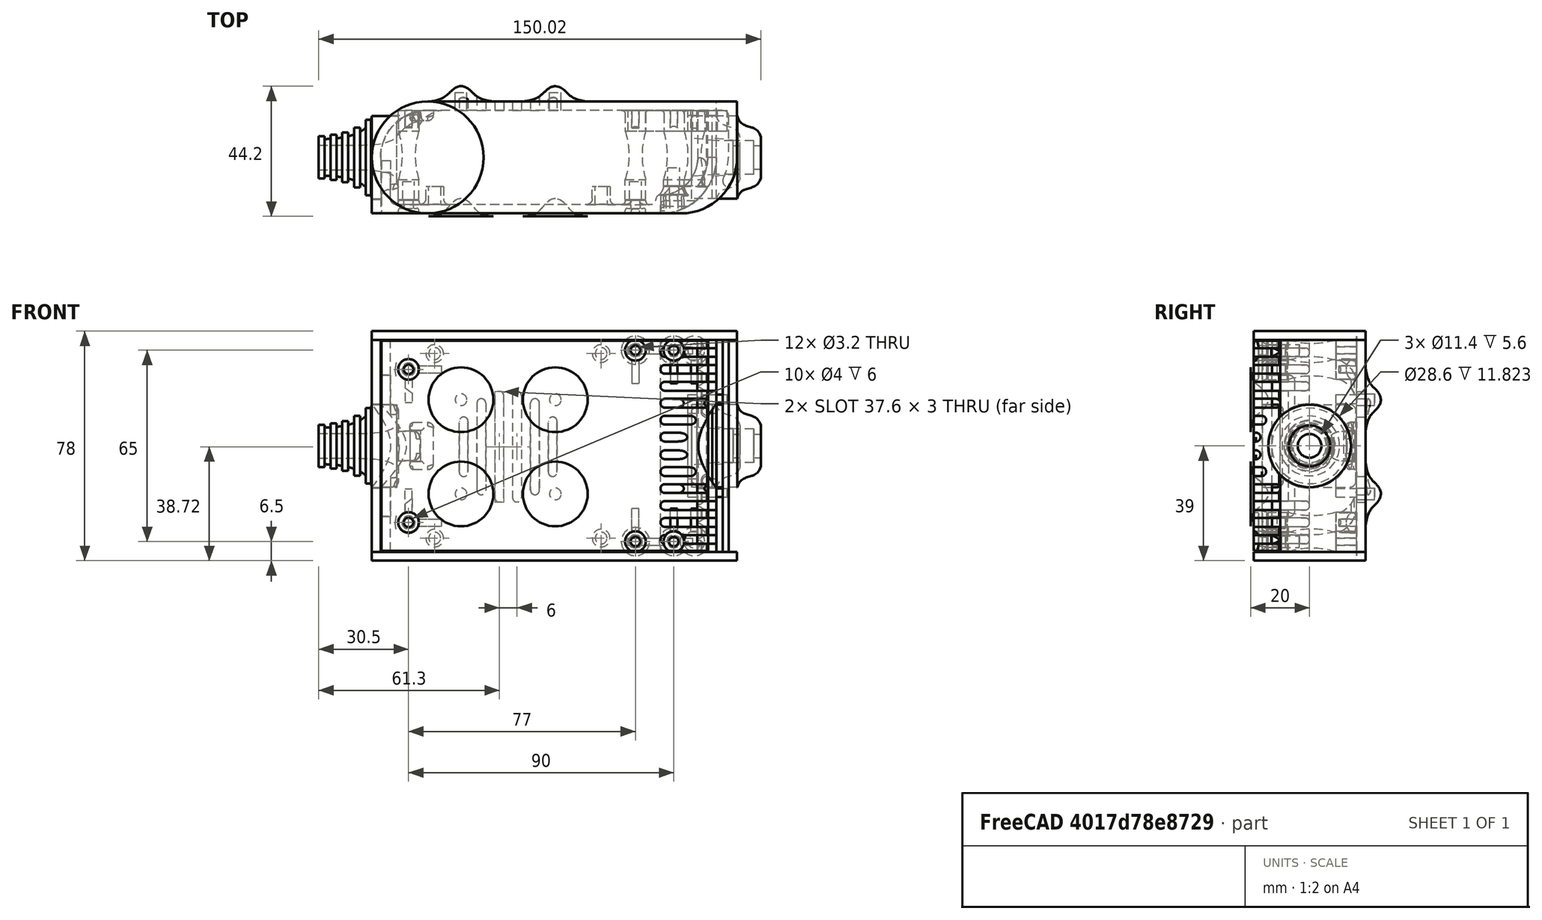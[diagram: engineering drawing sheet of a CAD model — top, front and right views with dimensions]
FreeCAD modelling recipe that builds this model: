
FCSTD DOCUMENT  (FreeCAD 0.19R0.19.2)
Label: enclosure_132
License: All rights reserved
LicenseURL: http://en.wikipedia.org/wiki/All_rights_reserved
objects: Part::Feature×86, Part::Revolution×86, Part::MultiFuse×70, Sketcher::SketchObject×46, Part::Extrusion×34, Part::Fillet×27, Part::Cut×26, Part::Cylinder×24, Part::Box×17, App::MeasureDistance×4
note: 416 computed .brp shape members not serialized (recipe doc carries the construction recipe); baked Part::Feature solids carry a one-line shape summary decoded from their .brp

FEATURE [Sketcher::SketchObject] Sketch  label="topSketch"
  FullyConstrained = true
  sketch-geometry (20):
    g0: LineSegment StartX=5.21097e-06 StartY=3 StartZ=0 EndX=5.21097e-06 EndY=19 EndZ=0
    g1: ArcOfCircle CenterX=19 CenterY=19 CenterZ=0 NormalX=0 NormalY=0 NormalZ=1 AngleXU=0 Radius=19 StartAngle=1.5708 EndAngle=3.14159
    g2: ArcOfCircle CenterX=19 CenterY=19 CenterZ=0 NormalX=0 NormalY=0 NormalZ=1 AngleXU=0 Radius=16 StartAngle=1.5708 EndAngle=3.14159
    g3: LineSegment StartX=114 StartY=35 StartZ=0 EndX=19 EndY=35 EndZ=0
    g4: LineSegment StartX=5.21097e-06 StartY=3 StartZ=0 EndX=5.21097e-06 EndY=0 EndZ=0
    g5: LineSegment StartX=3 StartY=0 StartZ=0 EndX=5.21097e-06 EndY=0 EndZ=0
    g6: LineSegment StartX=3 StartY=19 StartZ=0 EndX=3 EndY=0 EndZ=0
    g7: LineSegment StartX=19 StartY=38 StartZ=0 EndX=124 EndY=38 EndZ=0
    g8: Circle CenterX=119 CenterY=35 CenterZ=0 NormalX=0 NormalY=0 NormalZ=1 AngleXU=0 Radius=1
    g9: Circle CenterX=121 CenterY=35 CenterZ=0 NormalX=0 NormalY=0 NormalZ=1 AngleXU=0 Radius=1
    g10: Circle CenterX=121 CenterY=33 CenterZ=0 NormalX=0 NormalY=0 NormalZ=1 AngleXU=0 Radius=1
    g11: BSplineCurve PolesCount=3 KnotsCount=2 Degree=2 IsPeriodic=0
    g12: GeomPoint X=119 Y=35 Z=0
    g13: GeomPoint X=121 Y=33 Z=0
    g14: LineSegment StartX=119 StartY=35 StartZ=0 EndX=114 EndY=35 EndZ=0
    g15: ArcOfCircle CenterX=105 CenterY=19 CenterZ=0 NormalX=0 NormalY=0 NormalZ=1 AngleXU=0 Radius=19 StartAngle=5.7297 EndAngle=6.28319
    g16: ArcOfCircle CenterX=105 CenterY=19 CenterZ=0 NormalX=0 NormalY=0 NormalZ=1 AngleXU=0 Radius=16 StartAngle=5.60905 EndAngle=6.28319
    g17: LineSegment StartX=121 StartY=33 StartZ=0 EndX=121 EndY=19 EndZ=0
    g18: LineSegment StartX=124 StartY=38 StartZ=0 EndX=124 EndY=19 EndZ=0
    g19: LineSegment StartX=117.5 StartY=9.01251 StartZ=0 EndX=121.163 EndY=9.0125 EndZ=0
  constraints (46):
    c: Vertical(g0)
    c: Block(g0)
    c: Coincident(g1,g0)
    c: Block(g1)
    c: Coincident(g2,g1)
    c: Block(g2)
    c: Coincident(g3,g2)
    c: Horizontal(g3)
    c: Tangent(g3,g2)
    c: Coincident(g4,g0)
    c: Distance(g4) = 3
    c: Vertical(g4)
    c: Coincident(g5,g4)
    c: Horizontal(g5)
    c: Coincident(g6,g2)
    c: Coincident(g6,g5)
    c: Vertical(g6)
    c: Horizontal(g7)
    c: Distance(g7) = 105
    c: Coincident(g7,g1)
    c: Block(g3)
    c: Weight(g8) = 1
    c: Equal(g8,g9)
    c: Equal(g8,g10)
    c: InternalAlignment(g8,g11)
    c: InternalAlignment(g9,g11)
    c: InternalAlignment(g10,g11)
    c: InternalAlignment(g12,g11)
    c: InternalAlignment(g13,g11)
    c: Block(g11)
    c: Coincident(g14,g11)
    c: Coincident(g14,g3)
    c: Horizontal(g14)
    c: Block(g15)
    c: Coincident(g16,g15)
    c: Block(g16)
    c: Coincident(g17,g11)
    c: Coincident(g17,g16)
    c: Vertical(g17)
    c: Distance(g17) = 14
    c: Coincident(g18,g7)
    c: Coincident(g18,g15)
    c: Vertical(g18)
    c: Distance(g18) = 19
    c: Coincident(g19,g16)
    c: Coincident(g19,g15)
FEATURE [Sketcher::SketchObject] Sketch001  label="bottomSketch"
  FullyConstrained = true
  sketch-geometry (32):
    g0: LineSegment StartX=3.3 StartY=-6.03275e-07 StartZ=0 EndX=98 EndY=-6.03275e-07 EndZ=0
    g1: ArcOfCircle CenterX=98 CenterY=19 CenterZ=0 NormalX=0 NormalY=0 NormalZ=1 AngleXU=0 Radius=19 StartAngle=4.71239 EndAngle=5.71103
    g2: LineSegment StartX=6.3 StartY=8 StartZ=0 EndX=3.3 EndY=8 EndZ=0
    g3: LineSegment StartX=3.3 StartY=8 StartZ=0 EndX=3.3 EndY=-6.03275e-07 EndZ=0
    g4: ArcOfCircle CenterX=8.3 CenterY=5 CenterZ=0 NormalX=0 NormalY=0 NormalZ=1 AngleXU=0 Radius=2 StartAngle=3.14159 EndAngle=4.71239
    g5: LineSegment StartX=6.3 StartY=8 StartZ=0 EndX=6.3 EndY=5 EndZ=0
    g6: ArcOfCircle CenterX=98 CenterY=19 CenterZ=0 NormalX=0 NormalY=0 NormalZ=1 AngleXU=0 Radius=12.7 StartAngle=4.71239 EndAngle=6.28319
    g7: LineSegment StartX=94.7 StartY=3 StartZ=0 EndX=8.3 EndY=3 EndZ=0
    g8-g12: Circle x5 (B-spline internal-alignment scaffolding for g13; pole/knot coordinates omitted)
    g13: BSplineCurve PolesCount=5 KnotsCount=3 Degree=3 IsPeriodic=0
    g14: GeomPoint X=98 Y=6.3 Z=0
    g15: GeomPoint X=96.3938 Y=4.71946 Z=0
    g16: GeomPoint X=94.7 Y=3 Z=0
    g17-g23: Circle x7 (B-spline internal-alignment scaffolding for g24; pole/knot coordinates omitted)
    g24: BSplineCurve PolesCount=7 KnotsCount=5 Degree=3 IsPeriodic=0
    g25-g29: GeomPoint x5 (B-spline internal-alignment scaffolding for g24; pole/knot coordinates omitted)
    g30: ArcOfCircle CenterX=98 CenterY=19 CenterZ=0 NormalX=0 NormalY=0 NormalZ=1 AngleXU=0 Radius=15.7 StartAngle=5.81226 EndAngle=6.28319
    g31: LineSegment StartX=110.7 StartY=19 StartZ=0 EndX=113.7 EndY=19 EndZ=0
  constraints (41):
    c: Horizontal(g0)
    c: Coincident(g1,g0)
    c: Block(g1)
    c: Horizontal(g2)
    c: Distance(g2) = 3
    c: Coincident(g3,g2)
    c: Vertical(g3)
    c: Coincident(g3,g0)
    c: Block(g4)
    c: Block(g2)
    c: Coincident(g5,g2)
    c: Coincident(g5,g4)
    c: Vertical(g5)
    c: Coincident(g6,g1)
    c: Block(g6)
    c: Coincident(g7,g4)
    c: Horizontal(g7)
    c: Block(g0)
    c: Block(g7)
    c: Block(g3)
    c: Coincident(g13,g6)
    c: Weight(g8) = 1
    c: Equal(g8, g9-g12) x4
    c: Coincident(g13,g7)
    c: InternalAlignment(g8-g12 -> g13) x5
    c: InternalAlignment(g14,g13)
    c: InternalAlignment(g15,g13)
    c: InternalAlignment(g16,g13)
    c: Block(g13)
    c: Weight(g17) = 1
    c: Equal(g17, g18-g23) x6
    c: Coincident(g24,g1)
    c: InternalAlignment(g17-g23 -> g24) x7
    c: InternalAlignment(g25-g29 -> g24) x5
    c: Block(g24)
    c: Coincident(g30,g24)
    c: Coincident(g31,g6)
    c: Coincident(g31,g30)
    c: Horizontal(g31)
    c: Block(g31)
    c: Block(g30)
FEATURE [Part::Extrusion] Extrude  label="top"
  Base = -> Sketch
  Dir = (0,0,1)
  DirMode = 2
  FaceMakerClass = Part::FaceMakerBullseye
  LengthFwd = 72
  LengthRev = 0
  Solid = true
  Symmetric = false
FEATURE [Part::Extrusion] Extrude001  label="bottom"
  Base = -> Sketch001
  Dir = (0,0,1)
  DirMode = 2
  FaceMakerClass = Part::FaceMakerBullseye
  LengthFwd = 71.4
  LengthRev = 0
  Placement = pos=(0,0,0.3) rot=(0,0,1;0rad)
  Solid = true
  Symmetric = false
FEATURE [Sketcher::SketchObject] Sketch002  label="topSketch001"
  FullyConstrained = true
  sketch-geometry (6):
    g0: ArcOfCircle CenterX=19 CenterY=19 CenterZ=0 NormalX=0 NormalY=0 NormalZ=1 AngleXU=0 Radius=19 StartAngle=1.5708 EndAngle=3.14159
    g1: LineSegment StartX=5.22862e-06 StartY=19 StartZ=0 EndX=5.22862e-06 EndY=1.19904e-11 EndZ=0
    g2: LineSegment StartX=19 StartY=38 StartZ=0 EndX=124 EndY=38 EndZ=0
    g3: LineSegment StartX=5.22862e-06 StartY=1.19904e-11 StartZ=0 EndX=105 EndY=1.19904e-11 EndZ=0
    g4: ArcOfCircle CenterX=105 CenterY=19 CenterZ=0 NormalX=0 NormalY=0 NormalZ=1 AngleXU=0 Radius=19 StartAngle=4.71239 EndAngle=6.28319
    g5: LineSegment StartX=124 StartY=38 StartZ=0 EndX=124 EndY=19 EndZ=0
  constraints (16):
    c: Block(g0)
    c: Coincident(g1,g0)
    c: Vertical(g1)
    c: Horizontal(g2)
    c: Distance(g2) = 105
    c: Coincident(g2,g0)
    c: Distance(g1) = 19
    c: Coincident(g3,g1)
    c: Horizontal(g3)
    c: Distance(g3) = 105
    c: Block(g4)
    c: Coincident(g4,g3)
    c: Coincident(g5,g2)
    c: Coincident(g5,g4)
    c: Vertical(g5)
    c: Distance(g5) = 19
FEATURE [Part::Extrusion] Extrude002  label="sideA"
  Base = -> Sketch002
  Dir = (0,0,1)
  DirMode = 2
  FaceMakerClass = Part::FaceMakerBullseye
  LengthFwd = 3
  LengthRev = 0
  Placement = pos=(0,0,-3) rot=(0,0,1;0rad)
  Solid = true
  Symmetric = false
FEATURE [Sketcher::SketchObject] Sketch003  label="topSketch002"
  FullyConstrained = true
  sketch-geometry (6):
    g0: LineSegment StartX=19 StartY=38 StartZ=0 EndX=117 EndY=38 EndZ=0
    g1: ArcOfCircle CenterX=19 CenterY=19 CenterZ=0 NormalX=0 NormalY=0 NormalZ=1 AngleXU=0 Radius=19 StartAngle=1.5708 EndAngle=3.14159
    g2: LineSegment StartX=117 StartY=38 StartZ=0 EndX=117 EndY=19 EndZ=0
    g3: LineSegment StartX=98 StartY=1.0161e-12 StartZ=0 EndX=5.22862e-06 EndY=1.0161e-12 EndZ=0
    g4: LineSegment StartX=5.22862e-06 StartY=19 StartZ=0 EndX=5.22862e-06 EndY=1.0161e-12 EndZ=0
    g5: ArcOfCircle CenterX=98 CenterY=19 CenterZ=0 NormalX=0 NormalY=0 NormalZ=1 AngleXU=0 Radius=19 StartAngle=4.71239 EndAngle=6.28319
  constraints (16):
    c: Horizontal(g0)
    c: Distance(g0) = 98
    c: Coincident(g1,g0)
    c: Block(g1)
    c: Coincident(g2,g0)
    c: Vertical(g2)
    c: Distance(g2) = 19
    c: Horizontal(g3)
    c: Coincident(g4,g1)
    c: Vertical(g4)
    c: Coincident(g3,g4)
    c: Block(g3)
    c: Coincident(g5,g2)
    c: Coincident(g5,g3)
    c: Block(g0)
    c: Block(g5)
FEATURE [Sketcher::SketchObject] Sketch004
  FullyConstrained = true
  MapMode = 3
  Placement = pos=(0,0,0) rot=(1,0,0;1.5708rad)
  Support = -> [Extrude]
  sketch-geometry (8):
    g0: Circle CenterX=80.351 CenterY=-67.6202 CenterZ=0 NormalX=0 NormalY=0 NormalZ=1 AngleXU=0 Radius=2
    g1: Circle CenterX=80.351 CenterY=-67.6202 CenterZ=0 NormalX=0 NormalY=0 NormalZ=1 AngleXU=0 Radius=3
    g2: Circle CenterX=80.351 CenterY=-4.92017 CenterZ=0 NormalX=0 NormalY=0 NormalZ=1 AngleXU=0 Radius=2
    g3: Circle CenterX=80.351 CenterY=-4.92017 CenterZ=0 NormalX=0 NormalY=0 NormalZ=1 AngleXU=0 Radius=3
    g4: Circle CenterX=23.851 CenterY=-4.92017 CenterZ=0 NormalX=0 NormalY=0 NormalZ=1 AngleXU=0 Radius=2
    g5: Circle CenterX=23.851 CenterY=-4.92017 CenterZ=0 NormalX=0 NormalY=0 NormalZ=1 AngleXU=0 Radius=3
    g6: Circle CenterX=23.851 CenterY=-67.6202 CenterZ=0 NormalX=0 NormalY=0 NormalZ=1 AngleXU=0 Radius=2
    g7: Circle CenterX=23.851 CenterY=-67.6202 CenterZ=0 NormalX=0 NormalY=0 NormalZ=1 AngleXU=0 Radius=3
  constraints (8):
    c: Block(g3)
    c: Block(g2)
    c: Block(g1)
    c: Block(g0)
    c: Block(g6)
    c: Block(g7)
    c: Block(g4)
    c: Block(g5)
FEATURE [Part::Extrusion] Extrude004
  Base = -> Sketch004
  Dir = (0,-1,2e-16)
  DirMode = 2
  FaceMakerClass = Part::FaceMakerBullseye
  LengthFwd = 6
  LengthRev = 0
  Placement = pos=(0,9,0) rot=(0,0,1;0rad)
  Solid = true
  Symmetric = false
FEATURE [Sketcher::SketchObject] Sketch005
  FullyConstrained = true
  MapMode = 3
  Placement = pos=(0,0,0) rot=(1,0,0;1.5708rad)
  Support = -> [Extrude]
  sketch-geometry (8):
    g0: Circle CenterX=80.351 CenterY=-67.6202 CenterZ=0 NormalX=0 NormalY=0 NormalZ=1 AngleXU=0 Radius=3
    g1: Circle CenterX=80.351 CenterY=-4.92017 CenterZ=0 NormalX=0 NormalY=0 NormalZ=1 AngleXU=0 Radius=3
    g2: Circle CenterX=23.851 CenterY=-4.92017 CenterZ=0 NormalX=0 NormalY=0 NormalZ=1 AngleXU=0 Radius=3
    g3: Circle CenterX=23.851 CenterY=-67.6202 CenterZ=0 NormalX=0 NormalY=0 NormalZ=1 AngleXU=0 Radius=3
    g4: Circle CenterX=23.851 CenterY=-67.6202 CenterZ=0 NormalX=0 NormalY=0 NormalZ=1 AngleXU=0 Radius=5
    g5: Circle CenterX=80.351 CenterY=-67.6202 CenterZ=0 NormalX=0 NormalY=0 NormalZ=1 AngleXU=0 Radius=5
    g6: Circle CenterX=23.851 CenterY=-4.92017 CenterZ=0 NormalX=0 NormalY=0 NormalZ=1 AngleXU=0 Radius=5
    g7: Circle CenterX=80.351 CenterY=-4.92017 CenterZ=0 NormalX=0 NormalY=0 NormalZ=1 AngleXU=0 Radius=5
  constraints (8):
    c: Block(g1)
    c: Block(g0)
    c: Block(g3)
    c: Block(g2)
    c: Block(g5)
    c: Block(g4)
    c: Block(g6)
    c: Block(g7)
FEATURE [Part::Extrusion] Extrude005
  Base = -> Sketch005
  Dir = (0,-1,2e-16)
  DirMode = 2
  FaceMakerClass = Part::FaceMakerBullseye
  LengthFwd = 2
  LengthRev = 0
  Solid = true
  Symmetric = false
FEATURE [Sketcher::SketchObject] Sketch006
  FullyConstrained = true
  MapMode = 3
  Placement = pos=(0,0,0) rot=(1,0,0;1.5708rad)
  sketch-geometry (8):
    g0: Circle CenterX=80.351 CenterY=-67.6202 CenterZ=0 NormalX=0 NormalY=0 NormalZ=1 AngleXU=0 Radius=3
    g1: Circle CenterX=80.351 CenterY=-4.92017 CenterZ=0 NormalX=0 NormalY=0 NormalZ=1 AngleXU=0 Radius=3
    g2: Circle CenterX=23.851 CenterY=-4.92017 CenterZ=0 NormalX=0 NormalY=0 NormalZ=1 AngleXU=0 Radius=3
    g3: Circle CenterX=23.851 CenterY=-67.6202 CenterZ=0 NormalX=0 NormalY=0 NormalZ=1 AngleXU=0 Radius=3
    g4: Circle CenterX=23.851 CenterY=-67.6202 CenterZ=0 NormalX=0 NormalY=0 NormalZ=1 AngleXU=0 Radius=5
    g5: Circle CenterX=80.351 CenterY=-67.6202 CenterZ=0 NormalX=0 NormalY=0 NormalZ=1 AngleXU=0 Radius=5
    g6: Circle CenterX=23.851 CenterY=-4.92017 CenterZ=0 NormalX=0 NormalY=0 NormalZ=1 AngleXU=0 Radius=5
    g7: Circle CenterX=80.351 CenterY=-4.92017 CenterZ=0 NormalX=0 NormalY=0 NormalZ=1 AngleXU=0 Radius=5
  constraints (8):
    c: Block(g1)
    c: Block(g0)
    c: Block(g3)
    c: Block(g2)
    c: Block(g5)
    c: Block(g4)
    c: Block(g6)
    c: Block(g7)
FEATURE [Part::Extrusion] Extrude007
  Base = -> Sketch006
  Dir = (0,-1,2e-16)
  DirMode = 2
  FaceMakerClass = Part::FaceMakerBullseye
  LengthFwd = 2
  LengthRev = 0
  Solid = true
  Symmetric = false
FEATURE [Part::Fillet] Fillet
  Base = -> Extrude007
  Edges = 4 edges r=1.99: [Edge6,Edge12,Edge18,Edge24]
FEATURE [Part::Cut] Cut
  Base = -> Extrude005
  Placement = pos=(0,5,0) rot=(0,0,1;0rad)
  Tool = -> Fillet
FEATURE [Part::MultiFuse] Fusion  label="pCBScrews"
  Placement = pos=(-2.5,0,72.3) rot=(0,0,1;0rad)
  Shapes = -> [Extrude004,Cut]
FEATURE [App::MeasureDistance] Distance  label="Distance: 0.69 mm"
  Distance = 0.685967
  P1 = (24.0138,2.9647,0.3)
  P2 = (23.8901,3,-0.373787)
FEATURE [App::MeasureDistance] Distance001  label="Distance: 0.53 mm"
  Distance = 0.533607
  P1 = (80.2939,3,72.2334)
  P2 = (80.281,2.99661,71.7)
FEATURE [Part::Fillet] Fillet001
  Base = -> Extrude001
  Edges = 1 edges r=2.4: [Edge17]
FEATURE [Part::Fillet] Fillet002  label="bottom001"
  Base = -> Fillet001
  Edges = 1 edges r=2.4: [Edge36]
FEATURE [Part::Fillet] Fillet003  label="top001"
  Base = -> Extrude
  Edges = 1 edges r=2: [Edge1]
FEATURE [Sketcher::SketchObject] Sketch007
  FullyConstrained = true
  sketch-geometry (16):
    g0: LineSegment StartX=4 StartY=0 StartZ=0 EndX=4 EndY=2.4 EndZ=0
    g1: LineSegment StartX=4 StartY=2.4 StartZ=0 EndX=7 EndY=2.4 EndZ=0
    g2: LineSegment StartX=4 StartY=0 StartZ=0 EndX=5.7 EndY=0 EndZ=0
    g3: LineSegment StartX=5.7 StartY=0 StartZ=0 EndX=5.7 EndY=-5.6 EndZ=0
    g4-g8: Circle x5 (B-spline internal-alignment scaffolding for g9; pole/knot coordinates omitted)
    g9: BSplineCurve PolesCount=5 KnotsCount=3 Degree=3 IsPeriodic=0
    g10: GeomPoint X=7 Y=2.4 Z=0
    g11: GeomPoint X=10.4582 Y=-1.55472 Z=0
    g12: GeomPoint X=14 Y=-5.6 Z=0
    g13: LineSegment StartX=14 StartY=-5.6 StartZ=0 EndX=14 EndY=-14.1 EndZ=0
    g14: LineSegment StartX=14 StartY=-14.1 StartZ=0 EndX=6.5 EndY=-14.1 EndZ=0
    g15: LineSegment StartX=5.7 StartY=-5.6 StartZ=0 EndX=6.5 EndY=-14.1 EndZ=0
  constraints (28):
    c: Distance(g0) = 2.4
    c: Vertical(g0)
    c: Block(g0)
    c: Coincident(g1,g0)
    c: Horizontal(g1)
    c: Distance(g1) = 3
    c: Coincident(g2,g0)
    c: Horizontal(g2)
    c: Distance(g2) = 1.7
    c: Coincident(g3,g2)
    c: Vertical(g3)
    c: Distance(g3) = 5.6
    c: Coincident(g9,g1)
    c: Weight(g4) = 1
    c: Equal(g4, g5-g8) x4
    c: InternalAlignment(g4-g8 -> g9) x5
    c: InternalAlignment(g10,g9)
    c: InternalAlignment(g11,g9)
    c: InternalAlignment(g12,g9)
    c: Block(g9)
    c: Coincident(g13,g9)
    c: Vertical(g13)
    c: Distance(g13) = 8.5
    c: Coincident(g14,g13)
    c: Horizontal(g14)
    c: Distance(g14) = 7.5
    c: Coincident(g15,g3)
    c: Coincident(g15,g14)
FEATURE [Part::Feature] Face
  shape: bbox 10 x 16.5 x 2e-07 mm, 1 faces, 0 solids (baked)
FEATURE [Part::Revolution] Revolve  label="plugHousing"
  Angle = 360
  Axis = (0,1,0)
  Base = (0,0,0)
  FaceMakerClass = Part::FaceMakerBullseye
  Placement = pos=(0,0,36.15) rot=(0,0,1;0rad)
  Solid = false
  Source = -> Face
  Symmetric = false
FEATURE [Part::Feature] Face001
  shape: bbox 10 x 16.5 x 2e-07 mm, 1 faces, 0 solids (baked)
FEATURE [Part::Revolution] Revolve001  label="plugHousing001"
  Angle = 360
  Axis = (0,1,0)
  Base = (0,0,0)
  FaceMakerClass = Part::FaceMakerBullseye
  Placement = pos=(0,0,36.15) rot=(0,0,1;0rad)
  Solid = false
  Source = -> Face001
  Symmetric = false
FEATURE [Part::MultiFuse] Fusion001  label="plugHousing002"
  Placement = pos=(0,0,0) rot=(0,0,1;1.5708rad)
  Shapes = -> [Revolve001,Revolve]
FEATURE [Part::Feature] Face002
  shape: bbox 10 x 16.5 x 2e-07 mm, 1 faces, 0 solids (baked)
FEATURE [Part::Revolution] Revolve003  label="plugHousing005"
  Angle = 360
  Axis = (0,1,0)
  Base = (0,0,0)
  FaceMakerClass = Part::FaceMakerBullseye
  Placement = pos=(0,0,36.15) rot=(0,0,1;0rad)
  Solid = false
  Source = -> Face002
  Symmetric = false
FEATURE [Part::Feature] Face003
  shape: bbox 10 x 16.5 x 2e-07 mm, 1 faces, 0 solids (baked)
FEATURE [Part::Revolution] Revolve002  label="plugHousing003"
  Angle = 360
  Axis = (0,1,0)
  Base = (0,0,0)
  FaceMakerClass = Part::FaceMakerBullseye
  Placement = pos=(0,0,36.15) rot=(0,0,1;0rad)
  Solid = false
  Source = -> Face003
  Symmetric = false
FEATURE [Part::MultiFuse] Fusion002  label="plugHousing004"
  Placement = pos=(0,0,0) rot=(0,0,1;1.5708rad)
  Shapes = -> [Revolve002,Revolve003]
FEATURE [Part::MultiFuse] Fusion003  label="plugHousing006"
  Placement = pos=(0,19,0) rot=(0,0,1;3.14159rad)
  Shapes = -> [Fusion002,Fusion001]
FEATURE [Part::Feature] Face004
  shape: bbox 10 x 16.5 x 2e-07 mm, 1 faces, 0 solids (baked)
FEATURE [Part::Revolution] Revolve006  label="plugHousing010"
  Angle = 360
  Axis = (0,1,0)
  Base = (0,0,0)
  FaceMakerClass = Part::FaceMakerBullseye
  Placement = pos=(0,0,36.15) rot=(0,0,1;0rad)
  Solid = false
  Source = -> Face004
  Symmetric = false
FEATURE [Part::Feature] Face005
  shape: bbox 10 x 16.5 x 2e-07 mm, 1 faces, 0 solids (baked)
FEATURE [Part::Revolution] Revolve007  label="plugHousing011"
  Angle = 360
  Axis = (0,1,0)
  Base = (0,0,0)
  FaceMakerClass = Part::FaceMakerBullseye
  Placement = pos=(0,0,36.15) rot=(0,0,1;0rad)
  Solid = false
  Source = -> Face005
  Symmetric = false
FEATURE [Part::Feature] Face006
  shape: bbox 10 x 16.5 x 2e-07 mm, 1 faces, 0 solids (baked)
FEATURE [Part::Revolution] Revolve004  label="plugHousing007"
  Angle = 360
  Axis = (0,1,0)
  Base = (0,0,0)
  FaceMakerClass = Part::FaceMakerBullseye
  Placement = pos=(0,0,36.15) rot=(0,0,1;0rad)
  Solid = false
  Source = -> Face006
  Symmetric = false
FEATURE [Part::MultiFuse] Fusion004  label="plugHousing009"
  Placement = pos=(0,0,0) rot=(0,0,1;1.5708rad)
  Shapes = -> [Revolve004,Revolve007]
FEATURE [Part::Feature] Face007
  shape: bbox 10 x 16.5 x 2e-07 mm, 1 faces, 0 solids (baked)
FEATURE [Part::Revolution] Revolve005  label="plugHousing008"
  Angle = 360
  Axis = (0,1,0)
  Base = (0,0,0)
  FaceMakerClass = Part::FaceMakerBullseye
  Placement = pos=(0,0,36.15) rot=(0,0,1;0rad)
  Solid = false
  Source = -> Face007
  Symmetric = false
FEATURE [Part::MultiFuse] Fusion005  label="plugHousing012"
  Placement = pos=(0,0,0) rot=(0,0,1;1.5708rad)
  Shapes = -> [Revolve006,Revolve005]
FEATURE [Part::MultiFuse] Fusion006  label="plugHousing013"
  Placement = pos=(0,19,0) rot=(0,0,1;3.14159rad)
  Shapes = -> [Fusion005,Fusion004]
FEATURE [Part::MultiFuse] Fusion007  label="plugHousing014"
  Placement = pos=(122.621,0,-0.15) rot=(0,0,1;0rad)
  Shapes = -> [Fusion003,Fusion006]
FEATURE [Part::Cylinder] Cylinder002
  Angle = 360
  AttacherType = Attacher::AttachEngine3D
  Height = 20
  Placement = pos=(0,0,36.15) rot=(0,0,1;0rad)
  Radius = 4
FEATURE [Part::Cylinder] Cylinder003
  Angle = 360
  AttacherType = Attacher::AttachEngine3D
  Height = 10
  Placement = pos=(0,0,36.15) rot=(0,0,1;0rad)
  Radius = 4
FEATURE [Part::MultiFuse] Fusion009  label="removeToCreateHoleForPlugHousing"
  Placement = pos=(70,19,36.15) rot=(0,1,0;1.5708rad)
  Shapes = -> [Cylinder002,Cylinder003]
FEATURE [Part::Cylinder] Cylinder004
  Angle = 360
  AttacherType = Attacher::AttachEngine3D
  Height = 20
  Placement = pos=(0,0,36.15) rot=(0,0,1;0rad)
  Radius = 4
FEATURE [Part::Cylinder] Cylinder005
  Angle = 360
  AttacherType = Attacher::AttachEngine3D
  Height = 10
  Placement = pos=(0,0,36.15) rot=(0,0,1;0rad)
  Radius = 4
FEATURE [Part::MultiFuse] Fusion010  label="removeToCreateHoleForPlugHousing001"
  Placement = pos=(70,19,36.15) rot=(0,1,0;1.5708rad)
  Shapes = -> [Cylinder004,Cylinder005]
FEATURE [Part::Cut] Cut001
  Base = -> Fillet003
  Tool = -> Fusion010
FEATURE [Part::Cut] Cut002  label="Bottom"
  Base = -> Fillet002
  Tool = -> Fusion009
FEATURE [Part::Feature] Face008
  shape: bbox 10 x 16.5 x 2e-07 mm, 1 faces, 0 solids (baked)
FEATURE [Part::Revolution] Revolve011  label="plugHousing021"
  Angle = 360
  Axis = (0,1,0)
  Base = (0,0,0)
  FaceMakerClass = Part::FaceMakerBullseye
  Placement = pos=(0,0,36.15) rot=(0,0,1;0rad)
  Solid = false
  Source = -> Face008
  Symmetric = false
FEATURE [Part::Feature] Face009
  shape: bbox 10 x 16.5 x 2e-07 mm, 1 faces, 0 solids (baked)
FEATURE [Part::Revolution] Revolve012  label="plugHousing022"
  Angle = 360
  Axis = (0,1,0)
  Base = (0,0,0)
  FaceMakerClass = Part::FaceMakerBullseye
  Placement = pos=(0,0,36.15) rot=(0,0,1;0rad)
  Solid = false
  Source = -> Face009
  Symmetric = false
FEATURE [Part::Feature] Face010 .. Face013  x4 (patterned run collapsed; names and placements below)
  shape: bbox 10 x 16.5 x 2e-07 mm, 1 faces, 0 solids (baked)
FEATURE [Part::Revolution] Revolve015  label="plugHousing027"
  Angle = 360
  Axis = (0,1,0)
  Base = (0,0,0)
  FaceMakerClass = Part::FaceMakerBullseye
  Placement = pos=(0,0,36.15) rot=(0,0,1;0rad)
  Solid = false
  Source = -> Face013
  Symmetric = false
FEATURE [Part::Feature] Face014
  shape: bbox 10 x 16.5 x 2e-07 mm, 1 faces, 0 solids (baked)
FEATURE [Part::Feature] Face015
  shape: bbox 10 x 16.5 x 2e-07 mm, 1 faces, 0 solids (baked)
FEATURE [Part::Feature] Face016
  shape: bbox 10 x 16.5 x 2e-07 mm, 1 faces, 0 solids (baked)
FEATURE [Part::Revolution] Revolve019  label="plugHousing033"
  Angle = 360
  Axis = (0,1,0)
  Base = (0,0,0)
  FaceMakerClass = Part::FaceMakerBullseye
  Placement = pos=(0,0,36.15) rot=(0,0,1;0rad)
  Solid = false
  Source = -> Face016
  Symmetric = false
FEATURE [Part::Feature] Face017
  shape: bbox 10 x 16.5 x 2e-07 mm, 1 faces, 0 solids (baked)
FEATURE [Part::Revolution] Revolve020  label="plugHousing034"
  Angle = 360
  Axis = (0,1,0)
  Base = (0,0,0)
  FaceMakerClass = Part::FaceMakerBullseye
  Placement = pos=(0,0,36.15) rot=(0,0,1;0rad)
  Solid = false
  Source = -> Face017
  Symmetric = false
FEATURE [Part::Feature] Face018
  shape: bbox 10 x 16.5 x 2e-07 mm, 1 faces, 0 solids (baked)
FEATURE [Part::Revolution] Revolve016  label="plugHousing030"
  Angle = 360
  Axis = (0,1,0)
  Base = (0,0,0)
  FaceMakerClass = Part::FaceMakerBullseye
  Placement = pos=(0,0,36.15) rot=(0,0,1;0rad)
  Solid = false
  Source = -> Face018
  Symmetric = false
FEATURE [Part::MultiFuse] Fusion020  label="plugHousing038"
  Placement = pos=(0,0,0) rot=(0,0,1;1.5708rad)
  Shapes = -> [Revolve016,Revolve020]
FEATURE [Part::Feature] Face019
  shape: bbox 10 x 16.5 x 2e-07 mm, 1 faces, 0 solids (baked)
FEATURE [Part::Feature] Face020
  shape: bbox 10 x 16.5 x 2e-07 mm, 1 faces, 0 solids (baked)
FEATURE [Part::Revolution] Revolve017  label="plugHousing031"
  Angle = 360
  Axis = (0,1,0)
  Base = (0,0,0)
  FaceMakerClass = Part::FaceMakerBullseye
  Placement = pos=(0,0,36.15) rot=(0,0,1;0rad)
  Solid = false
  Source = -> Face020
  Symmetric = false
FEATURE [Part::MultiFuse] Fusion021  label="plugHousing039"
  Placement = pos=(0,0,0) rot=(0,0,1;1.5708rad)
  Shapes = -> [Revolve019,Revolve017]
FEATURE [Part::MultiFuse] Fusion023  label="plugHousing041"
  Placement = pos=(0,19,0) rot=(0,0,1;3.14159rad)
  Shapes = -> [Fusion021,Fusion020]
FEATURE [Part::Revolution] Revolve022  label="plugHousing043"
  Angle = 360
  Axis = (0,1,0)
  Base = (0,0,0)
  FaceMakerClass = Part::FaceMakerBullseye
  Placement = pos=(0,0,36.15) rot=(0,0,1;0rad)
  Solid = false
  Source = -> Face019
  Symmetric = false
FEATURE [Part::Feature] Face021
  shape: bbox 10 x 16.5 x 2e-07 mm, 1 faces, 0 solids (baked)
FEATURE [Part::Revolution] Revolve023  label="plugHousing044"
  Angle = 360
  Axis = (0,1,0)
  Base = (0,0,0)
  FaceMakerClass = Part::FaceMakerBullseye
  Placement = pos=(0,0,36.15) rot=(0,0,1;0rad)
  Solid = false
  Source = -> Face021
  Symmetric = false
FEATURE [Part::Feature] Face022
  shape: bbox 10 x 16.5 x 2e-07 mm, 1 faces, 0 solids (baked)
FEATURE [Part::Revolution] Revolve018  label="plugHousing032"
  Angle = 360
  Axis = (0,1,0)
  Base = (0,0,0)
  FaceMakerClass = Part::FaceMakerBullseye
  Placement = pos=(0,0,36.15) rot=(0,0,1;0rad)
  Solid = false
  Source = -> Face022
  Symmetric = false
FEATURE [Part::MultiFuse] Fusion022  label="plugHousing040"
  Placement = pos=(0,0,0) rot=(0,0,1;1.5708rad)
  Shapes = -> [Revolve018,Revolve023]
FEATURE [Part::Feature] Face023
  shape: bbox 10 x 16.5 x 2e-07 mm, 1 faces, 0 solids (baked)
FEATURE [Part::Revolution] Revolve021  label="plugHousing035"
  Angle = 360
  Axis = (0,1,0)
  Base = (0,0,0)
  FaceMakerClass = Part::FaceMakerBullseye
  Placement = pos=(0,0,36.15) rot=(0,0,1;0rad)
  Solid = false
  Source = -> Face023
  Symmetric = false
FEATURE [Part::MultiFuse] Fusion018  label="plugHousing036"
  Placement = pos=(0,0,0) rot=(0,0,1;1.5708rad)
  Shapes = -> [Revolve022,Revolve021]
FEATURE [Part::MultiFuse] Fusion019  label="plugHousing037"
  Placement = pos=(0,19,0) rot=(0,0,1;3.14159rad)
  Shapes = -> [Fusion018,Fusion022]
FEATURE [Part::MultiFuse] Fusion024  label="plugHousing042"
  Placement = pos=(122.621,0,-0.15) rot=(0,0,1;0rad)
  Shapes = -> [Fusion023,Fusion019]
FEATURE [Part::Cylinder] Cylinder006
  Angle = 360
  AttacherType = Attacher::AttachEngine3D
  Height = 20
  Placement = pos=(0,0,36.15) rot=(0,0,1;0rad)
  Radius = 14.3
FEATURE [Part::Cylinder] Cylinder007
  Angle = 360
  AttacherType = Attacher::AttachEngine3D
  Height = 10
  Placement = pos=(0,0,36.15) rot=(0,0,1;0rad)
  Radius = 4
FEATURE [Part::MultiFuse] Fusion026  label="removeToCreteHoleForPlugHousing"
  Placement = pos=(70,19,36) rot=(0,1,0;1.5708rad)
  Shapes = -> [Cylinder006,Cylinder007]
FEATURE [Part::Box] Box001  label="Cube001"
  AttacherType = Attacher::AttachEngine3D
  Height = 28
  Length = 3
  Placement = pos=(110.7,19,22) rot=(0,0,1;0rad)
  Width = 15.7
FEATURE [Part::Cut] Cut003  label="top002"
  Base = -> Cut001
  Tool = -> Fusion007
FEATURE [Part::Revolution] Revolve008  label="plugHousing015"
  Angle = 360
  Axis = (0,1,0)
  Base = (0,0,0)
  FaceMakerClass = Part::FaceMakerBullseye
  Placement = pos=(0,0,36.15) rot=(0,0,1;0rad)
  Solid = false
  Source = -> Face010
  Symmetric = false
FEATURE [Part::MultiFuse] Fusion013  label="plugHousing020"
  Placement = pos=(0,0,0) rot=(0,0,1;1.5708rad)
  Shapes = -> [Revolve008,Revolve012]
FEATURE [Part::Cut] Cut004  label="top003"
  Base = -> Cut003
  Placement = pos=(1,0,0) rot=(0,0,1;0rad)
  Tool = -> Fusion026
FEATURE [Part::Cylinder] Cylinder008
  Angle = 360
  AttacherType = Attacher::AttachEngine3D
  Height = 20
  Placement = pos=(0,0,36.15) rot=(0,0,1;0rad)
  Radius = 10.3
FEATURE [Part::Cylinder] Cylinder009
  Angle = 360
  AttacherType = Attacher::AttachEngine3D
  Height = 10
  Placement = pos=(0,0,36.15) rot=(0,0,1;0rad)
  Radius = 4
FEATURE [Part::MultiFuse] Fusion027  label="removeToCreteHoleForPlugHousing001"
  Placement = pos=(70,19,36) rot=(0,1,0;1.5708rad)
  Shapes = -> [Cylinder008,Cylinder009]
FEATURE [Part::Cut] Cut005  label="plugHousingTab"
  Base = -> Box001
  Tool = -> Fusion027
FEATURE [Part::MultiFuse] Fusion028  label="plugHousing045"
  Shapes = -> [Fusion024,Cut005]
FEATURE [Part::Box] Box002  label="Cube002"
  AttacherType = Attacher::AttachEngine3D
  Height = 28.8
  Length = 3
  Placement = pos=(107.3,28,21.6) rot=(0,0,1;0rad)
  Width = 7
FEATURE [Part::Box] Box003  label="Cube003"
  AttacherType = Attacher::AttachEngine3D
  Height = 3
  Length = 6.4
  Placement = pos=(107.3,28,18.6) rot=(0,0,1;0rad)
  Width = 7
FEATURE [Part::Box] Box004  label="Cube004"
  AttacherType = Attacher::AttachEngine3D
  Height = 3
  Length = 6.4
  Placement = pos=(107.3,28,50.4) rot=(0,0,1;0rad)
  Width = 7
FEATURE [Part::MultiFuse] Fusion029  label="plugHousingBracketHolder"
  Shapes = -> [Box004,Box002,Box003]
FEATURE [Part::Cylinder] Cylinder010
  Angle = 360
  AttacherType = Attacher::AttachEngine3D
  Height = 20
  Placement = pos=(0,0,36.15) rot=(0,0,1;0rad)
  Radius = 14.3
FEATURE [Part::Cylinder] Cylinder011
  Angle = 360
  AttacherType = Attacher::AttachEngine3D
  Height = 10
  Placement = pos=(0,0,36.15) rot=(0,0,1;0rad)
  Radius = 4
FEATURE [Part::MultiFuse] Fusion030  label="removeToCreteHoleForPlugHousing002"
  Placement = pos=(70,19,36) rot=(0,1,0;1.5708rad)
  Shapes = -> [Cylinder010,Cylinder011]
FEATURE [Part::Cut] Cut006  label="plugHousingBracketHolder001"
  Base = -> Fusion029
  Tool = -> Fusion030
FEATURE [Part::Cylinder] Cylinder012
  Angle = 360
  AttacherType = Attacher::AttachEngine3D
  Height = 20
  Placement = pos=(0,0,36.15) rot=(0,0,1;0rad)
  Radius = 7
FEATURE [Part::Cylinder] Cylinder013
  Angle = 360
  AttacherType = Attacher::AttachEngine3D
  Height = 10
  Placement = pos=(0,0,36.15) rot=(0,0,1;0rad)
  Radius = 4
FEATURE [Part::MultiFuse] Fusion032  label="removeToCreteHoleForPlugHousing003"
  Placement = pos=(70,19,36) rot=(0,1,0;1.5708rad)
  Shapes = -> [Cylinder012,Cylinder013]
FEATURE [Part::Cut] Cut007  label="bottom002"
  Base = -> Cut002
  Tool = -> Fusion032
FEATURE [Sketcher::SketchObject] Sketch008
  FullyConstrained = true
  sketch-geometry (54):
    g0: LineSegment StartX=-4.2 StartY=0 StartZ=0 EndX=-6.2 EndY=0 EndZ=0
    g1: LineSegment StartX=-14 StartY=-18 StartZ=0 EndX=-14 EndY=-26.5 EndZ=0
    g2: LineSegment StartX=-4.2 StartY=0 StartZ=0 EndX=-4.2 EndY=-13.4877 EndZ=0
    g3: Circle CenterX=-4.2 CenterY=-13.4877 CenterZ=0 NormalX=0 NormalY=0 NormalZ=1 AngleXU=0 Radius=1
    g4: Circle CenterX=-4.2 CenterY=-26.5 CenterZ=0 NormalX=0 NormalY=0 NormalZ=1 AngleXU=0 Radius=1
    g5: Circle CenterX=-8.2 CenterY=-26.5 CenterZ=0 NormalX=0 NormalY=0 NormalZ=1 AngleXU=0 Radius=1
    g6: BSplineCurve PolesCount=3 KnotsCount=2 Degree=2 IsPeriodic=0
    g7: GeomPoint X=-4.2 Y=-13.4877 Z=0
    g8: GeomPoint X=-8.2 Y=-26.5 Z=0
    g9: LineSegment StartX=-14 StartY=-26.5 StartZ=0 EndX=-8.2 EndY=-26.5 EndZ=0
    g10: LineSegment StartX=-10.15 StartY=-12 StartZ=0 EndX=-10.15 EndY=-14 EndZ=0
    g11: LineSegment StartX=-12.8401 StartY=-16 StartZ=0 EndX=-10.1571 EndY=-16 EndZ=0
    g12: LineSegment StartX=-10.15 StartY=-14 StartZ=0 EndX=-8.70761 EndY=-14 EndZ=0
    g13: LineSegment StartX=-12.8401 StartY=-16 StartZ=0 EndX=-12.8401 EndY=-17.6958 EndZ=0
    g14: LineSegment StartX=-10.15 StartY=-12 StartZ=0 EndX=-7.79258 EndY=-12 EndZ=0
    g15: Circle CenterX=-6.2215 CenterY=-2 CenterZ=0 NormalX=0 NormalY=0 NormalZ=1 AngleXU=0 Radius=1
    g16: Circle CenterX=-6.22762 CenterY=-2.58724 CenterZ=0 NormalX=0 NormalY=0 NormalZ=1 AngleXU=0 Radius=1
    g17: Circle CenterX=-6.32538 CenterY=-4 CenterZ=0 NormalX=0 NormalY=0 NormalZ=1 AngleXU=0 Radius=1
    g18: BSplineCurve PolesCount=3 KnotsCount=2 Degree=2 IsPeriodic=0
    g19: GeomPoint X=-6.2215 Y=-2 Z=0
    g20: GeomPoint X=-6.32538 Y=-4 Z=0
    g21: Circle CenterX=-6.48644 CenterY=-5.99526 CenterZ=0 NormalX=0 NormalY=0 NormalZ=1 AngleXU=0 Radius=1
    g22: Circle CenterX=-6.58486 CenterY=-6.99526 CenterZ=0 NormalX=0 NormalY=0 NormalZ=1 AngleXU=0 Radius=1
    g23: Circle CenterX=-6.77343 CenterY=-8 CenterZ=0 NormalX=0 NormalY=0 NormalZ=1 AngleXU=0 Radius=1
    g24: BSplineCurve PolesCount=3 KnotsCount=2 Degree=2 IsPeriodic=0
    g25: GeomPoint X=-6.48644 Y=-5.99526 Z=0
    g26: GeomPoint X=-6.77343 Y=-8 Z=0
    g27: Circle CenterX=-7.19003 CenterY=-10 CenterZ=0 NormalX=0 NormalY=0 NormalZ=1 AngleXU=0 Radius=1
    g28: Circle CenterX=-7.44407 CenterY=-11.0915 CenterZ=0 NormalX=0 NormalY=0 NormalZ=1 AngleXU=0 Radius=1
    g29: Circle CenterX=-7.79258 CenterY=-12 CenterZ=0 NormalX=0 NormalY=0 NormalZ=1 AngleXU=0 Radius=1
    g30: BSplineCurve PolesCount=3 KnotsCount=2 Degree=2 IsPeriodic=0
    g31: GeomPoint X=-7.19003 Y=-10 Z=0
    g32: GeomPoint X=-7.79258 Y=-12 Z=0
    g33: Circle CenterX=-8.70761 CenterY=-14 CenterZ=0 NormalX=0 NormalY=0 NormalZ=1 AngleXU=0 Radius=1
    g34: Circle CenterX=-9.33087 CenterY=-15.1837 CenterZ=0 NormalX=0 NormalY=0 NormalZ=1 AngleXU=0 Radius=1
    g35: Circle CenterX=-10.1571 CenterY=-16 CenterZ=0 NormalX=0 NormalY=0 NormalZ=1 AngleXU=0 Radius=1
    g36: BSplineCurve PolesCount=3 KnotsCount=2 Degree=2 IsPeriodic=0
    g37: GeomPoint X=-8.70761 Y=-14 Z=0
    g38: GeomPoint X=-10.1571 Y=-16 Z=0
    g39: Circle CenterX=-12.8401 CenterY=-17.6958 CenterZ=0 NormalX=0 NormalY=0 NormalZ=1 AngleXU=0 Radius=1
    g40: Circle CenterX=-13.3521 CenterY=-17.9027 CenterZ=0 NormalX=0 NormalY=0 NormalZ=1 AngleXU=0 Radius=1
    g41: Circle CenterX=-14 CenterY=-18 CenterZ=0 NormalX=0 NormalY=0 NormalZ=1 AngleXU=0 Radius=1
    g42: BSplineCurve PolesCount=3 KnotsCount=2 Degree=2 IsPeriodic=0
    g43: GeomPoint X=-12.8401 Y=-17.6958 Z=0
    g44: GeomPoint X=-14 Y=-18 Z=0
    g45: LineSegment StartX=-6.2 StartY=0 StartZ=0 EndX=-7.2 EndY=0 EndZ=0
    g46: LineSegment StartX=-7.2 StartY=0 StartZ=0 EndX=-7.2 EndY=-2 EndZ=0
    g47: LineSegment StartX=-7.2 StartY=-2 StartZ=0 EndX=-6.2215 EndY=-2 EndZ=0
    g48: LineSegment StartX=-6.32538 StartY=-4 StartZ=0 EndX=-7.65538 EndY=-4 EndZ=0
    g49: LineSegment StartX=-7.65538 StartY=-4 StartZ=0 EndX=-7.65538 EndY=-5.99526 EndZ=0
    g50: LineSegment StartX=-7.65538 StartY=-5.99526 StartZ=0 EndX=-6.48644 EndY=-5.99526 EndZ=0
    g51: LineSegment StartX=-6.77343 StartY=-8 StartZ=0 EndX=-8.43343 EndY=-8 EndZ=0
    g52: LineSegment StartX=-8.43343 StartY=-8 StartZ=0 EndX=-8.43343 EndY=-10 EndZ=0
    g53: LineSegment StartX=-8.43343 StartY=-10 StartZ=0 EndX=-7.19003 EndY=-10 EndZ=0
  constraints (112):
    c: Horizontal(g0)
    c: Distance(g0) = 2
    c: Block(g0)
    c: Vertical(g1)
    c: Coincident(g2,g0)
    c: Vertical(g2)
    c: Block(g2)
    c: Coincident(g6,g2)
    c: Weight(g3) = 1
    c: Equal(g3,g4)
    c: Equal(g3,g5)
    c: InternalAlignment(g3,g6)
    c: InternalAlignment(g4,g6)
    c: InternalAlignment(g5,g6)
    c: InternalAlignment(g7,g6)
    c: InternalAlignment(g8,g6)
    c: Block(g6)
    c: Coincident(g9,g1)
    c: Coincident(g9,g6)
    c: Horizontal(g9)
    c: Vertical(g10)
    c: Block(g10)
    c: Horizontal(g11)
    c: Block(g11)
    c: Coincident(g12,g10)
    c: Horizontal(g12)
    c: Block(g12)
    c: Coincident(g13,g11)
    c: Vertical(g13)
    c: Block(g13)
    c: Coincident(g14,g10)
    c: Horizontal(g14)
    c: Block(g14)
    c: Block(g9)
    c: Block(g1)
    c: Weight(g15) = 1
    c: Equal(g15,g16)
    c: Equal(g15,g17)
    c: InternalAlignment(g15,g18)
    c: InternalAlignment(g16,g18)
    c: InternalAlignment(g17,g18)
    c: InternalAlignment(g19,g18)
    c: InternalAlignment(g20,g18)
    c: Weight(g21) = 1
    c: Equal(g21,g22)
    c: Equal(g21,g23)
    c: InternalAlignment(g21,g24)
    c: InternalAlignment(g22,g24)
    c: InternalAlignment(g23,g24)
    c: InternalAlignment(g25,g24)
    c: InternalAlignment(g26,g24)
    c: Weight(g27) = 1
    c: Equal(g27,g28)
    c: Equal(g27,g29)
    c: Coincident(g30,g14)
    c: InternalAlignment(g27,g30)
    c: InternalAlignment(g28,g30)
    c: InternalAlignment(g29,g30)
    c: InternalAlignment(g31,g30)
    c: InternalAlignment(g32,g30)
    c: Coincident(g36,g12)
    c: Weight(g33) = 1
    c: Equal(g33,g34)
    c: Equal(g33,g35)
    c: Coincident(g36,g11)
    c: InternalAlignment(g33,g36)
    c: InternalAlignment(g34,g36)
    c: InternalAlignment(g35,g36)
    c: InternalAlignment(g37,g36)
    c: InternalAlignment(g38,g36)
    c: Coincident(g42,g13)
    c: Weight(g39) = 1
    c: Equal(g39,g40)
    c: Equal(g39,g41)
    c: Coincident(g42,g1)
    c: InternalAlignment(g39,g42)
    c: InternalAlignment(g40,g42)
    c: InternalAlignment(g41,g42)
    c: InternalAlignment(g43,g42)
    c: InternalAlignment(g44,g42)
    c: Block(g18)
    c: Block(g24)
    c: Block(g30)
    c: Block(g36)
    c: Block(g42)
    c: Horizontal(g45)
    c: Coincident(g45,g0)
    c: Vertical(g46)
    c: Coincident(g46,g45)
    c: Coincident(g47,g46)
    c: Coincident(g47,g18)
    c: Horizontal(g47)
    c: Block(g46)
    c: Coincident(g48,g18)
    c: Horizontal(g48)
    c: Distance(g48) = 1.33
    c: Vertical(g49)
    c: Coincident(g49,g48)
    c: Coincident(g50,g49)
    c: Coincident(g50,g24)
    c: Horizontal(g50)
    c: Tangent(g50,g22)
    c: Horizontal(g51)
    c: Coincident(g51,g24)
    c: Block(g51)
    c: Vertical(g52)
    c: Block(g52)
    c: Coincident(g52,g51)
    c: Coincident(g53,g52)
    c: Coincident(g53,g30)
    c: Horizontal(g53)
    c: Distance(g1) = 8.5
FEATURE [Part::Feature] Face024
  shape: bbox 9.8 x 26.5 x 2e-07 mm, 1 faces, 0 solids (baked)
FEATURE [Part::Revolution] Revolve024
  Angle = 360
  Axis = (0,1,0)
  Base = (0,0,0)
  FaceMakerClass = Part::FaceMakerBullseye
  Placement = pos=(0,0,0) rot=(0,0,1;1.5708rad)
  Solid = false
  Source = -> Face024
  Symmetric = false
FEATURE [Part::Feature] Face025
  shape: bbox 9.8 x 26.5 x 2e-07 mm, 1 faces, 0 solids (baked)
FEATURE [Part::Revolution] Revolve025
  Angle = 360
  Axis = (0,1,0)
  Base = (0,0,0)
  FaceMakerClass = Part::FaceMakerBullseye
  Placement = pos=(0,0,0) rot=(0,0,1;1.5708rad)
  Solid = false
  Source = -> Face025
  Symmetric = false
FEATURE [Part::MultiFuse] Fusion033
  Placement = pos=(-18,19,36) rot=(0,0,1;0rad)
  Shapes = -> [Revolve025,Revolve024]
FEATURE [Part::Cylinder] Cylinder014
  Angle = 360
  AttacherType = Attacher::AttachEngine3D
  Height = 20
  Placement = pos=(0,0,36.15) rot=(0,0,1;0rad)
  Radius = 14.3
FEATURE [Part::Cylinder] Cylinder015
  Angle = 360
  AttacherType = Attacher::AttachEngine3D
  Height = 10
  Placement = pos=(0,0,36.15) rot=(0,0,1;0rad)
  Radius = 4
FEATURE [Part::MultiFuse] Fusion034  label="removeToCreteHoleForPlugHousing004"
  Placement = pos=(-42,19,36) rot=(0,1,0;1.5708rad)
  Shapes = -> [Cylinder014,Cylinder015]
FEATURE [Part::Cut] Cut008  label="top004"
  Base = -> Cut004
  Placement = pos=(-1,0,0) rot=(0,0,1;0rad)
  Tool = -> Fusion034
FEATURE [Part::Box] Box005  label="Cube005"
  AttacherType = Attacher::AttachEngine3D
  Height = 28
  Length = 3
  Placement = pos=(110.7,19,22) rot=(0,0,1;0rad)
  Width = 15.7
FEATURE [Part::Cylinder] Cylinder016
  Angle = 360
  AttacherType = Attacher::AttachEngine3D
  Height = 10
  Placement = pos=(0,0,36.15) rot=(0,0,1;0rad)
  Radius = 4
FEATURE [Part::Cylinder] Cylinder017
  Angle = 360
  AttacherType = Attacher::AttachEngine3D
  Height = 20
  Placement = pos=(0,0,36.15) rot=(0,0,1;0rad)
  Radius = 10.3
FEATURE [Part::MultiFuse] Fusion035  label="removeToCreteHoleForPlugHousing005"
  Placement = pos=(70,19,36) rot=(0,1,0;1.5708rad)
  Shapes = -> [Cylinder017,Cylinder016]
FEATURE [Part::Cut] Cut009  label="plugHousingTab001"
  Base = -> Box005
  Placement = pos=(-107.4,-14,0) rot=(0,0,1;0rad)
  Tool = -> Fusion035
FEATURE [Part::Box] Box006  label="Cube006"
  AttacherType = Attacher::AttachEngine3D
  Height = 28
  Length = 3
  Placement = pos=(110.7,19,22) rot=(0,0,1;0rad)
  Width = 15.7
FEATURE [Part::Cylinder] Cylinder018
  Angle = 360
  AttacherType = Attacher::AttachEngine3D
  Height = 10
  Placement = pos=(0,0,36.15) rot=(0,0,1;0rad)
  Radius = 4
FEATURE [Part::Cylinder] Cylinder019
  Angle = 360
  AttacherType = Attacher::AttachEngine3D
  Height = 20
  Placement = pos=(0,0,36.15) rot=(0,0,1;0rad)
  Radius = 10.3
FEATURE [Part::MultiFuse] Fusion036  label="removeToCreteHoleForPlugHousing006"
  Placement = pos=(70,19,36) rot=(0,1,0;1.5708rad)
  Shapes = -> [Cylinder019,Cylinder018]
FEATURE [Part::Cut] Cut010  label="plugHousingTab002"
  Base = -> Box006
  Placement = pos=(-107.4,-14,0) rot=(0,0,1;0rad)
  Tool = -> Fusion036
FEATURE [Part::MultiFuse] Fusion037
  Placement = pos=(9.6,23,0) rot=(0,0,1;3.14159rad)
  Shapes = -> [Cut009,Cut010]
FEATURE [Part::Box] Box  label="Cube"
  AttacherType = Attacher::AttachEngine3D
  Height = 10
  Length = 3
  Placement = pos=(3.3,4,12) rot=(0,0,1;0rad)
  Width = 10
FEATURE [Part::Fillet] Fillet004
  Base = -> Fusion028
  Edges = 1 edges r=2: [Edge25]
FEATURE [Part::Fillet] Fillet005  label="plugHousing046"
  Base = -> Fillet004
  Edges = 1 edges r=2: [Edge8]
FEATURE [Part::Fillet] Fillet006
  Base = -> Box
  Edges = 1 edges r=2: [Edge11]
FEATURE [Part::Box] Box007  label="Cube007"
  AttacherType = Attacher::AttachEngine3D
  Height = 10
  Length = 3
  Placement = pos=(3.3,4,50) rot=(0,0,1;0rad)
  Width = 10
FEATURE [Part::Fillet] Fillet007
  Base = -> Box007
  Edges = 1 edges r=2: [Edge12]
FEATURE [Part::Box] Box008  label="Cube008"
  AttacherType = Attacher::AttachEngine3D
  Height = 28
  Length = 4
  Placement = pos=(5,0,22) rot=(0,0,1;0rad)
  Width = 10
FEATURE [Part::Fillet] Fillet008
  Base = -> Box008
  Edges = 1 edges r=1: [Edge7]
FEATURE [Part::Fillet] Fillet009
  Base = -> Fillet008
  Edges = 1 edges r=2: [Edge5]
FEATURE [Part::Fillet] Fillet010
  Base = -> Fillet009
  Edges = 1 edges r=2: [Edge2]
FEATURE [Sketcher::SketchObject] Sketch009  label="topSketch003"
  FullyConstrained = true
  sketch-geometry (4):
    g0: LineSegment StartX=16.8446 StartY=31.512 StartZ=0 EndX=16.3251 EndY=34.4666 EndZ=0
    g1: ArcOfCircle CenterX=19 CenterY=19.2524 CenterZ=0 NormalX=0 NormalY=0 NormalZ=1 AngleXU=0 Radius=15.4476 StartAngle=1.74483 EndAngle=2.72717
    g2: ArcOfCircle CenterX=19 CenterY=19.2524 CenterZ=0 NormalX=0 NormalY=0 NormalZ=1 AngleXU=0 Radius=12.4476 StartAngle=1.74483 EndAngle=2.73189
    g3: LineSegment StartX=4.86004 StartY=25.4725 StartZ=0 EndX=7.58253 EndY=24.2107 EndZ=0
  constraints (7):
    c: Block(g0)
    c: Coincident(g1,g0)
    c: Coincident(g2,g0)
    c: Coincident(g3,g1)
    c: Coincident(g3,g2)
    c: Block(g1)
    c: Block(g2)
FEATURE [Part::Extrusion] Extrude008
  Base = -> Sketch009
  Dir = (0,0,1)
  DirMode = 2
  FaceMakerClass = Part::FaceMakerBullseye
  LengthFwd = 10
  LengthRev = 0
  Placement = pos=(0,0,31) rot=(0,0,1;0rad)
  Solid = true
  Symmetric = false
FEATURE [Part::Cylinder] Cylinder020
  Angle = 360
  AttacherType = Attacher::AttachEngine3D
  Height = 20
  Placement = pos=(0,0,36.15) rot=(0,0,1;0rad)
  Radius = 8.2
FEATURE [Part::Cylinder] Cylinder021
  Angle = 360
  AttacherType = Attacher::AttachEngine3D
  Height = 10
  Placement = pos=(0,0,36.15) rot=(0,0,1;0rad)
  Radius = 4
FEATURE [Part::MultiFuse] Fusion038  label="removeToCreteHoleForPlugHousing007"
  Placement = pos=(-42,19,36) rot=(0,1,0;1.5708rad)
  Shapes = -> [Cylinder020,Cylinder021]
FEATURE [Part::Cut] Cut011
  Base = -> Extrude008
  Tool = -> Fusion038
FEATURE [Part::Fillet] Fillet011
  Base = -> Cut011
  Edges = 1 edges r=2: [Edge1]
FEATURE [Part::Fillet] Fillet012
  Base = -> Fillet011
  Edges = 1 edges r=2.5: [Edge1]
FEATURE [Part::Fillet] Fillet013
  Base = -> Fillet012
  Edges = 1 edges r=2.5: [Edge2]
FEATURE [Part::Box] Box010  label="Cube010"
  AttacherType = Attacher::AttachEngine3D
  Height = 16
  Length = 8
  Placement = pos=(12.7,31.52,28) rot=(0,0,1;0rad)
  Width = 4
FEATURE [Sketcher::SketchObject] Sketch010  label="topSketch004"
  FullyConstrained = true
  sketch-geometry (4):
    g0: LineSegment StartX=16.8446 StartY=31.512 StartZ=0 EndX=16.3251 EndY=34.4666 EndZ=0
    g1: ArcOfCircle CenterX=19 CenterY=19.2524 CenterZ=0 NormalX=0 NormalY=0 NormalZ=1 AngleXU=0 Radius=15.4476 StartAngle=1.74483 EndAngle=2.72717
    g2: ArcOfCircle CenterX=19 CenterY=19.2524 CenterZ=0 NormalX=0 NormalY=0 NormalZ=1 AngleXU=0 Radius=12.4476 StartAngle=1.74483 EndAngle=2.73189
    g3: LineSegment StartX=4.86004 StartY=25.4725 StartZ=0 EndX=7.58253 EndY=24.2107 EndZ=0
  constraints (7):
    c: Block(g0)
    c: Coincident(g1,g0)
    c: Coincident(g2,g0)
    c: Coincident(g3,g1)
    c: Coincident(g3,g2)
    c: Block(g1)
    c: Block(g2)
FEATURE [Part::Cylinder] Cylinder022
  Angle = 360
  AttacherType = Attacher::AttachEngine3D
  Height = 10
  Placement = pos=(0,0,36.15) rot=(0,0,1;0rad)
  Radius = 4
FEATURE [Sketcher::SketchObject] Sketch011  label="topSketch005"
  FullyConstrained = true
  sketch-geometry (4):
    g0: LineSegment StartX=16.8446 StartY=31.512 StartZ=0 EndX=16.3251 EndY=34.4666 EndZ=0
    g1: ArcOfCircle CenterX=19 CenterY=19.2524 CenterZ=0 NormalX=0 NormalY=0 NormalZ=1 AngleXU=0 Radius=15.4476 StartAngle=1.74483 EndAngle=2.72717
    g2: ArcOfCircle CenterX=19 CenterY=19.2524 CenterZ=0 NormalX=0 NormalY=0 NormalZ=1 AngleXU=0 Radius=12.4476 StartAngle=1.74483 EndAngle=2.73189
    g3: LineSegment StartX=4.86004 StartY=25.4725 StartZ=0 EndX=7.58253 EndY=24.2107 EndZ=0
  constraints (7):
    c: Block(g0)
    c: Coincident(g1,g0)
    c: Coincident(g2,g0)
    c: Coincident(g3,g1)
    c: Coincident(g3,g2)
    c: Block(g1)
    c: Block(g2)
FEATURE [Part::Extrusion] Extrude010
  Base = -> Sketch011
  Dir = (0,0,1)
  DirMode = 2
  FaceMakerClass = Part::FaceMakerBullseye
  LengthFwd = 10.6
  LengthRev = 0
  Placement = pos=(0,0,31) rot=(0,0,1;0rad)
  Solid = true
  Symmetric = false
FEATURE [Part::Cylinder] Cylinder023
  Angle = 360
  AttacherType = Attacher::AttachEngine3D
  Height = 20
  Placement = pos=(0,0,36.15) rot=(0,0,1;0rad)
  Radius = 8.2
FEATURE [Part::MultiFuse] Fusion039  label="removeToCreteHoleForPlugHousing008"
  Placement = pos=(-42,19,36) rot=(0,1,0;1.5708rad)
  Shapes = -> [Cylinder023,Cylinder022]
FEATURE [Part::Cut] Cut012
  Base = -> Extrude010
  Placement = pos=(0,0,-0.3) rot=(0,0,1;0rad)
  Tool = -> Fusion039
FEATURE [Part::Cut] Cut013
  Base = -> Box010
  Tool = -> Cut012
FEATURE [Part::Fillet] Fillet014
  Base = -> Cut013
  Edges = 1 edges r=0.7: [Edge13]
FEATURE [Part::Fillet] Fillet015
  Base = -> Fillet014
  Edges = 1 edges r=0.7: [Edge13]
FEATURE [Part::Fillet] Fillet016
  Base = -> Fillet015
  Edges = 1 edges r=0.7: [Edge16]
FEATURE [Part::Fillet] Fillet017
  Base = -> Fillet016
  Edges = 1 edges r=0.7: [Edge11]
FEATURE [Part::Fillet] Fillet018
  Base = -> Fillet017
  Edges = 1 edges r=0.7: [Edge10]
FEATURE [Part::Fillet] Fillet019
  Base = -> Fillet018
  Edges = 1 edges r=1.2: [Edge5]
FEATURE [Part::Fillet] Fillet020
  Base = -> Fillet019
  Edges = 1 edges r=1.2: [Edge12]
FEATURE [Part::Fillet] Fillet021
  Base = -> Fillet020
  Edges = 1 edges r=2: [Edge1]
  Placement = pos=(0.3,0,0) rot=(0,0,1;0rad)
FEATURE [Part::MultiFuse] Fusion040  label="top005"
  Shapes = -> [Cut008,Fillet021]
FEATURE [Part::MultiFuse] Fusion041  label="wireHolder"
  Shapes = -> [Fusion033,Fillet013]
FEATURE [Part::MultiFuse] Fusion042
  Shapes = -> [Fillet007,Fusion041]
FEATURE [Part::MultiFuse] Fusion043  label="wireHolder001"
  Shapes = -> [Fusion042,Fillet010]
FEATURE [Part::MultiFuse] Fusion044  label="wireHolder002"
  Shapes = -> [Fillet006,Fusion037,Fusion043]
FEATURE [Part::Feature] Face026
  shape: bbox 11 x 6 x 2e-07 mm, 1 faces, 0 solids (baked)
FEATURE [Part::Revolution] Revolve026
  Angle = 360
  Axis = (0,1,0)
  Base = (0,0,0)
  FaceMakerClass = Part::FaceMakerBullseye
  Placement = pos=(30.3,-1,19.7) rot=(0,0,1;0rad)
  Solid = false
  Source = -> Face026
  Symmetric = false
FEATURE [Sketcher::SketchObject] Sketch013  label="topSketch006"
  FullyConstrained = true
  sketch-geometry (13):
    g0: LineSegment StartX=117 StartY=19 StartZ=0 EndX=117 EndY=38 EndZ=0
    g1: ArcOfCircle CenterX=98 CenterY=19 CenterZ=0 NormalX=0 NormalY=0 NormalZ=1 AngleXU=0 Radius=19 StartAngle=5.7297 EndAngle=6.28319
    g2: LineSegment StartX=0 StartY=3 StartZ=0 EndX=0 EndY=19 EndZ=0
    g3: LineSegment StartX=19 StartY=38 StartZ=0 EndX=117 EndY=38 EndZ=0
    g4: ArcOfCircle CenterX=19 CenterY=19 CenterZ=0 NormalX=0 NormalY=0 NormalZ=1 AngleXU=0 Radius=19 StartAngle=1.5708 EndAngle=3.14159
    g5: ArcOfCircle CenterX=19 CenterY=19 CenterZ=0 NormalX=0 NormalY=0 NormalZ=1 AngleXU=0 Radius=16 StartAngle=1.5708 EndAngle=3.14159
    g6: ArcOfCircle CenterX=98 CenterY=19 CenterZ=0 NormalX=0 NormalY=0 NormalZ=1 AngleXU=0 Radius=16 StartAngle=5.60905 EndAngle=6.28319
    g7: LineSegment StartX=114 StartY=19 StartZ=0 EndX=114 EndY=35 EndZ=0
    g8: LineSegment StartX=110.5 StartY=9.01251 StartZ=0 EndX=114.163 EndY=9.01251 EndZ=0
    g9: LineSegment StartX=114 StartY=35 StartZ=0 EndX=19 EndY=35 EndZ=0
    g10: LineSegment StartX=0 StartY=3 StartZ=0 EndX=0 EndY=0 EndZ=0
    g11: LineSegment StartX=3 StartY=0 StartZ=0 EndX=0 EndY=0 EndZ=0
    g12: LineSegment StartX=3 StartY=19 StartZ=0 EndX=3 EndY=0 EndZ=0
  constraints (33):
    c: Vertical(g0)
    c: Distance(g0) = 19
    c: Block(g0)
    c: Coincident(g1,g0)
    c: Block(g1)
    c: Vertical(g2)
    c: Block(g2)
    c: Coincident(g3,g0)
    c: Horizontal(g3)
    c: Distance(g3) = 98
    c: Coincident(g4,g3)
    c: Coincident(g4,g2)
    c: Block(g4)
    c: Coincident(g5,g4)
    c: Coincident(g6,g1)
    c: Block(g6)
    c: Block(g5)
    c: Coincident(g7,g6)
    c: Vertical(g7)
    c: Coincident(g8,g6)
    c: Coincident(g8,g1)
    c: Coincident(g9,g7)
    c: Coincident(g9,g5)
    c: Horizontal(g9)
    c: Tangent(g9,g5)
    c: Coincident(g10,g2)
    c: Distance(g10) = 3
    c: Vertical(g10)
    c: Coincident(g11,g10)
    c: Horizontal(g11)
    c: Coincident(g12,g5)
    c: Coincident(g12,g11)
    c: Vertical(g12)
FEATURE [Part::Extrusion] Extrude011  label="top006"
  Base = -> Sketch013
  Dir = (0,0,1)
  DirMode = 2
  FaceMakerClass = Part::FaceMakerBullseye
  LengthFwd = 72
  LengthRev = 0
  Solid = true
  Symmetric = false
FEATURE [Sketcher::SketchObject] Sketch014
  FullyConstrained = true
  MapMode = 3
  Placement = pos=(0,0,0) rot=(1,0,0;1.5708rad)
  Support = -> [Extrude011]
  sketch-geometry (8):
    g0: Circle CenterX=80.351 CenterY=-67.6202 CenterZ=0 NormalX=0 NormalY=0 NormalZ=1 AngleXU=0 Radius=2
    g1: Circle CenterX=80.351 CenterY=-67.6202 CenterZ=0 NormalX=0 NormalY=0 NormalZ=1 AngleXU=0 Radius=3
    g2: Circle CenterX=80.351 CenterY=-4.92017 CenterZ=0 NormalX=0 NormalY=0 NormalZ=1 AngleXU=0 Radius=2
    g3: Circle CenterX=80.351 CenterY=-4.92017 CenterZ=0 NormalX=0 NormalY=0 NormalZ=1 AngleXU=0 Radius=3
    g4: Circle CenterX=23.851 CenterY=-4.92017 CenterZ=0 NormalX=0 NormalY=0 NormalZ=1 AngleXU=0 Radius=2
    g5: Circle CenterX=23.851 CenterY=-4.92017 CenterZ=0 NormalX=0 NormalY=0 NormalZ=1 AngleXU=0 Radius=3
    g6: Circle CenterX=23.851 CenterY=-67.6202 CenterZ=0 NormalX=0 NormalY=0 NormalZ=1 AngleXU=0 Radius=2
    g7: Circle CenterX=23.851 CenterY=-67.6202 CenterZ=0 NormalX=0 NormalY=0 NormalZ=1 AngleXU=0 Radius=3
  constraints (8):
    c: Block(g3)
    c: Block(g2)
    c: Block(g1)
    c: Block(g0)
    c: Block(g6)
    c: Block(g7)
    c: Block(g4)
    c: Block(g5)
FEATURE [Part::Feature] Face027
  shape: bbox 11 x 6 x 2e-07 mm, 1 faces, 0 solids (baked)
FEATURE [Part::Revolution] Revolve027
  Angle = 360
  Axis = (0,1,0)
  Base = (0,0,0)
  FaceMakerClass = Part::FaceMakerBullseye
  Placement = pos=(30.3,-1,51.7) rot=(0,0,1;0rad)
  Solid = false
  Source = -> Face027
  Symmetric = false
FEATURE [Part::Feature] Face028
  shape: bbox 11 x 6 x 2e-07 mm, 1 faces, 0 solids (baked)
FEATURE [Part::Revolution] Revolve028
  Angle = 360
  Axis = (0,1,0)
  Base = (0,0,0)
  FaceMakerClass = Part::FaceMakerBullseye
  Placement = pos=(62.3,-1,19.7) rot=(0,0,1;0rad)
  Solid = false
  Source = -> Face028
  Symmetric = false
FEATURE [Part::Feature] Face029
  shape: bbox 11 x 6 x 2e-07 mm, 1 faces, 0 solids (baked)
FEATURE [Part::Revolution] Revolve029
  Angle = 360
  Axis = (0,1,0)
  Base = (0,0,0)
  FaceMakerClass = Part::FaceMakerBullseye
  Placement = pos=(62.3,-1,51.7) rot=(0,0,1;0rad)
  Solid = false
  Source = -> Face029
  Symmetric = false
FEATURE [Part::Feature] Wire
  shape: bbox 11 x 5.2 x 2e-07 mm, 0 faces, 0 solids (baked)
FEATURE [Part::Revolution] Revolve030
  Angle = 360
  Axis = (0,1,0)
  Base = (0,0,0)
  FaceMakerClass = Part::FaceMakerBullseye
  Placement = pos=(30.3,38,19.7) rot=(0,0,1;0rad)
  Solid = true
  Source = -> Wire
  Symmetric = false
FEATURE [Part::Feature] Wire001
  shape: bbox 11 x 5.2 x 2e-07 mm, 0 faces, 0 solids (baked)
FEATURE [Part::Revolution] Revolve031
  Angle = 360
  Axis = (0,1,0)
  Base = (0,0,0)
  FaceMakerClass = Part::FaceMakerBullseye
  Placement = pos=(30.3,38,51.7) rot=(0,0,1;0rad)
  Solid = true
  Source = -> Wire001
  Symmetric = false
FEATURE [Part::Feature] Wire002
  shape: bbox 11 x 5.2 x 2e-07 mm, 0 faces, 0 solids (baked)
FEATURE [Part::Revolution] Revolve032
  Angle = 360
  Axis = (0,1,0)
  Base = (0,0,0)
  FaceMakerClass = Part::FaceMakerBullseye
  Placement = pos=(62.3,38,51.7) rot=(0,0,1;0rad)
  Solid = true
  Source = -> Wire002
  Symmetric = false
FEATURE [Part::Feature] Wire003
  shape: bbox 11 x 5.2 x 2e-07 mm, 0 faces, 0 solids (baked)
FEATURE [Part::Revolution] Revolve033
  Angle = 360
  Axis = (0,1,0)
  Base = (0,0,0)
  FaceMakerClass = Part::FaceMakerBullseye
  Placement = pos=(62.3,38,19.7) rot=(0,0,1;0rad)
  Solid = true
  Source = -> Wire003
  Symmetric = false
FEATURE [Part::MultiFuse] Fusion045  label="altRandScrewHousing"
  Shapes = -> [Revolve029,Revolve027,Revolve028,Revolve026]
FEATURE [Part::MultiFuse] Fusion046  label="fanScrewHousing"
  Shapes = -> [Revolve033,Revolve032,Revolve031,Revolve030]
FEATURE [Sketcher::SketchObject] Sketch015
  FullyConstrained = true
  sketch-geometry (17):
    g0: Circle CenterX=-3.5 CenterY=23.5 CenterZ=0 NormalX=0 NormalY=0 NormalZ=1 AngleXU=0 Radius=1
    g1: Circle CenterX=-1 CenterY=15.25 CenterZ=0 NormalX=0 NormalY=0 NormalZ=1 AngleXU=0 Radius=1
    g2: Circle CenterX=-3.5 CenterY=7 CenterZ=0 NormalX=0 NormalY=0 NormalZ=1 AngleXU=0 Radius=1
    g3: BSplineCurve PolesCount=3 KnotsCount=2 Degree=2 IsPeriodic=0
    g4: GeomPoint X=-3.5 Y=23.5 Z=0
    g5: GeomPoint X=-3.5 Y=7 Z=0
    g6: Circle CenterX=-4.8 CenterY=30.5 CenterZ=0 NormalX=0 NormalY=0 NormalZ=1 AngleXU=0 Radius=1
    g7: Circle CenterX=-3.5 CenterY=30.5 CenterZ=0 NormalX=0 NormalY=0 NormalZ=1 AngleXU=0 Radius=1
    g8: Circle CenterX=-3.5 CenterY=29.2 CenterZ=0 NormalX=0 NormalY=0 NormalZ=1 AngleXU=0 Radius=1
    g9: BSplineCurve PolesCount=3 KnotsCount=2 Degree=2 IsPeriodic=0
    g10: GeomPoint X=-4.8 Y=30.5 Z=0
    g11: GeomPoint X=-3.5 Y=29.2 Z=0
    g12: LineSegment StartX=-3.5 StartY=29.2 StartZ=0 EndX=-3.5 EndY=23.5 EndZ=0
    g13: LineSegment StartX=-4.8 StartY=30.5 StartZ=0 EndX=0 EndY=30.5 EndZ=0
    g14: LineSegment StartX=-3.5 StartY=0.3 StartZ=0 EndX=0 EndY=0.3 EndZ=0
    g15: LineSegment StartX=-3.5 StartY=0.3 StartZ=0 EndX=-3.5 EndY=7 EndZ=0
    g16: LineSegment StartX=0 StartY=0.3 StartZ=0 EndX=0 EndY=30.5 EndZ=0
  constraints (33):
    c: Weight(g0) = 1
    c: Equal(g0,g1)
    c: Equal(g0,g2)
    c: InternalAlignment(g0,g3)
    c: InternalAlignment(g1,g3)
    c: InternalAlignment(g2,g3)
    c: InternalAlignment(g4,g3)
    c: InternalAlignment(g5,g3)
    c: Block(g3)
    c: Weight(g6) = 1
    c: Equal(g6,g7)
    c: Equal(g6,g8)
    c: InternalAlignment(g6,g9)
    c: InternalAlignment(g7,g9)
    c: InternalAlignment(g8,g9)
    c: InternalAlignment(g10,g9)
    c: InternalAlignment(g11,g9)
    c: Block(g9)
    c: Coincident(g12,g9)
    c: Coincident(g12,g3)
    c: Vertical(g12)
    c: Coincident(g13,g9)
    c: Horizontal(g13)
    c: Distance(g13) = 4.8
    c: Horizontal(g14)
    c: Block(g14)
    c: Coincident(g15,g14)
    c: Coincident(g15,g3)
    c: Vertical(g15)
    c: Coincident(g16,g14)
    c: Coincident(g16,g13)
    c: Vertical(g16)
    c: Tangent(g16,g1)
FEATURE [Sketcher::SketchObject] Sketch016
  FullyConstrained = true
  sketch-geometry (16):
    g0: Circle CenterX=-3.5 CenterY=23.5 CenterZ=0 NormalX=0 NormalY=0 NormalZ=1 AngleXU=0 Radius=1
    g1: Circle CenterX=-1 CenterY=15.25 CenterZ=0 NormalX=0 NormalY=0 NormalZ=1 AngleXU=0 Radius=1
    g2: Circle CenterX=-3.5 CenterY=7 CenterZ=0 NormalX=0 NormalY=0 NormalZ=1 AngleXU=0 Radius=1
    g3: BSplineCurve PolesCount=3 KnotsCount=2 Degree=2 IsPeriodic=0
    g4: GeomPoint X=-3.5 Y=23.5 Z=0
    g5: GeomPoint X=-3.5 Y=7 Z=0
    g6: LineSegment StartX=-3.5 StartY=28.2 StartZ=0 EndX=-3.5 EndY=23.5 EndZ=0
    g7: LineSegment StartX=0 StartY=29.5 StartZ=0 EndX=0 EndY=30 EndZ=0
    g8: LineSegment StartX=-3.5 StartY=28.2 StartZ=0 EndX=-3.5 EndY=30 EndZ=0
    g9: LineSegment StartX=0 StartY=30 StartZ=0 EndX=0 EndY=30.5 EndZ=0
    g10: LineSegment StartX=0 StartY=30.5 StartZ=0 EndX=-3.5 EndY=30.5 EndZ=0
    g11: LineSegment StartX=-3.5 StartY=30.5 StartZ=0 EndX=-3.5 EndY=30 EndZ=0
    g12: LineSegment StartX=0 StartY=29.5 StartZ=0 EndX=0 EndY=5 EndZ=0
    g13: LineSegment StartX=-3.5 StartY=0.3 StartZ=0 EndX=-3.5 EndY=7 EndZ=0
    g14: LineSegment StartX=-3.5 StartY=0.3 StartZ=0 EndX=0 EndY=0.3 EndZ=0
    g15: LineSegment StartX=0 StartY=5 StartZ=0 EndX=0 EndY=0.3 EndZ=0
  constraints (39):
    c: Weight(g0) = 1
    c: Equal(g0,g1)
    c: Equal(g0,g2)
    c: InternalAlignment(g0,g3)
    c: InternalAlignment(g1,g3)
    c: InternalAlignment(g2,g3)
    c: InternalAlignment(g4,g3)
    c: InternalAlignment(g5,g3)
    c: Block(g3)
    c: Coincident(g6,g3)
    c: Vertical(g6)
    c: Vertical(g7)
    c: Distance(g7) = 0.5
    c: Coincident(g8,g6)
    c: Vertical(g8)
    c: Block(g6)
    c: Block(g7)
    c: Vertical(g9)
    c: Equal(g7,g9) = 0.5
    c: Block(g9)
    c: Coincident(g9,g7)
    c: Horizontal(g10)
    c: Coincident(g10,g9)
    c: Coincident(g11,g10)
    c: Coincident(g11,g8)
    c: Vertical(g11)
    c: Block(g11)
    c: Coincident(g12,g7)
    c: Vertical(g12)
    c: Coincident(g13,g3)
    c: Vertical(g13)
    c: Distance(g13) = 6.7
    c: Coincident(g14,g13)
    c: Horizontal(g14)
    c: Block(g14)
    c: Coincident(g15,g12)
    c: Coincident(g15,g14)
    c: Vertical(g15)
    c: Block(g15)
FEATURE [Sketcher::SketchObject] Sketch017
  FullyConstrained = true
  sketch-geometry (11):
    g0: LineSegment StartX=-3.5 StartY=1e-16 StartZ=0 EndX=-1.6 EndY=1e-16 EndZ=0
    g1: LineSegment StartX=-1.6 StartY=1e-16 StartZ=0 EndX=-1.6 EndY=1.5 EndZ=0
    g2: LineSegment StartX=-3.5 StartY=1.5 StartZ=0 EndX=-1.6 EndY=1.5 EndZ=0
    g3: LineSegment StartX=-3.5 StartY=1e-16 StartZ=0 EndX=-4.8 EndY=1e-16 EndZ=0
    g4: Circle CenterX=-3.5 CenterY=1.3 CenterZ=0 NormalX=0 NormalY=0 NormalZ=1 AngleXU=0 Radius=1
    g5: Circle CenterX=-3.5 CenterY=1e-16 CenterZ=0 NormalX=0 NormalY=0 NormalZ=1 AngleXU=0 Radius=1
    g6: Circle CenterX=-4.8 CenterY=1e-16 CenterZ=0 NormalX=0 NormalY=0 NormalZ=1 AngleXU=0 Radius=1
    g7: BSplineCurve PolesCount=3 KnotsCount=2 Degree=2 IsPeriodic=0
    g8: GeomPoint X=-3.5 Y=1.3 Z=0
    g9: GeomPoint X=-4.8 Y=1e-16 Z=0
    g10: LineSegment StartX=-3.5 StartY=1.3 StartZ=0 EndX=-3.5 EndY=1.5 EndZ=0
  constraints (24):
    c: Horizontal(g0)
    c: Distance(g0) = 1.9
    c: Block(g0)
    c: Coincident(g1,g0)
    c: Vertical(g1)
    c: Coincident(g2,g1)
    c: Horizontal(g2)
    c: Coincident(g3,g0)
    c: Horizontal(g3)
    c: Distance(g3) = 1.3
    c: Weight(g4) = 1
    c: Equal(g4,g5)
    c: Coincident(g5,g0)
    c: Equal(g4,g6)
    c: Coincident(g7,g3)
    c: InternalAlignment(g4,g7)
    c: InternalAlignment(g5,g7)
    c: InternalAlignment(g6,g7)
    c: InternalAlignment(g8,g7)
    c: InternalAlignment(g9,g7)
    c: Coincident(g10,g7)
    c: Coincident(g10,g2)
    c: Vertical(g10)
    c: Block(g10)
FEATURE [Part::Feature] Face035
  shape: bbox 3.2 x 1.5 x 2e-07 mm, 1 faces, 0 solids (baked)
FEATURE [Part::Revolution] Revolve039  label="backCaseScrewRetainer"
  Angle = 360
  Axis = (0,1,0)
  Base = (0,0,0)
  FaceMakerClass = Part::FaceMakerBullseye
  Placement = pos=(12.5,3,62) rot=(0,0,1;0rad)
  Solid = false
  Source = -> Face035
  Symmetric = false
FEATURE [Part::Feature] Face036
  shape: bbox 3.2 x 1.5 x 2e-07 mm, 1 faces, 0 solids (baked)
FEATURE [Part::Feature] Face039
  shape: bbox 4.8 x 30.2 x 2e-07 mm, 1 faces, 0 solids (baked)
FEATURE [Part::Revolution] Revolve043  label="frontCaseScrewPost002"
  Angle = 360
  Axis = (0,1,0)
  Base = (0,0,0)
  FaceMakerClass = Part::FaceMakerBullseye
  Placement = pos=(89.5,4.5,3.5) rot=(0,0,1;0rad)
  Solid = false
  Source = -> Face039
  Symmetric = false
FEATURE [Part::Feature] Face042
  shape: bbox 4.8 x 30.2 x 2e-07 mm, 1 faces, 0 solids (baked)
FEATURE [Part::Revolution] Revolve046  label="frontCaseScrewPost003"
  Angle = 360
  Axis = (0,1,0)
  Base = (0,0,0)
  FaceMakerClass = Part::FaceMakerBullseye
  Placement = pos=(89.5,4.5,68.5) rot=(0,0,1;0rad)
  Solid = false
  Source = -> Face042
  Symmetric = false
FEATURE [Part::Feature] Face043
  shape: bbox 3.2 x 1.5 x 2e-07 mm, 1 faces, 0 solids (baked)
FEATURE [Part::Revolution] Revolve047  label="frontCaseScrewRetainer002"
  Angle = 360
  Axis = (0,1,0)
  Base = (0,0,0)
  FaceMakerClass = Part::FaceMakerBullseye
  Placement = pos=(89.5,3,68.5) rot=(0,0,1;0rad)
  Solid = false
  Source = -> Face043
  Symmetric = false
FEATURE [Part::Feature] Face044
  shape: bbox 3.2 x 1.5 x 2e-07 mm, 1 faces, 0 solids (baked)
FEATURE [Part::Revolution] Revolve048  label="frontCaseScrewRetainer003"
  Angle = 360
  Axis = (0,1,0)
  Base = (0,0,0)
  FaceMakerClass = Part::FaceMakerBullseye
  Placement = pos=(89.5,3,3.5) rot=(0,0,1;0rad)
  Solid = false
  Source = -> Face044
  Symmetric = false
FEATURE [App::MeasureDistance] Distance002  label="Distance: 1.67 mm"
  Distance = 1.66921
  P1 = (99.2361,4.7524,71.7)
  P2 = (99.2347,6.42161,71.7)
FEATURE [Sketcher::SketchObject] Sketch018
  FullyConstrained = true
  sketch-geometry (7):
    g0: LineSegment StartX=0 StartY=0 StartZ=0 EndX=0 EndY=6 EndZ=0
    g1: Circle CenterX=0 CenterY=0 CenterZ=0 NormalX=0 NormalY=0 NormalZ=1 AngleXU=0 Radius=1
    g2: Circle CenterX=8 CenterY=6 CenterZ=0 NormalX=0 NormalY=0 NormalZ=1 AngleXU=0 Radius=1
    g3: BSplineCurve PolesCount=3 KnotsCount=2 Degree=2 IsPeriodic=0
    g4: GeomPoint X=0 Y=0 Z=0
    g5: GeomPoint X=8 Y=6 Z=0
    g6: LineSegment StartX=0 StartY=6 StartZ=0 EndX=8 EndY=6 EndZ=0
  constraints (14):
    c: Coincident(g0,g-1)
    c: Distance(g0) = 6
    c: Vertical(g0)
    c: Coincident(g3,g0)
    c: Weight(g1) = 1
    c: Equal(g1,g2)
    c: InternalAlignment(g1,g3)
    c: InternalAlignment(g2,g3)
    c: InternalAlignment(g4,g3)
    c: InternalAlignment(g5,g3)
    c: Block(g3)
    c: Coincident(g6,g0)
    c: Coincident(g6,g3)
    c: Horizontal(g6)
FEATURE [Part::Extrusion] Extrude012  label="caseScrewPillarBracket"
  Base = -> Sketch018
  Dir = (0,0,1)
  DirMode = 2
  FaceMakerClass = Part::FaceMakerBullseye
  LengthFwd = 2.4
  LengthRev = 0
  Placement = pos=(15.76,29,8.8) rot=(0,1,0;0rad)
  Solid = true
  Symmetric = false
FEATURE [Sketcher::SketchObject] Sketch019
  FullyConstrained = true
  sketch-geometry (7):
    g0: LineSegment StartX=0 StartY=0 StartZ=0 EndX=0 EndY=6 EndZ=0
    g1: Circle CenterX=0 CenterY=0 CenterZ=0 NormalX=0 NormalY=0 NormalZ=1 AngleXU=0 Radius=1
    g2: Circle CenterX=8 CenterY=6 CenterZ=0 NormalX=0 NormalY=0 NormalZ=1 AngleXU=0 Radius=1
    g3: BSplineCurve PolesCount=3 KnotsCount=2 Degree=2 IsPeriodic=0
    g4: GeomPoint X=0 Y=0 Z=0
    g5: GeomPoint X=8 Y=6 Z=0
    g6: LineSegment StartX=0 StartY=6 StartZ=0 EndX=8 EndY=6 EndZ=0
  constraints (14):
    c: Coincident(g0,g-1)
    c: Distance(g0) = 6
    c: Vertical(g0)
    c: Coincident(g3,g0)
    c: Weight(g1) = 1
    c: Equal(g1,g2)
    c: InternalAlignment(g1,g3)
    c: InternalAlignment(g2,g3)
    c: InternalAlignment(g4,g3)
    c: InternalAlignment(g5,g3)
    c: Block(g3)
    c: Coincident(g6,g0)
    c: Coincident(g6,g3)
    c: Horizontal(g6)
FEATURE [Part::Extrusion] Extrude013  label="caseScrewPillarBracket001"
  Base = -> Sketch019
  Dir = (0,0,1)
  DirMode = 2
  FaceMakerClass = Part::FaceMakerBullseye
  LengthFwd = 2.4
  LengthRev = 0
  Placement = pos=(15.76,29,60.8) rot=(0,0,1;0rad)
  Solid = true
  Symmetric = false
FEATURE [Sketcher::SketchObject] Sketch020
  FullyConstrained = true
  sketch-geometry (7):
    g0: LineSegment StartX=0 StartY=0 StartZ=0 EndX=0 EndY=6 EndZ=0
    g1: Circle CenterX=0 CenterY=0 CenterZ=0 NormalX=0 NormalY=0 NormalZ=1 AngleXU=0 Radius=1
    g2: Circle CenterX=8 CenterY=6 CenterZ=0 NormalX=0 NormalY=0 NormalZ=1 AngleXU=0 Radius=1
    g3: BSplineCurve PolesCount=3 KnotsCount=2 Degree=2 IsPeriodic=0
    g4: GeomPoint X=0 Y=0 Z=0
    g5: GeomPoint X=8 Y=6 Z=0
    g6: LineSegment StartX=0 StartY=6 StartZ=0 EndX=8 EndY=6 EndZ=0
  constraints (14):
    c: Coincident(g0,g-1)
    c: Distance(g0) = 6
    c: Vertical(g0)
    c: Coincident(g3,g0)
    c: Weight(g1) = 1
    c: Equal(g1,g2)
    c: InternalAlignment(g1,g3)
    c: InternalAlignment(g2,g3)
    c: InternalAlignment(g4,g3)
    c: InternalAlignment(g5,g3)
    c: Block(g3)
    c: Coincident(g6,g0)
    c: Coincident(g6,g3)
    c: Horizontal(g6)
FEATURE [Part::Extrusion] Extrude014  label="caseScrewPillarBracket002"
  Base = -> Sketch020
  Dir = (0,0,1)
  DirMode = 2
  FaceMakerClass = Part::FaceMakerBullseye
  LengthFwd = 2.4
  LengthRev = 0
  Placement = pos=(13.7,29,13.26) rot=(0,-1,0;1.5708rad)
  Solid = true
  Symmetric = false
FEATURE [Sketcher::SketchObject] Sketch021
  FullyConstrained = true
  sketch-geometry (7):
    g0: LineSegment StartX=0 StartY=0 StartZ=0 EndX=0 EndY=6 EndZ=0
    g1: Circle CenterX=0 CenterY=0 CenterZ=0 NormalX=0 NormalY=0 NormalZ=1 AngleXU=0 Radius=1
    g2: Circle CenterX=8 CenterY=6 CenterZ=0 NormalX=0 NormalY=0 NormalZ=1 AngleXU=0 Radius=1
    g3: BSplineCurve PolesCount=3 KnotsCount=2 Degree=2 IsPeriodic=0
    g4: GeomPoint X=0 Y=0 Z=0
    g5: GeomPoint X=8 Y=6 Z=0
    g6: LineSegment StartX=0 StartY=6 StartZ=0 EndX=8 EndY=6 EndZ=0
  constraints (14):
    c: Coincident(g0,g-1)
    c: Distance(g0) = 6
    c: Vertical(g0)
    c: Coincident(g3,g0)
    c: Weight(g1) = 1
    c: Equal(g1,g2)
    c: InternalAlignment(g1,g3)
    c: InternalAlignment(g2,g3)
    c: InternalAlignment(g4,g3)
    c: InternalAlignment(g5,g3)
    c: Block(g3)
    c: Coincident(g6,g0)
    c: Coincident(g6,g3)
    c: Horizontal(g6)
FEATURE [Part::Extrusion] Extrude015  label="caseScrewPillarBracket003"
  Base = -> Sketch021
  Dir = (0,0,1)
  DirMode = 2
  FaceMakerClass = Part::FaceMakerBullseye
  LengthFwd = 2.4
  LengthRev = 0
  Placement = pos=(11.3,29,58.74) rot=(0,1,0;1.5708rad)
  Solid = true
  Symmetric = false
FEATURE [Sketcher::SketchObject] Sketch022
  FullyConstrained = true
  sketch-geometry (7):
    g0: LineSegment StartX=0 StartY=0 StartZ=0 EndX=0 EndY=6 EndZ=0
    g1: Circle CenterX=0 CenterY=0 CenterZ=0 NormalX=0 NormalY=0 NormalZ=1 AngleXU=0 Radius=1
    g2: Circle CenterX=8 CenterY=6 CenterZ=0 NormalX=0 NormalY=0 NormalZ=1 AngleXU=0 Radius=1
    g3: BSplineCurve PolesCount=3 KnotsCount=2 Degree=2 IsPeriodic=0
    g4: GeomPoint X=0 Y=0 Z=0
    g5: GeomPoint X=8 Y=6 Z=0
    g6: LineSegment StartX=0 StartY=6 StartZ=0 EndX=8 EndY=6 EndZ=0
  constraints (14):
    c: Coincident(g0,g-1)
    c: Distance(g0) = 6
    c: Vertical(g0)
    c: Coincident(g3,g0)
    c: Weight(g1) = 1
    c: Equal(g1,g2)
    c: InternalAlignment(g1,g3)
    c: InternalAlignment(g2,g3)
    c: InternalAlignment(g4,g3)
    c: InternalAlignment(g5,g3)
    c: Block(g3)
    c: Coincident(g6,g0)
    c: Coincident(g6,g3)
    c: Horizontal(g6)
FEATURE [Part::Extrusion] Extrude016  label="caseScrewPillarBracket004"
  Base = -> Sketch022
  Dir = (0,0,1)
  DirMode = 2
  FaceMakerClass = Part::FaceMakerBullseye
  LengthFwd = 2.4
  LengthRev = 0
  Placement = pos=(88.3,29,65.23) rot=(0,1,0;1.5708rad)
  Solid = true
  Symmetric = false
FEATURE [Sketcher::SketchObject] Sketch023
  FullyConstrained = true
  sketch-geometry (7):
    g0: LineSegment StartX=0 StartY=0 StartZ=0 EndX=0 EndY=6 EndZ=0
    g1: Circle CenterX=0 CenterY=0 CenterZ=0 NormalX=0 NormalY=0 NormalZ=1 AngleXU=0 Radius=1
    g2: Circle CenterX=8 CenterY=6 CenterZ=0 NormalX=0 NormalY=0 NormalZ=1 AngleXU=0 Radius=1
    g3: BSplineCurve PolesCount=3 KnotsCount=2 Degree=2 IsPeriodic=0
    g4: GeomPoint X=0 Y=0 Z=0
    g5: GeomPoint X=8 Y=6 Z=0
    g6: LineSegment StartX=0 StartY=6 StartZ=0 EndX=8 EndY=6 EndZ=0
  constraints (14):
    c: Coincident(g0,g-1)
    c: Distance(g0) = 6
    c: Vertical(g0)
    c: Coincident(g3,g0)
    c: Weight(g1) = 1
    c: Equal(g1,g2)
    c: InternalAlignment(g1,g3)
    c: InternalAlignment(g2,g3)
    c: InternalAlignment(g4,g3)
    c: InternalAlignment(g5,g3)
    c: Block(g3)
    c: Coincident(g6,g0)
    c: Coincident(g6,g3)
    c: Horizontal(g6)
FEATURE [Part::Extrusion] Extrude017  label="caseScrewPillarBracket005"
  Base = -> Sketch023
  Dir = (0,0,1)
  DirMode = 2
  FaceMakerClass = Part::FaceMakerBullseye
  LengthFwd = 2.4
  LengthRev = 0
  Placement = pos=(90.7,29,6.77) rot=(0,-1,0;1.5708rad)
  Solid = true
  Symmetric = false
FEATURE [Sketcher::SketchObject] Sketch024
  FullyConstrained = true
  sketch-geometry (7):
    g0: LineSegment StartX=0 StartY=0 StartZ=0 EndX=0 EndY=6 EndZ=0
    g1: Circle CenterX=0 CenterY=0 CenterZ=0 NormalX=0 NormalY=0 NormalZ=1 AngleXU=0 Radius=1
    g2: Circle CenterX=8 CenterY=6 CenterZ=0 NormalX=0 NormalY=0 NormalZ=1 AngleXU=0 Radius=1
    g3: BSplineCurve PolesCount=3 KnotsCount=2 Degree=2 IsPeriodic=0
    g4: GeomPoint X=0 Y=0 Z=0
    g5: GeomPoint X=8 Y=6 Z=0
    g6: LineSegment StartX=0 StartY=6 StartZ=0 EndX=8 EndY=6 EndZ=0
  constraints (14):
    c: Coincident(g0,g-1)
    c: Distance(g0) = 6
    c: Vertical(g0)
    c: Coincident(g3,g0)
    c: Weight(g1) = 1
    c: Equal(g1,g2)
    c: InternalAlignment(g1,g3)
    c: InternalAlignment(g2,g3)
    c: InternalAlignment(g4,g3)
    c: InternalAlignment(g5,g3)
    c: Block(g3)
    c: Coincident(g6,g0)
    c: Coincident(g6,g3)
    c: Horizontal(g6)
FEATURE [Part::Extrusion] Extrude018  label="caseScrewPillarBracket006"
  Base = -> Sketch024
  Dir = (0,0,1)
  DirMode = 2
  FaceMakerClass = Part::FaceMakerBullseye
  LengthFwd = 2.4
  LengthRev = 0
  Placement = pos=(103.7,29,6.77) rot=(0,-1,0;1.5708rad)
  Solid = true
  Symmetric = false
FEATURE [Sketcher::SketchObject] Sketch025
  FullyConstrained = true
  sketch-geometry (7):
    g0: LineSegment StartX=0 StartY=0 StartZ=0 EndX=0 EndY=6 EndZ=0
    g1: Circle CenterX=0 CenterY=0 CenterZ=0 NormalX=0 NormalY=0 NormalZ=1 AngleXU=0 Radius=1
    g2: Circle CenterX=8 CenterY=6 CenterZ=0 NormalX=0 NormalY=0 NormalZ=1 AngleXU=0 Radius=1
    g3: BSplineCurve PolesCount=3 KnotsCount=2 Degree=2 IsPeriodic=0
    g4: GeomPoint X=0 Y=0 Z=0
    g5: GeomPoint X=8 Y=6 Z=0
    g6: LineSegment StartX=0 StartY=6 StartZ=0 EndX=8 EndY=6 EndZ=0
  constraints (14):
    c: Coincident(g0,g-1)
    c: Distance(g0) = 6
    c: Vertical(g0)
    c: Coincident(g3,g0)
    c: Weight(g1) = 1
    c: Equal(g1,g2)
    c: InternalAlignment(g1,g3)
    c: InternalAlignment(g2,g3)
    c: InternalAlignment(g4,g3)
    c: InternalAlignment(g5,g3)
    c: Block(g3)
    c: Coincident(g6,g0)
    c: Coincident(g6,g3)
    c: Horizontal(g6)
FEATURE [Part::Extrusion] Extrude019  label="caseScrewPillarBracket007"
  Base = -> Sketch025
  Dir = (0,0,1)
  DirMode = 2
  FaceMakerClass = Part::FaceMakerBullseye
  LengthFwd = 2.4
  LengthRev = 0
  Placement = pos=(101.3,29,65.23) rot=(0,1,0;1.5708rad)
  Solid = true
  Symmetric = false
FEATURE [Part::Box] Box011  label="frontCaseScrewPillarBracket"
  AttacherType = Attacher::AttachEngine3D
  Height = 2.4
  Length = 16
  Placement = pos=(87,28,2.3) rot=(0,0,1;0rad)
  Width = 7
FEATURE [Part::Box] Box012  label="frontCaseScrewPillarBracket001"
  AttacherType = Attacher::AttachEngine3D
  Height = 2.4
  Length = 16
  Placement = pos=(87,28,67.3) rot=(0,0,1;0rad)
  Width = 7
FEATURE [Sketcher::SketchObject] Sketch026
  FullyConstrained = true
  sketch-geometry (17):
    g0: Circle CenterX=-3.5 CenterY=23.5 CenterZ=0 NormalX=0 NormalY=0 NormalZ=1 AngleXU=0 Radius=1
    g1: Circle CenterX=-1 CenterY=15.25 CenterZ=0 NormalX=0 NormalY=0 NormalZ=1 AngleXU=0 Radius=1
    g2: Circle CenterX=-3.5 CenterY=7 CenterZ=0 NormalX=0 NormalY=0 NormalZ=1 AngleXU=0 Radius=1
    g3: BSplineCurve PolesCount=3 KnotsCount=2 Degree=2 IsPeriodic=0
    g4: GeomPoint X=-3.5 Y=23.5 Z=0
    g5: GeomPoint X=-3.5 Y=7 Z=0
    g6: Circle CenterX=-4.8 CenterY=30.5 CenterZ=0 NormalX=0 NormalY=0 NormalZ=1 AngleXU=0 Radius=1
    g7: Circle CenterX=-3.5 CenterY=30.5 CenterZ=0 NormalX=0 NormalY=0 NormalZ=1 AngleXU=0 Radius=1
    g8: Circle CenterX=-3.5 CenterY=29.2 CenterZ=0 NormalX=0 NormalY=0 NormalZ=1 AngleXU=0 Radius=1
    g9: BSplineCurve PolesCount=3 KnotsCount=2 Degree=2 IsPeriodic=0
    g10: GeomPoint X=-4.8 Y=30.5 Z=0
    g11: GeomPoint X=-3.5 Y=29.2 Z=0
    g12: LineSegment StartX=-3.5 StartY=29.2 StartZ=0 EndX=-3.5 EndY=23.5 EndZ=0
    g13: LineSegment StartX=-4.8 StartY=30.5 StartZ=0 EndX=0 EndY=30.5 EndZ=0
    g14: LineSegment StartX=-3.5 StartY=5 StartZ=0 EndX=-3.5 EndY=7 EndZ=0
    g15: LineSegment StartX=0 StartY=5 StartZ=0 EndX=0 EndY=30.5 EndZ=0
    g16: LineSegment StartX=-3.5 StartY=5 StartZ=0 EndX=0 EndY=5 EndZ=0
  constraints (33):
    c: Weight(g0) = 1
    c: Equal(g0,g1)
    c: Equal(g0,g2)
    c: InternalAlignment(g0,g3)
    c: InternalAlignment(g1,g3)
    c: InternalAlignment(g2,g3)
    c: InternalAlignment(g4,g3)
    c: InternalAlignment(g5,g3)
    c: Block(g3)
    c: Weight(g6) = 1
    c: Equal(g6,g7)
    c: Equal(g6,g8)
    c: InternalAlignment(g6,g9)
    c: InternalAlignment(g7,g9)
    c: InternalAlignment(g8,g9)
    c: InternalAlignment(g10,g9)
    c: InternalAlignment(g11,g9)
    c: Block(g9)
    c: Coincident(g12,g9)
    c: Coincident(g12,g3)
    c: Vertical(g12)
    c: Coincident(g13,g9)
    c: Horizontal(g13)
    c: Distance(g13) = 4.8
    c: Coincident(g14,g3)
    c: Vertical(g14)
    c: Coincident(g15,g13)
    c: Vertical(g15)
    c: Tangent(g15,g1)
    c: Distance(g14) = 2
    c: Coincident(g16,g14)
    c: Horizontal(g16)
    c: Coincident(g15,g16)
FEATURE [Part::Feature] Face050
  shape: bbox 4.8 x 25.5 x 2e-07 mm, 1 faces, 0 solids (baked)
FEATURE [Part::Revolution] Revolve054  label="moreFrontCaseScrewPost001"
  Angle = 360
  Axis = (0,1,0)
  Base = (0,0,0)
  FaceMakerClass = Part::FaceMakerBullseye
  Placement = pos=(102.5,4.5,3.5) rot=(0,0,1;0rad)
  Solid = false
  Source = -> Face050
  Symmetric = false
FEATURE [Part::Feature] Face051
  shape: bbox 4.8 x 25.5 x 2e-07 mm, 1 faces, 0 solids (baked)
FEATURE [Part::Revolution] Revolve055  label="moreFrontCaseScrewPost002"
  Angle = 360
  Axis = (0,1,0)
  Base = (0,0,0)
  FaceMakerClass = Part::FaceMakerBullseye
  Placement = pos=(102.5,4.5,68.5) rot=(0,0,1;0rad)
  Solid = false
  Source = -> Face051
  Symmetric = false
FEATURE [Sketcher::SketchObject] Sketch027
  FullyConstrained = true
  sketch-geometry (10):
    g0: LineSegment StartX=-1.6 StartY=4.7 StartZ=0 EndX=-1.6 EndY=1.7 EndZ=0
    g1: LineSegment StartX=-3.5 StartY=4.7 StartZ=0 EndX=-1.6 EndY=4.7 EndZ=0
    g2: LineSegment StartX=-1.6 StartY=1.7 StartZ=0 EndX=-1.6 EndY=1.5 EndZ=0
    g3: LineSegment StartX=-1.6 StartY=1.5 StartZ=0 EndX=-5.2 EndY=1.5 EndZ=0
    g4: Circle CenterX=-3.5 CenterY=4.7 CenterZ=0 NormalX=0 NormalY=0 NormalZ=1 AngleXU=0 Radius=1
    g5: Circle CenterX=-3.59627 CenterY=2.99743 CenterZ=0 NormalX=0 NormalY=0 NormalZ=1 AngleXU=0 Radius=1
    g6: Circle CenterX=-5.2 CenterY=1.5 CenterZ=0 NormalX=0 NormalY=0 NormalZ=1 AngleXU=0 Radius=1
    g7: BSplineCurve PolesCount=3 KnotsCount=2 Degree=2 IsPeriodic=0
    g8: GeomPoint X=-3.5 Y=4.7 Z=0
    g9: GeomPoint X=-5.2 Y=1.5 Z=0
  constraints (23):
    c: Vertical(g0)
    c: Distance(g0) = 3
    c: Coincident(g1,g0)
    c: Horizontal(g1)
    c: Block(g0)
    c: Block(g1)
    c: Coincident(g2,g0)
    c: Vertical(g2)
    c: Distance(g2) = 0.2
    c: Coincident(g3,g2)
    c: Horizontal(g3)
    c: Block(g3)
    c: Coincident(g7,g1)
    c: Weight(g4) = 1
    c: Equal(g4,g5)
    c: Equal(g4,g6)
    c: Coincident(g7,g3)
    c: InternalAlignment(g4,g7)
    c: InternalAlignment(g5,g7)
    c: InternalAlignment(g6,g7)
    c: InternalAlignment(g8,g7)
    c: InternalAlignment(g9,g7)
    c: Block(g7)
FEATURE [Sketcher::SketchObject] Sketch028
  FullyConstrained = true
  sketch-geometry (18):
    g0: LineSegment StartX=0 StartY=3e-16 StartZ=0 EndX=0 EndY=1.7 EndZ=0
    g1: LineSegment StartX=-3.5 StartY=0 StartZ=0 EndX=-3.5 EndY=0.9 EndZ=0
    g2: Circle CenterX=-2.7 CenterY=1.7 CenterZ=0 NormalX=0 NormalY=0 NormalZ=1 AngleXU=0 Radius=1
    g3: Circle CenterX=-3.5 CenterY=1.7 CenterZ=0 NormalX=0 NormalY=0 NormalZ=1 AngleXU=0 Radius=1
    g4: Circle CenterX=-3.5 CenterY=0.9 CenterZ=0 NormalX=0 NormalY=0 NormalZ=1 AngleXU=0 Radius=1
    g5: BSplineCurve PolesCount=3 KnotsCount=2 Degree=2 IsPeriodic=0
    g6: GeomPoint X=-2.7 Y=1.7 Z=0
    g7: GeomPoint X=-3.5 Y=0.9 Z=0
    g8: LineSegment StartX=-3.5 StartY=0 StartZ=0 EndX=-3.5 EndY=-7 EndZ=0
    g9: LineSegment StartX=0 StartY=3e-16 StartZ=0 EndX=0 EndY=-7 EndZ=0
    g10: LineSegment StartX=-3.5 StartY=-7 StartZ=0 EndX=0 EndY=-7 EndZ=0
    g11: LineSegment StartX=-2.7 StartY=1.7 StartZ=0 EndX=-1.6 EndY=1.7 EndZ=0
    g12: LineSegment StartX=0 StartY=1.7 StartZ=0 EndX=0 EndY=4.5 EndZ=0
    g13: LineSegment StartX=0 StartY=4.5 StartZ=0 EndX=0 EndY=10.8 EndZ=0
    g14: LineSegment StartX=0 StartY=10.8 StartZ=0 EndX=-2 EndY=10.8 EndZ=0
    g15: LineSegment StartX=-1.6 StartY=4.7 StartZ=0 EndX=-1.6 EndY=1.7 EndZ=0
    g16: LineSegment StartX=-1.6 StartY=4.7 StartZ=0 EndX=-2 EndY=4.7 EndZ=0
    g17: LineSegment StartX=-2 StartY=4.7 StartZ=0 EndX=-2 EndY=10.8 EndZ=0
  constraints (44):
    c: Vertical(g0)
    c: Vertical(g1)
    c: Distance(g1) = 0.9
    c: Block(g0)
    c: Distance(g0) = 1.7
    c: Weight(g2) = 1
    c: Equal(g2,g3)
    c: Equal(g2,g4)
    c: Coincident(g5,g1)
    c: InternalAlignment(g2,g5)
    c: InternalAlignment(g3,g5)
    c: InternalAlignment(g4,g5)
    c: InternalAlignment(g6,g5)
    c: InternalAlignment(g7,g5)
    c: Block(g5)
    c: Coincident(g8,g1)
    c: Vertical(g8)
    c: Distance(g8) = 7
    c: Vertical(g9)
    c: Equal(g8,g9) = 7
    c: Coincident(g9,g0)
    c: Coincident(g10,g8)
    c: Coincident(g10,g9)
    c: Horizontal(g10)
    c: Coincident(g11,g5)
    c: Horizontal(g11)
    c: Coincident(g12,g0)
    c: Vertical(g12)
    c: Distance(g12) = 2.8
    c: Coincident(g13,g12)
    c: Vertical(g13)
    c: Distance(g13) = 6.3
    c: Coincident(g14,g13)
    c: Horizontal(g14)
    c: Distance(g14) = 2
    c: Vertical(g15)
    c: Distance(g15) = 3
    c: Block(g11)
    c: Coincident(g15,g11)
    c: Coincident(g16,g15)
    c: Horizontal(g16)
    c: Coincident(g17,g16)
    c: Coincident(g17,g14)
    c: Vertical(g17)
FEATURE [Part::Revolution] Revolve040  label="backCaseScrewRetainer001"
  Angle = 360
  Axis = (0,1,0)
  Base = (0,0,0)
  FaceMakerClass = Part::FaceMakerBullseye
  Placement = pos=(12.5,3,10) rot=(0,0,1;0rad)
  Solid = false
  Source = -> Face036
  Symmetric = false
FEATURE [Part::Feature] Face055
  shape: bbox 3.5 x 30.2 x 2e-07 mm, 1 faces, 0 solids (baked)
FEATURE [Part::Revolution] Revolve059  label="backCaseScrewPost"
  Angle = 360
  Axis = (0,1,0)
  Base = (0,0,0)
  FaceMakerClass = Part::FaceMakerBullseye
  Placement = pos=(12.5,4.5,10) rot=(0,0,1;0rad)
  Solid = false
  Source = -> Face055
  Symmetric = false
FEATURE [Part::Feature] Face056
  shape: bbox 3.5 x 30.2 x 2e-07 mm, 1 faces, 0 solids (baked)
FEATURE [Part::Revolution] Revolve060  label="backCaseScrewPost001"
  Angle = 360
  Axis = (0,1,0)
  Base = (0,0,0)
  FaceMakerClass = Part::FaceMakerBullseye
  Placement = pos=(12.5,4.5,62) rot=(0,0,1;0rad)
  Solid = false
  Source = -> Face056
  Symmetric = false
FEATURE [Part::Feature] Face057
  shape: bbox 3.5 x 17.8 x 2e-07 mm, 1 faces, 0 solids (baked)
FEATURE [Part::Revolution] Revolve061  label="removeToCreateScrewAndThreadedInsertHole"
  Angle = 360
  Axis = (0,1,0)
  Base = (0,0,0)
  FaceMakerClass = Part::FaceMakerBullseye
  Placement = pos=(12.5,0,10) rot=(0,0,1;0rad)
  Solid = false
  Source = -> Face057
  Symmetric = false
FEATURE [Part::Feature] Face058
  shape: bbox 3.5 x 17.8 x 2e-07 mm, 1 faces, 0 solids (baked)
FEATURE [Part::Revolution] Revolve062  label="removeToCreateScrewAndThreadedInsertHole001"
  Angle = 360
  Axis = (0,1,0)
  Base = (0,0,0)
  FaceMakerClass = Part::FaceMakerBullseye
  Placement = pos=(12.5,0,62) rot=(0,0,1;0rad)
  Solid = false
  Source = -> Face058
  Symmetric = false
FEATURE [Part::Feature] Face059
  shape: bbox 3.5 x 17.8 x 2e-07 mm, 1 faces, 0 solids (baked)
FEATURE [Part::Revolution] Revolve063  label="removeToCreateScrewAndThreadedInsertHole002"
  Angle = 360
  Axis = (0,1,0)
  Base = (0,0,0)
  FaceMakerClass = Part::FaceMakerBullseye
  Placement = pos=(89.5,0,68.5) rot=(0,0,1;0rad)
  Solid = false
  Source = -> Face059
  Symmetric = false
FEATURE [Part::Feature] Face060
  shape: bbox 3.5 x 17.8 x 2e-07 mm, 1 faces, 0 solids (baked)
FEATURE [Part::Revolution] Revolve064  label="removeToCreateScrewAndThreadedInsertHole003"
  Angle = 360
  Axis = (0,1,0)
  Base = (0,0,0)
  FaceMakerClass = Part::FaceMakerBullseye
  Placement = pos=(89.5,0,3.5) rot=(0,0,1;0rad)
  Solid = false
  Source = -> Face060
  Symmetric = false
FEATURE [Part::Feature] Face061
  shape: bbox 3.5 x 17.8 x 2e-07 mm, 1 faces, 0 solids (baked)
FEATURE [Part::Revolution] Revolve065  label="removeToCreateScrewAndThreadedInsertHole004"
  Angle = 360
  Axis = (0,1,0)
  Base = (0,0,0)
  FaceMakerClass = Part::FaceMakerBullseye
  Placement = pos=(102.5,4.7,3.5) rot=(0,0,1;0rad)
  Solid = false
  Source = -> Face061
  Symmetric = false
FEATURE [Part::Feature] Face062
  shape: bbox 3.5 x 17.8 x 2e-07 mm, 1 faces, 0 solids (baked)
FEATURE [Part::Revolution] Revolve066  label="removeToCreateScrewAndThreadedInsertHole005"
  Angle = 360
  Axis = (0,1,0)
  Base = (0,0,0)
  FaceMakerClass = Part::FaceMakerBullseye
  Placement = pos=(102.5,4.7,68.5) rot=(0,0,1;0rad)
  Solid = false
  Source = -> Face062
  Symmetric = false
FEATURE [Part::MultiFuse] Fusion047  label="makeHoles"
  Shapes = -> [Revolve066,Revolve065,Revolve064,Revolve063,Revolve062,Revolve061]
FEATURE [Part::Feature] Face063
  shape: bbox 3.6 x 3.2 x 2e-07 mm, 1 faces, 0 solids (baked)
FEATURE [Part::Revolution] Revolve067  label="moreFrontCaseScrewRetainer002"
  Angle = 360
  Axis = (0,1,0)
  Base = (0,0,0)
  FaceMakerClass = Part::FaceMakerBullseye
  Placement = pos=(102.5,4.5,68.5) rot=(0,0,1;0rad)
  Solid = false
  Source = -> Face063
  Symmetric = false
FEATURE [Part::Feature] Face064
  shape: bbox 3.6 x 3.2 x 2e-07 mm, 1 faces, 0 solids (baked)
FEATURE [Part::Revolution] Revolve068  label="moreFrontCaseScrewRetainer003"
  Angle = 360
  Axis = (0,1,0)
  Base = (0,0,0)
  FaceMakerClass = Part::FaceMakerBullseye
  Placement = pos=(102.5,4.5,3.5) rot=(0,0,1;0rad)
  Solid = false
  Source = -> Face064
  Symmetric = false
FEATURE [Part::Feature] Face065
  shape: bbox 3.5 x 17.8 x 2e-07 mm, 1 faces, 0 solids (baked)
FEATURE [Part::Revolution] Revolve069  label="removeToCreateScrewAndThreadedInsertHole006"
  Angle = 360
  Axis = (0,1,0)
  Base = (0,0,0)
  FaceMakerClass = Part::FaceMakerBullseye
  Placement = pos=(12.5,0,10) rot=(0,0,1;0rad)
  Solid = false
  Source = -> Face065
  Symmetric = false
FEATURE [Part::Feature] Face066
  shape: bbox 3.5 x 17.8 x 2e-07 mm, 1 faces, 0 solids (baked)
FEATURE [Part::Revolution] Revolve070  label="removeToCreateScrewAndThreadedInsertHole007"
  Angle = 360
  Axis = (0,1,0)
  Base = (0,0,0)
  FaceMakerClass = Part::FaceMakerBullseye
  Placement = pos=(12.5,0,62) rot=(0,0,1;0rad)
  Solid = false
  Source = -> Face066
  Symmetric = false
FEATURE [Part::Feature] Face067
  shape: bbox 3.5 x 17.8 x 2e-07 mm, 1 faces, 0 solids (baked)
FEATURE [Part::Revolution] Revolve071  label="removeToCreateScrewAndThreadedInsertHole008"
  Angle = 360
  Axis = (0,1,0)
  Base = (0,0,0)
  FaceMakerClass = Part::FaceMakerBullseye
  Placement = pos=(89.5,0,68.5) rot=(0,0,1;0rad)
  Solid = false
  Source = -> Face067
  Symmetric = false
FEATURE [Part::Feature] Face068
  shape: bbox 3.5 x 17.8 x 2e-07 mm, 1 faces, 0 solids (baked)
FEATURE [Part::Revolution] Revolve072  label="removeToCreateScrewAndThreadedInsertHole009"
  Angle = 360
  Axis = (0,1,0)
  Base = (0,0,0)
  FaceMakerClass = Part::FaceMakerBullseye
  Placement = pos=(89.5,0,3.5) rot=(0,0,1;0rad)
  Solid = false
  Source = -> Face068
  Symmetric = false
FEATURE [Part::Feature] Face069
  shape: bbox 3.5 x 17.8 x 2e-07 mm, 1 faces, 0 solids (baked)
FEATURE [Part::Feature] Face070
  shape: bbox 3.5 x 17.8 x 2e-07 mm, 1 faces, 0 solids (baked)
FEATURE [Part::Revolution] Revolve073  label="removeToCreateScrewAndThreadedInsertHole010"
  Angle = 360
  Axis = (0,1,0)
  Base = (0,0,0)
  FaceMakerClass = Part::FaceMakerBullseye
  Placement = pos=(102.5,4.7,3.5) rot=(0,0,1;0rad)
  Solid = false
  Source = -> Face069
  Symmetric = false
FEATURE [Part::Revolution] Revolve074  label="removeToCreateScrewAndThreadedInsertHole011"
  Angle = 360
  Axis = (0,1,0)
  Base = (0,0,0)
  FaceMakerClass = Part::FaceMakerBullseye
  Placement = pos=(102.5,4.7,68.5) rot=(0,0,1;0rad)
  Solid = false
  Source = -> Face070
  Symmetric = false
FEATURE [Part::MultiFuse] Fusion048  label="makeHoles001"
  Shapes = -> [Revolve074,Revolve073,Revolve072,Revolve071,Revolve070,Revolve069]
FEATURE [Part::MultiFuse] Fusion049  label="caseScrewRetainers"
  Shapes = -> [Revolve067,Revolve068,Revolve048,Revolve047,Revolve039,Revolve040]
FEATURE [Part::Cut] Cut015  label="caseScrewRetainers001"
  Base = -> Fusion049
  Tool = -> Fusion048
FEATURE [Part::MultiFuse] Fusion050  label="casePillars"
  Shapes = -> [Revolve055,Revolve054,Revolve043,Revolve046,Revolve059,Revolve060]
FEATURE [Part::Feature] Face071 .. Face076  x6 (patterned run collapsed; names and placements below)
  shape: bbox 3.5 x 17.8 x 2e-07 mm, 1 faces, 0 solids (baked)
FEATURE [Part::Revolution] Revolve075  label="removeToCreateScrewAndThreadedInsertHole012"
  Angle = 360
  Axis = (0,1,0)
  Base = (0,0,0)
  FaceMakerClass = Part::FaceMakerBullseye
  Placement = pos=(12.5,0,10) rot=(0,0,1;0rad)
  Solid = false
  Source = -> Face071
  Symmetric = false
FEATURE [Part::Revolution] Revolve076  label="removeToCreateScrewAndThreadedInsertHole013"
  Angle = 360
  Axis = (0,1,0)
  Base = (0,0,0)
  FaceMakerClass = Part::FaceMakerBullseye
  Placement = pos=(12.5,0,62) rot=(0,0,1;0rad)
  Solid = false
  Source = -> Face072
  Symmetric = false
FEATURE [Part::Revolution] Revolve077  label="removeToCreateScrewAndThreadedInsertHole014"
  Angle = 360
  Axis = (0,1,0)
  Base = (0,0,0)
  FaceMakerClass = Part::FaceMakerBullseye
  Placement = pos=(89.5,0,68.5) rot=(0,0,1;0rad)
  Solid = false
  Source = -> Face073
  Symmetric = false
FEATURE [Part::Revolution] Revolve078  label="removeToCreateScrewAndThreadedInsertHole015"
  Angle = 360
  Axis = (0,1,0)
  Base = (0,0,0)
  FaceMakerClass = Part::FaceMakerBullseye
  Placement = pos=(89.5,0,3.5) rot=(0,0,1;0rad)
  Solid = false
  Source = -> Face074
  Symmetric = false
FEATURE [Part::Revolution] Revolve079  label="removeToCreateScrewAndThreadedInsertHole016"
  Angle = 360
  Axis = (0,1,0)
  Base = (0,0,0)
  FaceMakerClass = Part::FaceMakerBullseye
  Placement = pos=(102.5,4.7,3.5) rot=(0,0,1;0rad)
  Solid = false
  Source = -> Face075
  Symmetric = false
FEATURE [Part::Revolution] Revolve080  label="removeToCreateScrewAndThreadedInsertHole017"
  Angle = 360
  Axis = (0,1,0)
  Base = (0,0,0)
  FaceMakerClass = Part::FaceMakerBullseye
  Placement = pos=(102.5,4.7,68.5) rot=(0,0,1;0rad)
  Solid = false
  Source = -> Face076
  Symmetric = false
FEATURE [Part::MultiFuse] Fusion051  label="makeHoles002"
  Shapes = -> [Revolve080,Revolve079,Revolve078,Revolve077,Revolve076,Revolve075]
FEATURE [Part::Cut] Cut016  label="caesPillars"
  Base = -> Fusion050
  Tool = -> Fusion051
FEATURE [Part::Revolution] Revolve009  label="plugHousing016"
  Angle = 360
  Axis = (0,1,0)
  Base = (0,0,0)
  FaceMakerClass = Part::FaceMakerBullseye
  Placement = pos=(0,0,36.15) rot=(0,0,1;0rad)
  Solid = false
  Source = -> Face012
  Symmetric = false
FEATURE [Part::MultiFuse] Fusion014  label="plugHousing023"
  Placement = pos=(0,0,0) rot=(0,0,1;1.5708rad)
  Shapes = -> [Revolve011,Revolve009]
FEATURE [Part::Revolution] Revolve010  label="plugHousing017"
  Angle = 360
  Axis = (0,1,0)
  Base = (0,0,0)
  FaceMakerClass = Part::FaceMakerBullseye
  Placement = pos=(0,0,36.15) rot=(0,0,1;0rad)
  Solid = false
  Source = -> Face014
  Symmetric = false
FEATURE [Part::MultiFuse] Fusion015  label="plugHousing024"
  Placement = pos=(0,0,0) rot=(0,0,1;1.5708rad)
  Shapes = -> [Revolve010,Revolve015]
FEATURE [Part::Revolution] Revolve014  label="plugHousing026"
  Angle = 360
  Axis = (0,1,0)
  Base = (0,0,0)
  FaceMakerClass = Part::FaceMakerBullseye
  Placement = pos=(0,0,36.15) rot=(0,0,1;0rad)
  Solid = false
  Source = -> Face011
  Symmetric = false
FEATURE [Part::Revolution] Revolve013  label="plugHousing025"
  Angle = 360
  Axis = (0,1,0)
  Base = (0,0,0)
  FaceMakerClass = Part::FaceMakerBullseye
  Placement = pos=(0,0,36.15) rot=(0,0,1;0rad)
  Solid = false
  Source = -> Face015
  Symmetric = false
FEATURE [Part::MultiFuse] Fusion016  label="plugHousing028"
  Placement = pos=(0,19,0) rot=(0,0,1;3.14159rad)
  Shapes = -> [Fusion014,Fusion013]
FEATURE [Part::MultiFuse] Fusion011  label="plugHousing018"
  Placement = pos=(0,0,0) rot=(0,0,1;1.5708rad)
  Shapes = -> [Revolve014,Revolve013]
FEATURE [Part::MultiFuse] Fusion012  label="plugHousing019"
  Placement = pos=(0,19,0) rot=(0,0,1;3.14159rad)
  Shapes = -> [Fusion011,Fusion015]
FEATURE [Part::MultiFuse] Fusion017  label="plugHousing029"
  Placement = pos=(122.621,0,-0.15) rot=(0,0,1;0rad)
  Shapes = -> [Fusion016,Fusion012]
FEATURE [Part::MultiFuse] Fusion052  label="casePillarRetainers"
  Shapes = -> [Extrude012,Extrude013,Extrude014,Extrude015,Extrude016,Extrude017,Extrude018,Extrude019,Box011,Box012]
FEATURE [Part::Feature] Face077
  shape: bbox 3.5 x 17.8 x 2e-07 mm, 1 faces, 0 solids (baked)
FEATURE [Part::Revolution] Revolve081  label="removeToCreateScrewAndThreadedInsertHole018"
  Angle = 360
  Axis = (0,1,0)
  Base = (0,0,0)
  FaceMakerClass = Part::FaceMakerBullseye
  Placement = pos=(62.3,30.3,19.7) rot=(0,0,1;0rad)
  Solid = false
  Source = -> Face077
  Symmetric = false
FEATURE [Part::Feature] Face078
  shape: bbox 3.5 x 17.8 x 2e-07 mm, 1 faces, 0 solids (baked)
FEATURE [Part::Revolution] Revolve082  label="removeToCreateScrewAndThreadedInsertHole019"
  Angle = 360
  Axis = (0,1,0)
  Base = (0,0,0)
  FaceMakerClass = Part::FaceMakerBullseye
  Placement = pos=(62.3,30.3,51.7) rot=(0,0,1;0rad)
  Solid = false
  Source = -> Face078
  Symmetric = false
FEATURE [Part::Feature] Face079
  shape: bbox 3.5 x 17.8 x 2e-07 mm, 1 faces, 0 solids (baked)
FEATURE [Part::Revolution] Revolve083  label="removeToCreateScrewAndThreadedInsertHole020"
  Angle = 360
  Axis = (0,1,0)
  Base = (0,0,0)
  FaceMakerClass = Part::FaceMakerBullseye
  Placement = pos=(30.3,30.3,19.7) rot=(0,0,1;0rad)
  Solid = false
  Source = -> Face079
  Symmetric = false
FEATURE [Part::Feature] Face080
  shape: bbox 3.5 x 17.8 x 2e-07 mm, 1 faces, 0 solids (baked)
FEATURE [Part::Revolution] Revolve084  label="removeToCreateScrewAndThreadedInsertHole021"
  Angle = 360
  Axis = (0,1,0)
  Base = (0,0,0)
  FaceMakerClass = Part::FaceMakerBullseye
  Placement = pos=(30.3,30.3,51.7) rot=(0,0,1;0rad)
  Solid = false
  Source = -> Face080
  Symmetric = false
FEATURE [Part::MultiFuse] Fusion053  label="createThreadedInsertHolesForFan"
  Shapes = -> [Revolve081,Revolve082,Revolve083,Revolve084]
FEATURE [Part::Cut] Cut017  label="fanScrewHousing001"
  Base = -> Fusion046
  Tool = -> Fusion053
FEATURE [Part::Feature] Face081
  shape: bbox 3.5 x 17.8 x 2e-07 mm, 1 faces, 0 solids (baked)
FEATURE [Part::Revolution] Revolve085  label="removeToCreateScrewAndThreadedInsertHole022"
  Angle = 360
  Axis = (0,1,0)
  Base = (0,0,0)
  FaceMakerClass = Part::FaceMakerBullseye
  Placement = pos=(62.3,30.3,19.7) rot=(0,0,1;0rad)
  Solid = false
  Source = -> Face081
  Symmetric = false
FEATURE [Part::Feature] Face082
  shape: bbox 3.5 x 17.8 x 2e-07 mm, 1 faces, 0 solids (baked)
FEATURE [Part::Revolution] Revolve086  label="removeToCreateScrewAndThreadedInsertHole023"
  Angle = 360
  Axis = (0,1,0)
  Base = (0,0,0)
  FaceMakerClass = Part::FaceMakerBullseye
  Placement = pos=(62.3,30.3,51.7) rot=(0,0,1;0rad)
  Solid = false
  Source = -> Face082
  Symmetric = false
FEATURE [Part::Feature] Face083
  shape: bbox 3.5 x 17.8 x 2e-07 mm, 1 faces, 0 solids (baked)
FEATURE [Part::Revolution] Revolve087  label="removeToCreateScrewAndThreadedInsertHole024"
  Angle = 360
  Axis = (0,1,0)
  Base = (0,0,0)
  FaceMakerClass = Part::FaceMakerBullseye
  Placement = pos=(30.3,30.3,19.7) rot=(0,0,1;0rad)
  Solid = false
  Source = -> Face083
  Symmetric = false
FEATURE [Part::Feature] Face084
  shape: bbox 3.5 x 17.8 x 2e-07 mm, 1 faces, 0 solids (baked)
FEATURE [Part::Revolution] Revolve088  label="removeToCreateScrewAndThreadedInsertHole025"
  Angle = 360
  Axis = (0,1,0)
  Base = (0,0,0)
  FaceMakerClass = Part::FaceMakerBullseye
  Placement = pos=(30.3,30.3,51.7) rot=(0,0,1;0rad)
  Solid = false
  Source = -> Face084
  Symmetric = false
FEATURE [Part::MultiFuse] Fusion054  label="createThreadedInsertHolesForFan001"
  Shapes = -> [Revolve085,Revolve086,Revolve087,Revolve088]
FEATURE [Part::Cut] Cut018  label="top007"
  Base = -> Fusion040
  Tool = -> Fusion054
FEATURE [Sketcher::SketchObject] Sketch029
  FullyConstrained = false
  Placement = pos=(0,0,0) rot=(1,0,0;1.5708rad)
  sketch-geometry (24):
    g0: ArcOfCircle CenterX=-4 CenterY=-10.5 CenterZ=0 NormalX=0 NormalY=0 NormalZ=1 AngleXU=0 Radius=1.5 StartAngle=6e-16 EndAngle=3.14159
    g1: ArcOfCircle CenterX=-34.2 CenterY=-10.5 CenterZ=0 NormalX=0 NormalY=0 NormalZ=1 AngleXU=0 Radius=1.5 StartAngle=0 EndAngle=3.14159
    g2: ArcOfCircle CenterX=-34.2 CenterY=-27.7 CenterZ=0 NormalX=0 NormalY=0 NormalZ=1 AngleXU=0 Radius=1.5 StartAngle=3.14159 EndAngle=6.28319
    g3: ArcOfCircle CenterX=-4 CenterY=-27.7 CenterZ=0 NormalX=0 NormalY=0 NormalZ=1 AngleXU=0 Radius=1.5 StartAngle=3.1416 EndAngle=6.28319
    g4: ArcOfCircle CenterX=-10 CenterY=-4.3 CenterZ=0 NormalX=0 NormalY=0 NormalZ=1 AngleXU=0 Radius=1.5 StartAngle=2e-16 EndAngle=3.14159
    g5: ArcOfCircle CenterX=-16.1 CenterY=-1.8 CenterZ=0 NormalX=0 NormalY=0 NormalZ=1 AngleXU=0 Radius=1.5 StartAngle=5e-16 EndAngle=3.14159
    g6: ArcOfCircle CenterX=-22.1 CenterY=-1.8 CenterZ=0 NormalX=0 NormalY=0 NormalZ=1 AngleXU=0 Radius=1.5 StartAngle=5e-16 EndAngle=3.14159
    g7: ArcOfCircle CenterX=-28.2 CenterY=-4.3 CenterZ=0 NormalX=0 NormalY=0 NormalZ=1 AngleXU=0 Radius=1.5 StartAngle=2e-16 EndAngle=3.14159
    g8: ArcOfCircle CenterX=-10 CenterY=-33.9 CenterZ=0 NormalX=0 NormalY=0 NormalZ=1 AngleXU=0 Radius=1.5 StartAngle=3.14159 EndAngle=6.28319
    g9: ArcOfCircle CenterX=-16.1 CenterY=-36.4 CenterZ=0 NormalX=0 NormalY=0 NormalZ=1 AngleXU=0 Radius=1.5 StartAngle=3.14159 EndAngle=6.28319
    g10: ArcOfCircle CenterX=-22.1 CenterY=-36.4 CenterZ=0 NormalX=0 NormalY=0 NormalZ=1 AngleXU=0 Radius=1.5 StartAngle=3.14159 EndAngle=6.28319
    g11: ArcOfCircle CenterX=-28.2 CenterY=-33.9 CenterZ=0 NormalX=0 NormalY=0 NormalZ=1 AngleXU=0 Radius=1.5 StartAngle=3.14159 EndAngle=6.28319
    g12: LineSegment StartX=-35.7 StartY=-10.5 StartZ=0 EndX=-35.7 EndY=-27.7 EndZ=0
    g13: LineSegment StartX=-32.7 StartY=-10.5 StartZ=0 EndX=-32.7 EndY=-27.7 EndZ=0
    g14: LineSegment StartX=-29.7 StartY=-33.9 StartZ=0 EndX=-29.7 EndY=-4.3 EndZ=0
    g15: LineSegment StartX=-26.7 StartY=-33.9 StartZ=0 EndX=-26.7 EndY=-4.3 EndZ=0
    g16: LineSegment StartX=-2.5 StartY=-10.5 StartZ=0 EndX=-2.5 EndY=-27.7 EndZ=0
    g17: LineSegment StartX=-8.5 StartY=-4.3 StartZ=0 EndX=-8.5 EndY=-33.9 EndZ=0
    g18: LineSegment StartX=-5.5 StartY=-10.5 StartZ=0 EndX=-5.5 EndY=-27.7 EndZ=0
    g19: LineSegment StartX=-11.5 StartY=-4.3 StartZ=0 EndX=-11.5 EndY=-33.9 EndZ=0
    g20: LineSegment StartX=-14.6 StartY=-1.8 StartZ=0 EndX=-14.6 EndY=-36.4 EndZ=0
    g21: LineSegment StartX=-17.6 StartY=-1.8 StartZ=0 EndX=-17.6 EndY=-36.4 EndZ=0
    g22: LineSegment StartX=-20.6 StartY=-36.4 StartZ=0 EndX=-20.6 EndY=-1.8 EndZ=0
    g23: LineSegment StartX=-23.6 StartY=-1.8 StartZ=0 EndX=-23.6 EndY=-36.4 EndZ=0
  constraints (48):
    c: Block(g0)
    c: Block(g1)
    c: Block(g2)
    c: Block(g3)
    c: Block(g4)
    c: Block(g5)
    c: Block(g6)
    c: Block(g7)
    c: Block(g8)
    c: Block(g9)
    c: Block(g10)
    c: Block(g11)
    c: Coincident(g12,g1)
    c: Coincident(g12,g2)
    c: Vertical(g12)
    c: Coincident(g13,g1)
    c: Coincident(g13,g2)
    c: Vertical(g13)
    c: Coincident(g14,g11)
    c: Coincident(g14,g7)
    c: Vertical(g14)
    c: Coincident(g15,g11)
    c: Coincident(g15,g7)
    c: Vertical(g15)
    c: Coincident(g16,g0)
    c: Coincident(g16,g3)
    c: Vertical(g16)
    c: Coincident(g17,g4)
    c: Coincident(g17,g8)
    c: Vertical(g17)
    c: Coincident(g18,g0)
    c: Coincident(g18,g3)
    c: Vertical(g18)
    c: Coincident(g19,g4)
    c: Coincident(g19,g8)
    c: Vertical(g19)
    c: Coincident(g20,g5)
    c: Coincident(g20,g9)
    c: Vertical(g20)
    c: Coincident(g21,g5)
    c: Coincident(g21,g9)
    c: Vertical(g21)
    c: Coincident(g22,g10)
    c: Coincident(g22,g6)
    c: Vertical(g22)
    c: Coincident(g23,g6)
    c: Coincident(g23,g10)
    c: Vertical(g23)
FEATURE [Part::Extrusion] Extrude020  label="removeToCreateFanGrillHoles"
  Base = -> Sketch029
  Dir = (0,-1,6e-16)
  DirMode = 2
  FaceMakerClass = Part::FaceMakerBullseye
  LengthFwd = 10
  LengthRev = 0
  Placement = pos=(65.4,44,54.82) rot=(0,0,1;0rad)
  Solid = true
  Symmetric = false
FEATURE [Part::MultiFuse] Fusion055  label="top008"
  Shapes = -> [Cut017,Cut018]
FEATURE [Part::Cut] Cut019  label="top009"
  Base = -> Fusion055
  Tool = -> Extrude020
FEATURE [App::MeasureDistance] Distance003  label="Distance: 71.95 mm"
  Distance = 71.9513
  P1 = (117,38,72)
  P2 = (117,38,0.0487319)
FEATURE [Sketcher::SketchObject] Sketch030
  FullyConstrained = true
  Placement = pos=(117,19,0) rot=(0.57735,0.57735,0.57735;2.0944rad)
  sketch-geometry (48):
    g0: LineSegment StartX=-49.19 StartY=69.25 StartZ=0 EndX=-49.19 EndY=66.25 EndZ=0
    g1: LineSegment StartX=-49.19 StartY=63.5 StartZ=0 EndX=-49.19 EndY=60.5 EndZ=0
    g2: LineSegment StartX=-49.19 StartY=57.75 StartZ=0 EndX=-49.19 EndY=54.75 EndZ=0
    g3: LineSegment StartX=-49.19 StartY=52 StartZ=0 EndX=-49.19 EndY=49 EndZ=0
    g4: LineSegment StartX=-49.19 StartY=46.25 StartZ=0 EndX=-49.19 EndY=43.25 EndZ=0
    g5: LineSegment StartX=-49.19 StartY=40.5 StartZ=0 EndX=-49.19 EndY=37.5 EndZ=0
    g6: LineSegment StartX=-49.19 StartY=34.5 StartZ=0 EndX=-49.19 EndY=31.5 EndZ=0
    g7: LineSegment StartX=-49.19 StartY=28.75 StartZ=0 EndX=-49.19 EndY=25.75 EndZ=0
    g8: LineSegment StartX=-49.19 StartY=23 StartZ=0 EndX=-49.19 EndY=20 EndZ=0
    g9: LineSegment StartX=-49.19 StartY=17.25 StartZ=0 EndX=-49.19 EndY=14.25 EndZ=0
    g10: LineSegment StartX=-49.19 StartY=11.5 StartZ=0 EndX=-49.19 EndY=8.5 EndZ=0
    g11: LineSegment StartX=-49.19 StartY=5.75 StartZ=0 EndX=-49.19 EndY=2.75 EndZ=0
    g12: ArcOfCircle CenterX=-1.5 CenterY=67.75 CenterZ=0 NormalX=0 NormalY=0 NormalZ=1 AngleXU=0 Radius=1.5 StartAngle=4.71239 EndAngle=7.85398
    g13: ArcOfCircle CenterX=-1.5 CenterY=62 CenterZ=0 NormalX=0 NormalY=0 NormalZ=1 AngleXU=0 Radius=1.5 StartAngle=4.71239 EndAngle=7.85398
    g14: ArcOfCircle CenterX=-1.5 CenterY=56.25 CenterZ=0 NormalX=0 NormalY=0 NormalZ=1 AngleXU=0 Radius=1.5 StartAngle=4.71239 EndAngle=7.85398
    g15: ArcOfCircle CenterX=-11.49 CenterY=50.5 CenterZ=0 NormalX=0 NormalY=0 NormalZ=1 AngleXU=0 Radius=1.5 StartAngle=4.71239 EndAngle=7.85398
    g16: ArcOfCircle CenterX=-16.28 CenterY=44.75 CenterZ=0 NormalX=0 NormalY=0 NormalZ=1 AngleXU=0 Radius=1.5 StartAngle=4.71239 EndAngle=7.85398
    g17: ArcOfCircle CenterX=-18.2337 CenterY=39 CenterZ=0 NormalX=0 NormalY=0 NormalZ=1 AngleXU=0 Radius=1.5 StartAngle=4.71485 EndAngle=7.85398
    g18: ArcOfCircle CenterX=-16.2837 CenterY=27.25 CenterZ=0 NormalX=0 NormalY=0 NormalZ=1 AngleXU=0 Radius=1.5 StartAngle=4.71485 EndAngle=7.85398
    g19: ArcOfCircle CenterX=-18.2337 CenterY=33 CenterZ=0 NormalX=0 NormalY=0 NormalZ=1 AngleXU=0 Radius=1.5 StartAngle=4.71485 EndAngle=7.85398
    g20: ArcOfCircle CenterX=-11.49 CenterY=21.5 CenterZ=0 NormalX=0 NormalY=0 NormalZ=1 AngleXU=0 Radius=1.5 StartAngle=4.71239 EndAngle=7.85398
    g21: ArcOfCircle CenterX=-1.5 CenterY=4.25 CenterZ=0 NormalX=0 NormalY=0 NormalZ=1 AngleXU=0 Radius=1.5 StartAngle=4.71239 EndAngle=7.85398
    g22: ArcOfCircle CenterX=-1.5 CenterY=10 CenterZ=0 NormalX=0 NormalY=0 NormalZ=1 AngleXU=0 Radius=1.5 StartAngle=4.71239 EndAngle=7.85398
    g23: ArcOfCircle CenterX=-1.5 CenterY=15.75 CenterZ=0 NormalX=0 NormalY=0 NormalZ=1 AngleXU=0 Radius=1.5 StartAngle=4.71239 EndAngle=7.85398
    g24: LineSegment StartX=-49.19 StartY=69.25 StartZ=0 EndX=-1.5 EndY=69.25 EndZ=0
    g25: LineSegment StartX=-49.19 StartY=66.25 StartZ=0 EndX=-1.5 EndY=66.25 EndZ=0
    g26: LineSegment StartX=-49.19 StartY=63.5 StartZ=0 EndX=-1.5 EndY=63.5 EndZ=0
    g27: LineSegment StartX=-49.19 StartY=60.5 StartZ=0 EndX=-1.5 EndY=60.5 EndZ=0
    g28: LineSegment StartX=-49.19 StartY=57.75 StartZ=0 EndX=-1.5 EndY=57.75 EndZ=0
    g29: LineSegment StartX=-49.19 StartY=54.75 StartZ=0 EndX=-1.5 EndY=54.75 EndZ=0
    g30: LineSegment StartX=-49.19 StartY=52 StartZ=0 EndX=-11.49 EndY=52 EndZ=0
    g31: LineSegment StartX=-49.19 StartY=49 StartZ=0 EndX=-11.49 EndY=49 EndZ=0
    g32: LineSegment StartX=-49.19 StartY=46.25 StartZ=0 EndX=-16.28 EndY=46.25 EndZ=0
    g33: LineSegment StartX=-49.19 StartY=43.25 StartZ=0 EndX=-16.28 EndY=43.25 EndZ=0
    g34: LineSegment StartX=-49.19 StartY=40.5 StartZ=0 EndX=-18.2337 EndY=40.5 EndZ=0
    g35: LineSegment StartX=-49.19 StartY=37.5 StartZ=0 EndX=-18.23 EndY=37.5 EndZ=0
    g36: LineSegment StartX=-49.19 StartY=34.5 StartZ=0 EndX=-18.2337 EndY=34.5 EndZ=0
    g37: LineSegment StartX=-49.19 StartY=31.5 StartZ=0 EndX=-18.23 EndY=31.5 EndZ=0
    g38: LineSegment StartX=-49.19 StartY=28.75 StartZ=0 EndX=-16.2837 EndY=28.75 EndZ=0
    g39: LineSegment StartX=-49.19 StartY=25.75 StartZ=0 EndX=-16.28 EndY=25.75 EndZ=0
    g40: LineSegment StartX=-49.19 StartY=23 StartZ=0 EndX=-11.49 EndY=23 EndZ=0
    g41: LineSegment StartX=-49.19 StartY=20 StartZ=0 EndX=-11.49 EndY=20 EndZ=0
    g42: LineSegment StartX=-49.19 StartY=17.25 StartZ=0 EndX=-1.5 EndY=17.25 EndZ=0
    g43: LineSegment StartX=-49.19 StartY=14.25 StartZ=0 EndX=-1.5 EndY=14.25 EndZ=0
    g44: LineSegment StartX=-49.19 StartY=11.5 StartZ=0 EndX=-1.5 EndY=11.5 EndZ=0
    g45: LineSegment StartX=-49.19 StartY=8.5 StartZ=0 EndX=-1.5 EndY=8.5 EndZ=0
    g46: LineSegment StartX=-49.19 StartY=5.75 StartZ=0 EndX=-1.5 EndY=5.75 EndZ=0
    g47: LineSegment StartX=-49.19 StartY=2.75 StartZ=0 EndX=-1.5 EndY=2.75 EndZ=0
  constraints (120):
    c: Vertical(g0)
    c: Distance(g0) = 3
    c: Block(g0)
    c: Vertical(g1)
    c: Distance(g1) = 3
    c: Vertical(g2)
    c: Equal(g0,g2) = 3
    c: Block(g2)
    c: Vertical(g3)
    c: Equal(g1,g3) = 3
    c: Vertical(g4)
    c: Equal(g0,g4) = 3
    c: Block(g4)
    c: Vertical(g5)
    c: Equal(g1,g5) = 3
    c: Vertical(g6)
    c: Equal(g0,g6) = 3
    c: Block(g6)
    c: Vertical(g7)
    c: Equal(g1,g7) = 3
    c: Vertical(g8)
    c: Equal(g0,g8) = 3
    c: Block(g8)
    c: Vertical(g9)
    c: Equal(g1,g9) = 3
    c: Vertical(g10)
    c: Equal(g0,g10) = 3
    c: Block(g10)
    c: Vertical(g11)
    c: Equal(g1,g11) = 3
    c: Block(g12)
    c: Block(g13)
    c: Block(g14)
    c: Block(g15)
    c: Block(g16)
    c: Block(g17)
    c: Block(g18)
    c: Block(g19)
    c: Block(g20)
    c: Block(g21)
    c: Block(g22)
    c: Block(g23)
    c: Block(g11)
    c: Block(g9)
    c: Block(g7)
    c: Block(g5)
    c: Block(g3)
    c: Block(g1)
    c: Coincident(g24,g0)
    c: Coincident(g24,g12)
    c: Horizontal(g24)
    c: Coincident(g25,g0)
    c: Coincident(g25,g12)
    c: Horizontal(g25)
    c: Coincident(g26,g1)
    c: Coincident(g26,g13)
    c: Horizontal(g26)
    c: Coincident(g27,g1)
    c: Coincident(g27,g13)
    c: Horizontal(g27)
    c: Coincident(g28,g2)
    c: Coincident(g28,g14)
    c: Horizontal(g28)
    c: Coincident(g29,g2)
    c: Coincident(g29,g14)
    c: Horizontal(g29)
    c: Coincident(g30,g3)
    c: Coincident(g30,g15)
    c: Horizontal(g30)
    c: Coincident(g31,g3)
    c: Coincident(g31,g15)
    c: Horizontal(g31)
    c: Coincident(g32,g4)
    c: Coincident(g32,g16)
    c: Horizontal(g32)
    c: Coincident(g33,g4)
    c: Coincident(g33,g16)
    c: Horizontal(g33)
    c: Coincident(g34,g5)
    c: Coincident(g34,g17)
    c: Horizontal(g34)
    c: Coincident(g35,g5)
    c: Coincident(g35,g17)
    c: Horizontal(g35)
    c: Coincident(g36,g6)
    c: Coincident(g36,g19)
    c: Horizontal(g36)
    c: Coincident(g37,g6)
    c: Coincident(g37,g19)
    c: Horizontal(g37)
    c: Coincident(g38,g7)
    c: Coincident(g38,g18)
    c: Horizontal(g38)
    c: Coincident(g39,g7)
    c: Coincident(g39,g18)
    c: Horizontal(g39)
    c: Coincident(g40,g8)
    c: Coincident(g40,g20)
    c: Horizontal(g40)
    c: Coincident(g41,g8)
    c: Coincident(g41,g20)
    c: Horizontal(g41)
    c: Coincident(g42,g9)
    c: Coincident(g42,g23)
    c: Horizontal(g42)
    c: Coincident(g43,g9)
    c: Coincident(g43,g23)
    c: Horizontal(g43)
    c: Coincident(g44,g10)
    c: Coincident(g44,g22)
    c: Horizontal(g44)
    c: Coincident(g45,g10)
    c: Coincident(g45,g22)
    c: Horizontal(g45)
    c: Coincident(g46,g11)
    c: Coincident(g46,g21)
    c: Horizontal(g46)
    c: Coincident(g47,g11)
    c: Coincident(g47,g21)
    c: Horizontal(g47)
FEATURE [Sketcher::SketchObject] Sketch031
  FullyConstrained = true
  Placement = pos=(117,19,0) rot=(0.57735,0.57735,0.57735;2.0944rad)
  sketch-geometry (24):
    g0: ArcOfCircle CenterX=-49.19 CenterY=67.75 CenterZ=0 NormalX=0 NormalY=0 NormalZ=1 AngleXU=0 Radius=1.5 StartAngle=1.5708 EndAngle=4.71239
    g1: ArcOfCircle CenterX=-49.19 CenterY=62 CenterZ=0 NormalX=0 NormalY=0 NormalZ=1 AngleXU=0 Radius=1.5 StartAngle=1.5708 EndAngle=4.71239
    g2: ArcOfCircle CenterX=-49.19 CenterY=56.25 CenterZ=0 NormalX=0 NormalY=0 NormalZ=1 AngleXU=0 Radius=1.5 StartAngle=1.5708 EndAngle=4.71239
    g3: ArcOfCircle CenterX=-49.19 CenterY=50.5 CenterZ=0 NormalX=0 NormalY=0 NormalZ=1 AngleXU=0 Radius=1.5 StartAngle=1.5708 EndAngle=4.71239
    g4: ArcOfCircle CenterX=-49.19 CenterY=44.75 CenterZ=0 NormalX=0 NormalY=0 NormalZ=1 AngleXU=0 Radius=1.5 StartAngle=1.5708 EndAngle=4.71239
    g5: ArcOfCircle CenterX=-49.19 CenterY=39 CenterZ=0 NormalX=0 NormalY=0 NormalZ=1 AngleXU=0 Radius=1.5 StartAngle=1.5708 EndAngle=4.71239
    g6: ArcOfCircle CenterX=-49.19 CenterY=33 CenterZ=0 NormalX=0 NormalY=0 NormalZ=1 AngleXU=0 Radius=1.5 StartAngle=1.5708 EndAngle=4.71239
    g7: ArcOfCircle CenterX=-49.19 CenterY=27.25 CenterZ=0 NormalX=0 NormalY=0 NormalZ=1 AngleXU=0 Radius=1.5 StartAngle=1.5708 EndAngle=4.71239
    g8: ArcOfCircle CenterX=-49.19 CenterY=21.5 CenterZ=0 NormalX=0 NormalY=0 NormalZ=1 AngleXU=0 Radius=1.5 StartAngle=1.5708 EndAngle=4.71239
    g9: ArcOfCircle CenterX=-49.19 CenterY=15.75 CenterZ=0 NormalX=0 NormalY=0 NormalZ=1 AngleXU=0 Radius=1.5 StartAngle=1.5708 EndAngle=4.71239
    g10: ArcOfCircle CenterX=-49.19 CenterY=10 CenterZ=0 NormalX=0 NormalY=0 NormalZ=1 AngleXU=0 Radius=1.5 StartAngle=1.5708 EndAngle=4.71239
    g11: ArcOfCircle CenterX=-49.19 CenterY=4.25 CenterZ=0 NormalX=0 NormalY=0 NormalZ=1 AngleXU=0 Radius=1.5 StartAngle=1.5708 EndAngle=4.71239
    g12: LineSegment StartX=-49.19 StartY=69.25 StartZ=0 EndX=-49.19 EndY=66.25 EndZ=0
    g13: LineSegment StartX=-49.19 StartY=63.5 StartZ=0 EndX=-49.19 EndY=60.5 EndZ=0
    g14: LineSegment StartX=-49.19 StartY=57.75 StartZ=0 EndX=-49.19 EndY=54.75 EndZ=0
    g15: LineSegment StartX=-49.19 StartY=52 StartZ=0 EndX=-49.19 EndY=49 EndZ=0
    g16: LineSegment StartX=-49.19 StartY=46.25 StartZ=0 EndX=-49.19 EndY=43.25 EndZ=0
    g17: LineSegment StartX=-49.19 StartY=40.5 StartZ=0 EndX=-49.19 EndY=37.5 EndZ=0
    g18: LineSegment StartX=-49.19 StartY=34.5 StartZ=0 EndX=-49.19 EndY=31.5 EndZ=0
    g19: LineSegment StartX=-49.19 StartY=28.75 StartZ=0 EndX=-49.19 EndY=25.75 EndZ=0
    g20: LineSegment StartX=-49.19 StartY=23 StartZ=0 EndX=-49.19 EndY=20 EndZ=0
    g21: LineSegment StartX=-49.19 StartY=17.25 StartZ=0 EndX=-49.19 EndY=14.25 EndZ=0
    g22: LineSegment StartX=-49.19 StartY=11.5 StartZ=0 EndX=-49.19 EndY=8.5 EndZ=0
    g23: LineSegment StartX=-49.19 StartY=5.75 StartZ=0 EndX=-49.19 EndY=2.75 EndZ=0
  constraints (48):
    c: Block(g0)
    c: Block(g1)
    c: Block(g2)
    c: Block(g3)
    c: Block(g4)
    c: Block(g5)
    c: Block(g6)
    c: Block(g7)
    c: Block(g8)
    c: Block(g9)
    c: Block(g10)
    c: Block(g11)
    c: Coincident(g12,g0)
    c: Coincident(g12,g0)
    c: Vertical(g12)
    c: Vertical(g13)
    c: Coincident(g13,g1)
    c: Vertical(g14)
    c: Coincident(g14,g2)
    c: Vertical(g15)
    c: Coincident(g15,g3)
    c: Vertical(g16)
    c: Coincident(g16,g4)
    c: Vertical(g17)
    c: Coincident(g17,g5)
    c: Vertical(g18)
    c: Coincident(g18,g6)
    c: Vertical(g19)
    c: Coincident(g19,g7)
    c: Vertical(g20)
    c: Coincident(g20,g8)
    c: Vertical(g21)
    c: Coincident(g21,g9)
    c: Vertical(g22)
    c: Coincident(g22,g10)
    c: Vertical(g23)
    c: Coincident(g23,g11)
    c: Block(g23)
    c: Block(g22)
    c: Block(g21)
    c: Block(g20)
    c: Block(g13)
    c: Block(g14)
    c: Block(g15)
    c: Block(g16)
    c: Block(g17)
    c: Block(g18)
    c: Block(g19)
FEATURE [Part::Extrusion] Extrude022
  Base = -> Sketch030
  Dir = (1,-2e-16,2e-16)
  DirMode = 2
  FaceMakerClass = Part::FaceMakerBullseye
  LengthFwd = 19
  LengthRev = 0
  Placement = pos=(-19,0,0) rot=(0,0,1;0rad)
  Solid = true
  Symmetric = false
FEATURE [Part::Fillet] Fillet022
  Base = -> Extrude022
  Edges = 24 edges r=1.49: [Edge6,Edge11,Edge18,Edge23,Edge30,Edge35,Edge42,Edge47,Edge54,Edge59,Edge66,Edge71,Edge78,Edge83,Edge90,Edge95,Edge102,Edge107,Edge114,Edge119,Edge126,Edge131,Edge138,Edge143]
FEATURE [Part::Cut] Cut020  label="top010"
  Base = -> Cut019
  Tool = -> Fillet022
FEATURE [Sketcher::SketchObject] Sketch032
  FullyConstrained = true
  Placement = pos=(117,19,0) rot=(0.57735,0.57735,0.57735;2.0944rad)
  sketch-geometry (48):
    g0: LineSegment StartX=-49.19 StartY=69.25 StartZ=0 EndX=-49.19 EndY=66.25 EndZ=0
    g1: LineSegment StartX=-49.19 StartY=63.5 StartZ=0 EndX=-49.19 EndY=60.5 EndZ=0
    g2: LineSegment StartX=-49.19 StartY=57.75 StartZ=0 EndX=-49.19 EndY=54.75 EndZ=0
    g3: LineSegment StartX=-49.19 StartY=52 StartZ=0 EndX=-49.19 EndY=49 EndZ=0
    g4: LineSegment StartX=-49.19 StartY=46.25 StartZ=0 EndX=-49.19 EndY=43.25 EndZ=0
    g5: LineSegment StartX=-49.19 StartY=40.5 StartZ=0 EndX=-49.19 EndY=37.5 EndZ=0
    g6: LineSegment StartX=-49.19 StartY=34.5 StartZ=0 EndX=-49.19 EndY=31.5 EndZ=0
    g7: LineSegment StartX=-49.19 StartY=28.75 StartZ=0 EndX=-49.19 EndY=25.75 EndZ=0
    g8: LineSegment StartX=-49.19 StartY=23 StartZ=0 EndX=-49.19 EndY=20 EndZ=0
    g9: LineSegment StartX=-49.19 StartY=17.25 StartZ=0 EndX=-49.19 EndY=14.25 EndZ=0
    g10: LineSegment StartX=-49.19 StartY=11.5 StartZ=0 EndX=-49.19 EndY=8.5 EndZ=0
    g11: LineSegment StartX=-49.19 StartY=5.75 StartZ=0 EndX=-49.19 EndY=2.75 EndZ=0
    g12: ArcOfCircle CenterX=-1.5 CenterY=67.75 CenterZ=0 NormalX=0 NormalY=0 NormalZ=1 AngleXU=0 Radius=1.5 StartAngle=4.71239 EndAngle=7.85398
    g13: ArcOfCircle CenterX=-1.5 CenterY=62 CenterZ=0 NormalX=0 NormalY=0 NormalZ=1 AngleXU=0 Radius=1.5 StartAngle=4.71239 EndAngle=7.85398
    g14: ArcOfCircle CenterX=-1.5 CenterY=56.25 CenterZ=0 NormalX=0 NormalY=0 NormalZ=1 AngleXU=0 Radius=1.5 StartAngle=4.71239 EndAngle=7.85398
    g15: ArcOfCircle CenterX=-11.49 CenterY=50.5 CenterZ=0 NormalX=0 NormalY=0 NormalZ=1 AngleXU=0 Radius=1.5 StartAngle=4.71239 EndAngle=7.85398
    g16: ArcOfCircle CenterX=-16.28 CenterY=44.75 CenterZ=0 NormalX=0 NormalY=0 NormalZ=1 AngleXU=0 Radius=1.5 StartAngle=4.71239 EndAngle=7.85398
    g17: ArcOfCircle CenterX=-18.2337 CenterY=39 CenterZ=0 NormalX=0 NormalY=0 NormalZ=1 AngleXU=0 Radius=1.5 StartAngle=4.71485 EndAngle=7.85398
    g18: ArcOfCircle CenterX=-16.2837 CenterY=27.25 CenterZ=0 NormalX=0 NormalY=0 NormalZ=1 AngleXU=0 Radius=1.5 StartAngle=4.71485 EndAngle=7.85398
    g19: ArcOfCircle CenterX=-18.2337 CenterY=33 CenterZ=0 NormalX=0 NormalY=0 NormalZ=1 AngleXU=0 Radius=1.5 StartAngle=4.71485 EndAngle=7.85398
    g20: ArcOfCircle CenterX=-11.49 CenterY=21.5 CenterZ=0 NormalX=0 NormalY=0 NormalZ=1 AngleXU=0 Radius=1.5 StartAngle=4.71239 EndAngle=7.85398
    g21: ArcOfCircle CenterX=-1.5 CenterY=4.25 CenterZ=0 NormalX=0 NormalY=0 NormalZ=1 AngleXU=0 Radius=1.5 StartAngle=4.71239 EndAngle=7.85398
    g22: ArcOfCircle CenterX=-1.5 CenterY=10 CenterZ=0 NormalX=0 NormalY=0 NormalZ=1 AngleXU=0 Radius=1.5 StartAngle=4.71239 EndAngle=7.85398
    g23: ArcOfCircle CenterX=-1.5 CenterY=15.75 CenterZ=0 NormalX=0 NormalY=0 NormalZ=1 AngleXU=0 Radius=1.5 StartAngle=4.71239 EndAngle=7.85398
    g24: LineSegment StartX=-49.19 StartY=69.25 StartZ=0 EndX=-1.5 EndY=69.25 EndZ=0
    g25: LineSegment StartX=-49.19 StartY=66.25 StartZ=0 EndX=-1.5 EndY=66.25 EndZ=0
    g26: LineSegment StartX=-49.19 StartY=63.5 StartZ=0 EndX=-1.5 EndY=63.5 EndZ=0
    g27: LineSegment StartX=-49.19 StartY=60.5 StartZ=0 EndX=-1.5 EndY=60.5 EndZ=0
    g28: LineSegment StartX=-49.19 StartY=57.75 StartZ=0 EndX=-1.5 EndY=57.75 EndZ=0
    g29: LineSegment StartX=-49.19 StartY=54.75 StartZ=0 EndX=-1.5 EndY=54.75 EndZ=0
    g30: LineSegment StartX=-49.19 StartY=52 StartZ=0 EndX=-11.49 EndY=52 EndZ=0
    g31: LineSegment StartX=-49.19 StartY=49 StartZ=0 EndX=-11.49 EndY=49 EndZ=0
    g32: LineSegment StartX=-49.19 StartY=46.25 StartZ=0 EndX=-16.28 EndY=46.25 EndZ=0
    g33: LineSegment StartX=-49.19 StartY=43.25 StartZ=0 EndX=-16.28 EndY=43.25 EndZ=0
    g34: LineSegment StartX=-49.19 StartY=40.5 StartZ=0 EndX=-18.2337 EndY=40.5 EndZ=0
    g35: LineSegment StartX=-49.19 StartY=37.5 StartZ=0 EndX=-18.23 EndY=37.5 EndZ=0
    g36: LineSegment StartX=-49.19 StartY=34.5 StartZ=0 EndX=-18.2337 EndY=34.5 EndZ=0
    g37: LineSegment StartX=-49.19 StartY=31.5 StartZ=0 EndX=-18.23 EndY=31.5 EndZ=0
    g38: LineSegment StartX=-49.19 StartY=28.75 StartZ=0 EndX=-16.2837 EndY=28.75 EndZ=0
    g39: LineSegment StartX=-49.19 StartY=25.75 StartZ=0 EndX=-16.28 EndY=25.75 EndZ=0
    g40: LineSegment StartX=-49.19 StartY=23 StartZ=0 EndX=-11.49 EndY=23 EndZ=0
    g41: LineSegment StartX=-49.19 StartY=20 StartZ=0 EndX=-11.49 EndY=20 EndZ=0
    g42: LineSegment StartX=-49.19 StartY=17.25 StartZ=0 EndX=-1.5 EndY=17.25 EndZ=0
    g43: LineSegment StartX=-49.19 StartY=14.25 StartZ=0 EndX=-1.5 EndY=14.25 EndZ=0
    g44: LineSegment StartX=-49.19 StartY=11.5 StartZ=0 EndX=-1.5 EndY=11.5 EndZ=0
    g45: LineSegment StartX=-49.19 StartY=8.5 StartZ=0 EndX=-1.5 EndY=8.5 EndZ=0
    g46: LineSegment StartX=-49.19 StartY=5.75 StartZ=0 EndX=-1.5 EndY=5.75 EndZ=0
    g47: LineSegment StartX=-49.19 StartY=2.75 StartZ=0 EndX=-1.5 EndY=2.75 EndZ=0
  constraints (120):
    c: Vertical(g0)
    c: Distance(g0) = 3
    c: Block(g0)
    c: Vertical(g1)
    c: Distance(g1) = 3
    c: Vertical(g2)
    c: Equal(g0,g2) = 3
    c: Block(g2)
    c: Vertical(g3)
    c: Equal(g1,g3) = 3
    c: Vertical(g4)
    c: Equal(g0,g4) = 3
    c: Block(g4)
    c: Vertical(g5)
    c: Equal(g1,g5) = 3
    c: Vertical(g6)
    c: Equal(g0,g6) = 3
    c: Block(g6)
    c: Vertical(g7)
    c: Equal(g1,g7) = 3
    c: Vertical(g8)
    c: Equal(g0,g8) = 3
    c: Block(g8)
    c: Vertical(g9)
    c: Equal(g1,g9) = 3
    c: Vertical(g10)
    c: Equal(g0,g10) = 3
    c: Block(g10)
    c: Vertical(g11)
    c: Equal(g1,g11) = 3
    c: Block(g12)
    c: Block(g13)
    c: Block(g14)
    c: Block(g15)
    c: Block(g16)
    c: Block(g17)
    c: Block(g18)
    c: Block(g19)
    c: Block(g20)
    c: Block(g21)
    c: Block(g22)
    c: Block(g23)
    c: Block(g11)
    c: Block(g9)
    c: Block(g7)
    c: Block(g5)
    c: Block(g3)
    c: Block(g1)
    c: Coincident(g24,g0)
    c: Coincident(g24,g12)
    c: Horizontal(g24)
    c: Coincident(g25,g0)
    c: Coincident(g25,g12)
    c: Horizontal(g25)
    c: Coincident(g26,g1)
    c: Coincident(g26,g13)
    c: Horizontal(g26)
    c: Coincident(g27,g1)
    c: Coincident(g27,g13)
    c: Horizontal(g27)
    c: Coincident(g28,g2)
    c: Coincident(g28,g14)
    c: Horizontal(g28)
    c: Coincident(g29,g2)
    c: Coincident(g29,g14)
    c: Horizontal(g29)
    c: Coincident(g30,g3)
    c: Coincident(g30,g15)
    c: Horizontal(g30)
    c: Coincident(g31,g3)
    c: Coincident(g31,g15)
    c: Horizontal(g31)
    c: Coincident(g32,g4)
    c: Coincident(g32,g16)
    c: Horizontal(g32)
    c: Coincident(g33,g4)
    c: Coincident(g33,g16)
    c: Horizontal(g33)
    c: Coincident(g34,g5)
    c: Coincident(g34,g17)
    c: Horizontal(g34)
    c: Coincident(g35,g5)
    c: Coincident(g35,g17)
    c: Horizontal(g35)
    c: Coincident(g36,g6)
    c: Coincident(g36,g19)
    c: Horizontal(g36)
    c: Coincident(g37,g6)
    c: Coincident(g37,g19)
    c: Horizontal(g37)
    c: Coincident(g38,g7)
    c: Coincident(g38,g18)
    c: Horizontal(g38)
    c: Coincident(g39,g7)
    c: Coincident(g39,g18)
    c: Horizontal(g39)
    c: Coincident(g40,g8)
    c: Coincident(g40,g20)
    c: Horizontal(g40)
    c: Coincident(g41,g8)
    c: Coincident(g41,g20)
    c: Horizontal(g41)
    c: Coincident(g42,g9)
    c: Coincident(g42,g23)
    c: Horizontal(g42)
    c: Coincident(g43,g9)
    c: Coincident(g43,g23)
    c: Horizontal(g43)
    c: Coincident(g44,g10)
    c: Coincident(g44,g22)
    c: Horizontal(g44)
    c: Coincident(g45,g10)
    c: Coincident(g45,g22)
    c: Horizontal(g45)
    c: Coincident(g46,g11)
    c: Coincident(g46,g21)
    c: Horizontal(g46)
    c: Coincident(g47,g11)
    c: Coincident(g47,g21)
    c: Horizontal(g47)
FEATURE [Part::Extrusion] Extrude023
  Base = -> Sketch032
  Dir = (1,-2e-16,2e-16)
  DirMode = 2
  FaceMakerClass = Part::FaceMakerBullseye
  LengthFwd = 19
  LengthRev = 0
  Placement = pos=(-19,0,0) rot=(0,0,1;0rad)
  Solid = true
  Symmetric = false
FEATURE [Part::Fillet] Fillet023
  Base = -> Extrude023
  Edges = 24 edges r=1.49: [Edge6,Edge11,Edge18,Edge23,Edge30,Edge35,Edge42,Edge47,Edge54,Edge59,Edge66,Edge71,Edge78,Edge83,Edge90,Edge95,Edge102,Edge107,Edge114,Edge119,Edge126,Edge131,Edge138,Edge143]
  Placement = pos=(0,0.05,0) rot=(0,0,1;0rad)
FEATURE [Part::Cut] Cut014  label="bottom003"
  Base = -> Cut007
  Tool = -> Fusion047
FEATURE [Part::Cut] Cut021  label="bottom004"
  Base = -> Cut014
  Tool = -> Fillet023
FEATURE [Sketcher::SketchObject] Sketch033
  FullyConstrained = true
  Placement = pos=(117,19,0) rot=(0.57735,0.57735,0.57735;2.0944rad)
  sketch-geometry (8):
    g0: LineSegment StartX=-49.19 StartY=69.25 StartZ=0 EndX=-49.19 EndY=66.25 EndZ=0
    g1: LineSegment StartX=-49.19 StartY=5.75 StartZ=0 EndX=-49.19 EndY=2.75 EndZ=0
    g2: ArcOfCircle CenterX=-1.5 CenterY=67.75 CenterZ=0 NormalX=0 NormalY=0 NormalZ=1 AngleXU=0 Radius=1.5 StartAngle=4.71239 EndAngle=7.85398
    g3: ArcOfCircle CenterX=-1.5 CenterY=4.25 CenterZ=0 NormalX=0 NormalY=0 NormalZ=1 AngleXU=0 Radius=1.5 StartAngle=4.71239 EndAngle=7.85398
    g4: LineSegment StartX=-49.19 StartY=69.25 StartZ=0 EndX=-1.5 EndY=69.25 EndZ=0
    g5: LineSegment StartX=-49.19 StartY=66.25 StartZ=0 EndX=-1.5 EndY=66.25 EndZ=0
    g6: LineSegment StartX=-49.19 StartY=5.75 StartZ=0 EndX=-1.5 EndY=5.75 EndZ=0
    g7: LineSegment StartX=-49.19 StartY=2.75 StartZ=0 EndX=-1.5 EndY=2.75 EndZ=0
  constraints (19):
    c: Vertical(g0)
    c: Distance(g0) = 3
    c: Block(g0)
    c: Vertical(g1)
    c: Block(g2)
    c: Block(g3)
    c: Block(g1)
    c: Coincident(g4,g0)
    c: Coincident(g4,g2)
    c: Horizontal(g4)
    c: Coincident(g5,g0)
    c: Coincident(g5,g2)
    c: Horizontal(g5)
    c: Coincident(g6,g1)
    c: Coincident(g6,g3)
    c: Horizontal(g6)
    c: Coincident(g7,g1)
    c: Coincident(g7,g3)
    c: Horizontal(g7)
FEATURE [Sketcher::SketchObject] Sketch034
  FullyConstrained = true
  Placement = pos=(117,19,0) rot=(0.57735,0.57735,0.57735;2.0944rad)
  sketch-geometry (8):
    g0: LineSegment StartX=-49.19 StartY=63.5 StartZ=0 EndX=-49.19 EndY=60.5 EndZ=0
    g1: LineSegment StartX=-49.19 StartY=11.5 StartZ=0 EndX=-49.19 EndY=8.5 EndZ=0
    g2: ArcOfCircle CenterX=-1.5 CenterY=62 CenterZ=0 NormalX=0 NormalY=0 NormalZ=1 AngleXU=0 Radius=1.5 StartAngle=4.71239 EndAngle=7.85398
    g3: ArcOfCircle CenterX=-1.5 CenterY=10 CenterZ=0 NormalX=0 NormalY=0 NormalZ=1 AngleXU=0 Radius=1.5 StartAngle=4.71239 EndAngle=7.85398
    g4: LineSegment StartX=-49.19 StartY=63.5 StartZ=0 EndX=-1.5 EndY=63.5 EndZ=0
    g5: LineSegment StartX=-49.19 StartY=60.5 StartZ=0 EndX=-1.5 EndY=60.5 EndZ=0
    g6: LineSegment StartX=-49.19 StartY=11.5 StartZ=0 EndX=-1.5 EndY=11.5 EndZ=0
    g7: LineSegment StartX=-49.19 StartY=8.5 StartZ=0 EndX=-1.5 EndY=8.5 EndZ=0
  constraints (19):
    c: Vertical(g0)
    c: Distance(g0) = 3
    c: Vertical(g1)
    c: Block(g1)
    c: Block(g2)
    c: Block(g3)
    c: Block(g0)
    c: Coincident(g4,g0)
    c: Coincident(g4,g2)
    c: Horizontal(g4)
    c: Coincident(g5,g0)
    c: Coincident(g5,g2)
    c: Horizontal(g5)
    c: Coincident(g6,g1)
    c: Coincident(g6,g3)
    c: Horizontal(g6)
    c: Coincident(g7,g1)
    c: Coincident(g7,g3)
    c: Horizontal(g7)
FEATURE [Part::Extrusion] Extrude024
  Base = -> Sketch033
  Dir = (1,0,0)
  DirMode = 2
  FaceMakerClass = Part::FaceMakerBullseye
  LengthFwd = 10
  LengthRev = 0
  Solid = true
  Symmetric = false
FEATURE [Part::Extrusion] Extrude025
  Base = -> Sketch034
  Dir = (1,0,0)
  DirMode = 2
  FaceMakerClass = Part::FaceMakerBullseye
  LengthFwd = 10
  LengthRev = 0
  Solid = true
  Symmetric = false
FEATURE [Part::Fillet] Fillet024  label="removeFromtMoreFrontCaseScrewRetainers"
  Base = -> Extrude024
  Edges = 4 edges r=1.49: [Edge6,Edge11,Edge18,Edge23]
  Placement = pos=(-11,0,0) rot=(0,0,1;0rad)
FEATURE [Part::Fillet] Fillet025  label="removeFromtMoreFrontCaseScrewRetainers001"
  Base = -> Extrude025
  Edges = 4 edges r=1.49: [Edge6,Edge11,Edge18,Edge23]
  Placement = pos=(-19,0,0) rot=(0,0,1;0rad)
FEATURE [Part::Cut] Cut022
  Base = -> Cut015
  Tool = -> Fillet025
FEATURE [Part::Cut] Cut023  label="screwRetainers"
  Base = -> Cut022
  Tool = -> Fillet024
FEATURE [Part::MultiFuse] Fusion056  label="bottom005"
  Shapes = -> [Fusion044,Cut021]
FEATURE [Part::MultiFuse] Fusion057  label="casePillars001"
  Shapes = -> [Cut016,Fusion052]
FEATURE [Part::MultiFuse] Fusion058  label="bottom006"
  Shapes = -> [Fusion056,Cut023]
FEATURE [Part::MultiFuse] Fusion059  label="bottom007"
  Shapes = -> [Fusion058,Fillet005]
FEATURE [Part::MultiFuse] Fusion060  label="bottom008"
  Shapes = -> [Fusion059,Fusion]
FEATURE [Part::MultiFuse] Fusion061  label="top011"
  Shapes = -> [Cut006,Cut020]
FEATURE [Part::MultiFuse] Fusion062  label="top012"
  Shapes = -> [Fusion057,Fusion061]
FEATURE [Sketcher::SketchObject] Sketch035  label="topSketch007"
  FullyConstrained = true
  sketch-geometry (6):
    g0: LineSegment StartX=19 StartY=38 StartZ=0 EndX=117 EndY=38 EndZ=0
    g1: ArcOfCircle CenterX=19 CenterY=19 CenterZ=0 NormalX=0 NormalY=0 NormalZ=1 AngleXU=0 Radius=19 StartAngle=1.5708 EndAngle=3.14159
    g2: LineSegment StartX=117 StartY=38 StartZ=0 EndX=117 EndY=19 EndZ=0
    g3: LineSegment StartX=98 StartY=1.0161e-12 StartZ=0 EndX=5.22862e-06 EndY=1.0161e-12 EndZ=0
    g4: LineSegment StartX=5.22862e-06 StartY=19 StartZ=0 EndX=5.22862e-06 EndY=1.0161e-12 EndZ=0
    g5: ArcOfCircle CenterX=98 CenterY=19 CenterZ=0 NormalX=0 NormalY=0 NormalZ=1 AngleXU=0 Radius=19 StartAngle=4.71239 EndAngle=6.28319
  constraints (16):
    c: Horizontal(g0)
    c: Distance(g0) = 98
    c: Coincident(g1,g0)
    c: Block(g1)
    c: Coincident(g2,g0)
    c: Vertical(g2)
    c: Distance(g2) = 19
    c: Horizontal(g3)
    c: Coincident(g4,g1)
    c: Vertical(g4)
    c: Coincident(g3,g4)
    c: Block(g3)
    c: Coincident(g5,g2)
    c: Coincident(g5,g3)
    c: Block(g0)
    c: Block(g5)
FEATURE [Part::Extrusion] Extrude026  label="sideA001"
  Base = -> Sketch035
  Dir = (0,0,1)
  DirMode = 2
  FaceMakerClass = Part::FaceMakerBullseye
  LengthFwd = 3
  LengthRev = 0
  Placement = pos=(0,0,-2.7) rot=(0,0,1;0rad)
  Solid = true
  Symmetric = false
FEATURE [Sketcher::SketchObject] Sketch036  label="topSketch008"
  FullyConstrained = true
  sketch-geometry (6):
    g0: LineSegment StartX=19 StartY=38 StartZ=0 EndX=117 EndY=38 EndZ=0
    g1: ArcOfCircle CenterX=19 CenterY=19 CenterZ=0 NormalX=0 NormalY=0 NormalZ=1 AngleXU=0 Radius=19 StartAngle=1.5708 EndAngle=3.14159
    g2: LineSegment StartX=117 StartY=38 StartZ=0 EndX=117 EndY=19 EndZ=0
    g3: LineSegment StartX=98 StartY=1.0161e-12 StartZ=0 EndX=5.22862e-06 EndY=1.0161e-12 EndZ=0
    g4: LineSegment StartX=5.22862e-06 StartY=19 StartZ=0 EndX=5.22862e-06 EndY=1.0161e-12 EndZ=0
    g5: ArcOfCircle CenterX=98 CenterY=19 CenterZ=0 NormalX=0 NormalY=0 NormalZ=1 AngleXU=0 Radius=19 StartAngle=4.71239 EndAngle=6.28319
  constraints (16):
    c: Horizontal(g0)
    c: Distance(g0) = 98
    c: Coincident(g1,g0)
    c: Block(g1)
    c: Coincident(g2,g0)
    c: Vertical(g2)
    c: Distance(g2) = 19
    c: Horizontal(g3)
    c: Coincident(g4,g1)
    c: Vertical(g4)
    c: Coincident(g3,g4)
    c: Block(g3)
    c: Coincident(g5,g2)
    c: Coincident(g5,g3)
    c: Block(g0)
    c: Block(g5)
FEATURE [Part::Extrusion] Extrude027  label="sideB001"
  Base = -> Sketch036
  Dir = (0,0,1)
  DirMode = 2
  FaceMakerClass = Part::FaceMakerBullseye
  LengthFwd = 3
  LengthRev = 0
  Placement = pos=(0,0,71.7) rot=(0,0,1;0rad)
  Solid = true
  Symmetric = false
FEATURE [Part::MultiFuse] Fusion064  label="removeFromBottom"
  Shapes = -> [Extrude026,Extrude027]
FEATURE [Part::Cut] Cut024  label="bottom009"
  Base = -> Fusion060
  Tool = -> Fusion064
FEATURE [Sketcher::SketchObject] Sketch037  label="topSketch009"
  FullyConstrained = true
  sketch-geometry (6):
    g0: ArcOfCircle CenterX=19 CenterY=19 CenterZ=0 NormalX=0 NormalY=0 NormalZ=1 AngleXU=0 Radius=19 StartAngle=1.5708 EndAngle=3.14159
    g1: LineSegment StartX=5.22862e-06 StartY=19 StartZ=0 EndX=5.22862e-06 EndY=1.19904e-11 EndZ=0
    g2: LineSegment StartX=19 StartY=38 StartZ=0 EndX=124 EndY=38 EndZ=0
    g3: LineSegment StartX=5.22862e-06 StartY=1.19904e-11 StartZ=0 EndX=105 EndY=1.19904e-11 EndZ=0
    g4: ArcOfCircle CenterX=105 CenterY=19 CenterZ=0 NormalX=0 NormalY=0 NormalZ=1 AngleXU=0 Radius=19 StartAngle=4.71239 EndAngle=6.28319
    g5: LineSegment StartX=124 StartY=38 StartZ=0 EndX=124 EndY=19 EndZ=0
  constraints (16):
    c: Block(g0)
    c: Coincident(g1,g0)
    c: Vertical(g1)
    c: Horizontal(g2)
    c: Distance(g2) = 105
    c: Coincident(g2,g0)
    c: Distance(g1) = 19
    c: Coincident(g3,g1)
    c: Horizontal(g3)
    c: Distance(g3) = 105
    c: Block(g4)
    c: Coincident(g4,g3)
    c: Coincident(g5,g2)
    c: Coincident(g5,g4)
    c: Vertical(g5)
    c: Distance(g5) = 19
FEATURE [Part::Extrusion] Extrude028  label="sideB"
  Base = -> Sketch037
  Dir = (0,0,1)
  DirMode = 2
  FaceMakerClass = Part::FaceMakerBullseye
  LengthFwd = 3
  LengthRev = 0
  Placement = pos=(0,0,72) rot=(0,0,1;0rad)
  Solid = true
  Symmetric = false
FEATURE [Sketcher::SketchObject] Sketch038  label="topSketch010"
  FullyConstrained = true
  sketch-geometry (20):
    g0: LineSegment StartX=5.21097e-06 StartY=3 StartZ=0 EndX=5.21097e-06 EndY=19 EndZ=0
    g1: ArcOfCircle CenterX=19 CenterY=19 CenterZ=0 NormalX=0 NormalY=0 NormalZ=1 AngleXU=0 Radius=19 StartAngle=1.5708 EndAngle=3.14159
    g2: ArcOfCircle CenterX=19 CenterY=19 CenterZ=0 NormalX=0 NormalY=0 NormalZ=1 AngleXU=0 Radius=16 StartAngle=1.5708 EndAngle=3.14159
    g3: LineSegment StartX=114 StartY=35 StartZ=0 EndX=19 EndY=35 EndZ=0
    g4: LineSegment StartX=5.21097e-06 StartY=3 StartZ=0 EndX=5.21097e-06 EndY=0 EndZ=0
    g5: LineSegment StartX=3 StartY=0 StartZ=0 EndX=5.21097e-06 EndY=0 EndZ=0
    g6: LineSegment StartX=3 StartY=19 StartZ=0 EndX=3 EndY=0 EndZ=0
    g7: LineSegment StartX=19 StartY=38 StartZ=0 EndX=124 EndY=38 EndZ=0
    g8: Circle CenterX=119 CenterY=35 CenterZ=0 NormalX=0 NormalY=0 NormalZ=1 AngleXU=0 Radius=1
    g9: Circle CenterX=121 CenterY=35 CenterZ=0 NormalX=0 NormalY=0 NormalZ=1 AngleXU=0 Radius=1
    g10: Circle CenterX=121 CenterY=33 CenterZ=0 NormalX=0 NormalY=0 NormalZ=1 AngleXU=0 Radius=1
    g11: BSplineCurve PolesCount=3 KnotsCount=2 Degree=2 IsPeriodic=0
    g12: GeomPoint X=119 Y=35 Z=0
    g13: GeomPoint X=121 Y=33 Z=0
    g14: LineSegment StartX=119 StartY=35 StartZ=0 EndX=114 EndY=35 EndZ=0
    g15: ArcOfCircle CenterX=105 CenterY=19 CenterZ=0 NormalX=0 NormalY=0 NormalZ=1 AngleXU=0 Radius=19 StartAngle=5.7297 EndAngle=6.28319
    g16: ArcOfCircle CenterX=105 CenterY=19 CenterZ=0 NormalX=0 NormalY=0 NormalZ=1 AngleXU=0 Radius=16 StartAngle=5.60905 EndAngle=6.28319
    g17: LineSegment StartX=121 StartY=33 StartZ=0 EndX=121 EndY=19 EndZ=0
    g18: LineSegment StartX=124 StartY=38 StartZ=0 EndX=124 EndY=19 EndZ=0
    g19: LineSegment StartX=117.5 StartY=9.01251 StartZ=0 EndX=121.163 EndY=9.0125 EndZ=0
  constraints (46):
    c: Vertical(g0)
    c: Block(g0)
    c: Coincident(g1,g0)
    c: Block(g1)
    c: Coincident(g2,g1)
    c: Block(g2)
    c: Coincident(g3,g2)
    c: Horizontal(g3)
    c: Tangent(g3,g2)
    c: Coincident(g4,g0)
    c: Distance(g4) = 3
    c: Vertical(g4)
    c: Coincident(g5,g4)
    c: Horizontal(g5)
    c: Coincident(g6,g2)
    c: Coincident(g6,g5)
    c: Vertical(g6)
    c: Horizontal(g7)
    c: Distance(g7) = 105
    c: Coincident(g7,g1)
    c: Block(g3)
    c: Weight(g8) = 1
    c: Equal(g8,g9)
    c: Equal(g8,g10)
    c: InternalAlignment(g8,g11)
    c: InternalAlignment(g9,g11)
    c: InternalAlignment(g10,g11)
    c: InternalAlignment(g12,g11)
    c: InternalAlignment(g13,g11)
    c: Block(g11)
    c: Coincident(g14,g11)
    c: Coincident(g14,g3)
    c: Horizontal(g14)
    c: Block(g15)
    c: Coincident(g16,g15)
    c: Block(g16)
    c: Coincident(g17,g11)
    c: Coincident(g17,g16)
    c: Vertical(g17)
    c: Distance(g17) = 14
    c: Coincident(g18,g7)
    c: Coincident(g18,g15)
    c: Vertical(g18)
    c: Distance(g18) = 19
    c: Coincident(g19,g16)
    c: Coincident(g19,g15)
FEATURE [Part::Extrusion] Extrude029
  Base = -> Sketch038
  Dir = (0,0,1)
  DirMode = 2
  FaceMakerClass = Part::FaceMakerBullseye
  LengthFwd = 72
  LengthRev = 0
  Solid = true
  Symmetric = false
FEATURE [Part::Feature] Face085
  shape: bbox 4.8 x 25.5 x 2e-07 mm, 1 faces, 0 solids (baked)
FEATURE [Part::Revolution] Revolve089  label="moreFrontCaseScrewPost003"
  Angle = 360
  Axis = (0,1,0)
  Base = (0,0,0)
  FaceMakerClass = Part::FaceMakerBullseye
  Placement = pos=(109.5,4.5,3.5) rot=(0,0,1;0rad)
  Solid = false
  Source = -> Face085
  Symmetric = false
FEATURE [Part::Feature] Face086
  shape: bbox 4.8 x 25.5 x 2e-07 mm, 1 faces, 0 solids (baked)
FEATURE [Part::Revolution] Revolve090  label="moreFrontCaseScrewPost004"
  Angle = 360
  Axis = (0,1,0)
  Base = (0,0,0)
  FaceMakerClass = Part::FaceMakerBullseye
  Placement = pos=(109.5,4.5,68.5) rot=(0,0,1;0rad)
  Solid = false
  Source = -> Face086
  Symmetric = false
FEATURE [Part::Fillet] Fillet026
  Base = -> Extrude029
  Edges = 1 edges r=2: [Edge35]
FEATURE [Sketcher::SketchObject] Sketch039
  FullyConstrained = true
  sketch-geometry (7):
    g0: LineSegment StartX=0 StartY=0 StartZ=0 EndX=0 EndY=6 EndZ=0
    g1: Circle CenterX=0 CenterY=0 CenterZ=0 NormalX=0 NormalY=0 NormalZ=1 AngleXU=0 Radius=1
    g2: Circle CenterX=8 CenterY=6 CenterZ=0 NormalX=0 NormalY=0 NormalZ=1 AngleXU=0 Radius=1
    g3: BSplineCurve PolesCount=3 KnotsCount=2 Degree=2 IsPeriodic=0
    g4: GeomPoint X=0 Y=0 Z=0
    g5: GeomPoint X=8 Y=6 Z=0
    g6: LineSegment StartX=0 StartY=6 StartZ=0 EndX=8 EndY=6 EndZ=0
  constraints (14):
    c: Coincident(g0,g-1)
    c: Distance(g0) = 6
    c: Vertical(g0)
    c: Coincident(g3,g0)
    c: Weight(g1) = 1
    c: Equal(g1,g2)
    c: InternalAlignment(g1,g3)
    c: InternalAlignment(g2,g3)
    c: InternalAlignment(g4,g3)
    c: InternalAlignment(g5,g3)
    c: Block(g3)
    c: Coincident(g6,g0)
    c: Coincident(g6,g3)
    c: Horizontal(g6)
FEATURE [Sketcher::SketchObject] Sketch040
  FullyConstrained = true
  sketch-geometry (7):
    g0: LineSegment StartX=0 StartY=0 StartZ=0 EndX=0 EndY=6 EndZ=0
    g1: Circle CenterX=0 CenterY=0 CenterZ=0 NormalX=0 NormalY=0 NormalZ=1 AngleXU=0 Radius=1
    g2: Circle CenterX=8 CenterY=6 CenterZ=0 NormalX=0 NormalY=0 NormalZ=1 AngleXU=0 Radius=1
    g3: BSplineCurve PolesCount=3 KnotsCount=2 Degree=2 IsPeriodic=0
    g4: GeomPoint X=0 Y=0 Z=0
    g5: GeomPoint X=8 Y=6 Z=0
    g6: LineSegment StartX=0 StartY=6 StartZ=0 EndX=8 EndY=6 EndZ=0
  constraints (14):
    c: Coincident(g0,g-1)
    c: Distance(g0) = 6
    c: Vertical(g0)
    c: Coincident(g3,g0)
    c: Weight(g1) = 1
    c: Equal(g1,g2)
    c: InternalAlignment(g1,g3)
    c: InternalAlignment(g2,g3)
    c: InternalAlignment(g4,g3)
    c: InternalAlignment(g5,g3)
    c: Block(g3)
    c: Coincident(g6,g0)
    c: Coincident(g6,g3)
    c: Horizontal(g6)
FEATURE [Sketcher::SketchObject] Sketch041
  FullyConstrained = true
  sketch-geometry (7):
    g0: LineSegment StartX=0 StartY=0 StartZ=0 EndX=0 EndY=6 EndZ=0
    g1: Circle CenterX=0 CenterY=0 CenterZ=0 NormalX=0 NormalY=0 NormalZ=1 AngleXU=0 Radius=1
    g2: Circle CenterX=8 CenterY=6 CenterZ=0 NormalX=0 NormalY=0 NormalZ=1 AngleXU=0 Radius=1
    g3: BSplineCurve PolesCount=3 KnotsCount=2 Degree=2 IsPeriodic=0
    g4: GeomPoint X=0 Y=0 Z=0
    g5: GeomPoint X=8 Y=6 Z=0
    g6: LineSegment StartX=0 StartY=6 StartZ=0 EndX=8 EndY=6 EndZ=0
  constraints (14):
    c: Coincident(g0,g-1)
    c: Distance(g0) = 6
    c: Vertical(g0)
    c: Coincident(g3,g0)
    c: Weight(g1) = 1
    c: Equal(g1,g2)
    c: InternalAlignment(g1,g3)
    c: InternalAlignment(g2,g3)
    c: InternalAlignment(g4,g3)
    c: InternalAlignment(g5,g3)
    c: Block(g3)
    c: Coincident(g6,g0)
    c: Coincident(g6,g3)
    c: Horizontal(g6)
FEATURE [Sketcher::SketchObject] Sketch042
  FullyConstrained = true
  sketch-geometry (7):
    g0: LineSegment StartX=0 StartY=0 StartZ=0 EndX=0 EndY=6 EndZ=0
    g1: Circle CenterX=0 CenterY=0 CenterZ=0 NormalX=0 NormalY=0 NormalZ=1 AngleXU=0 Radius=1
    g2: Circle CenterX=8 CenterY=6 CenterZ=0 NormalX=0 NormalY=0 NormalZ=1 AngleXU=0 Radius=1
    g3: BSplineCurve PolesCount=3 KnotsCount=2 Degree=2 IsPeriodic=0
    g4: GeomPoint X=0 Y=0 Z=0
    g5: GeomPoint X=8 Y=6 Z=0
    g6: LineSegment StartX=0 StartY=6 StartZ=0 EndX=8 EndY=6 EndZ=0
  constraints (14):
    c: Coincident(g0,g-1)
    c: Distance(g0) = 6
    c: Vertical(g0)
    c: Coincident(g3,g0)
    c: Weight(g1) = 1
    c: Equal(g1,g2)
    c: InternalAlignment(g1,g3)
    c: InternalAlignment(g2,g3)
    c: InternalAlignment(g4,g3)
    c: InternalAlignment(g5,g3)
    c: Block(g3)
    c: Coincident(g6,g0)
    c: Coincident(g6,g3)
    c: Horizontal(g6)
FEATURE [Part::Extrusion] Extrude030  label="caseScrewPillarBracket008"
  Base = -> Sketch039
  Dir = (0,0,1)
  DirMode = 2
  FaceMakerClass = Part::FaceMakerBullseye
  LengthFwd = 2.4
  LengthRev = 0
  Placement = pos=(15.76,29,8.8) rot=(0,1,0;0rad)
  Solid = true
  Symmetric = false
FEATURE [Part::Extrusion] Extrude031  label="caseScrewPillarBracket009"
  Base = -> Sketch040
  Dir = (0,0,1)
  DirMode = 2
  FaceMakerClass = Part::FaceMakerBullseye
  LengthFwd = 2.4
  LengthRev = 0
  Placement = pos=(15.76,29,60.8) rot=(0,0,1;0rad)
  Solid = true
  Symmetric = false
FEATURE [Part::Extrusion] Extrude032  label="caseScrewPillarBracket010"
  Base = -> Sketch041
  Dir = (0,0,1)
  DirMode = 2
  FaceMakerClass = Part::FaceMakerBullseye
  LengthFwd = 2.4
  LengthRev = 0
  Placement = pos=(13.7,29,13.26) rot=(0,-1,0;1.5708rad)
  Solid = true
  Symmetric = false
FEATURE [Part::Extrusion] Extrude033  label="caseScrewPillarBracket011"
  Base = -> Sketch042
  Dir = (0,0,1)
  DirMode = 2
  FaceMakerClass = Part::FaceMakerBullseye
  LengthFwd = 2.4
  LengthRev = 0
  Placement = pos=(11.3,29,58.74) rot=(0,1,0;1.5708rad)
  Solid = true
  Symmetric = false
FEATURE [Sketcher::SketchObject] Sketch043
  FullyConstrained = true
  sketch-geometry (7):
    g0: LineSegment StartX=0 StartY=0 StartZ=0 EndX=0 EndY=6 EndZ=0
    g1: Circle CenterX=0 CenterY=0 CenterZ=0 NormalX=0 NormalY=0 NormalZ=1 AngleXU=0 Radius=1
    g2: Circle CenterX=8 CenterY=6 CenterZ=0 NormalX=0 NormalY=0 NormalZ=1 AngleXU=0 Radius=1
    g3: BSplineCurve PolesCount=3 KnotsCount=2 Degree=2 IsPeriodic=0
    g4: GeomPoint X=0 Y=0 Z=0
    g5: GeomPoint X=8 Y=6 Z=0
    g6: LineSegment StartX=0 StartY=6 StartZ=0 EndX=8 EndY=6 EndZ=0
  constraints (14):
    c: Coincident(g0,g-1)
    c: Distance(g0) = 6
    c: Vertical(g0)
    c: Coincident(g3,g0)
    c: Weight(g1) = 1
    c: Equal(g1,g2)
    c: InternalAlignment(g1,g3)
    c: InternalAlignment(g2,g3)
    c: InternalAlignment(g4,g3)
    c: InternalAlignment(g5,g3)
    c: Block(g3)
    c: Coincident(g6,g0)
    c: Coincident(g6,g3)
    c: Horizontal(g6)
FEATURE [Part::Extrusion] Extrude034  label="caseScrewPillarBracket012"
  Base = -> Sketch043
  Dir = (0,0,1)
  DirMode = 2
  FaceMakerClass = Part::FaceMakerBullseye
  LengthFwd = 2.4
  LengthRev = 0
  Placement = pos=(88.3,29,65.23) rot=(0,1,0;1.5708rad)
  Solid = true
  Symmetric = false
FEATURE [Sketcher::SketchObject] Sketch044
  FullyConstrained = true
  sketch-geometry (7):
    g0: LineSegment StartX=0 StartY=0 StartZ=0 EndX=0 EndY=6 EndZ=0
    g1: Circle CenterX=0 CenterY=0 CenterZ=0 NormalX=0 NormalY=0 NormalZ=1 AngleXU=0 Radius=1
    g2: Circle CenterX=8 CenterY=6 CenterZ=0 NormalX=0 NormalY=0 NormalZ=1 AngleXU=0 Radius=1
    g3: BSplineCurve PolesCount=3 KnotsCount=2 Degree=2 IsPeriodic=0
    g4: GeomPoint X=0 Y=0 Z=0
    g5: GeomPoint X=8 Y=6 Z=0
    g6: LineSegment StartX=0 StartY=6 StartZ=0 EndX=8 EndY=6 EndZ=0
  constraints (14):
    c: Coincident(g0,g-1)
    c: Distance(g0) = 6
    c: Vertical(g0)
    c: Coincident(g3,g0)
    c: Weight(g1) = 1
    c: Equal(g1,g2)
    c: InternalAlignment(g1,g3)
    c: InternalAlignment(g2,g3)
    c: InternalAlignment(g4,g3)
    c: InternalAlignment(g5,g3)
    c: Block(g3)
    c: Coincident(g6,g0)
    c: Coincident(g6,g3)
    c: Horizontal(g6)
FEATURE [Part::Extrusion] Extrude035  label="caseScrewPillarBracket013"
  Base = -> Sketch044
  Dir = (0,0,1)
  DirMode = 2
  FaceMakerClass = Part::FaceMakerBullseye
  LengthFwd = 2.4
  LengthRev = 0
  Placement = pos=(90.7,29,6.77) rot=(0,-1,0;1.5708rad)
  Solid = true
  Symmetric = false
FEATURE [Sketcher::SketchObject] Sketch045
  FullyConstrained = true
  sketch-geometry (7):
    g0: LineSegment StartX=0 StartY=0 StartZ=0 EndX=0 EndY=6 EndZ=0
    g1: Circle CenterX=0 CenterY=0 CenterZ=0 NormalX=0 NormalY=0 NormalZ=1 AngleXU=0 Radius=1
    g2: Circle CenterX=8 CenterY=6 CenterZ=0 NormalX=0 NormalY=0 NormalZ=1 AngleXU=0 Radius=1
    g3: BSplineCurve PolesCount=3 KnotsCount=2 Degree=2 IsPeriodic=0
    g4: GeomPoint X=0 Y=0 Z=0
    g5: GeomPoint X=8 Y=6 Z=0
    g6: LineSegment StartX=0 StartY=6 StartZ=0 EndX=8 EndY=6 EndZ=0
  constraints (14):
    c: Coincident(g0,g-1)
    c: Distance(g0) = 6
    c: Vertical(g0)
    c: Coincident(g3,g0)
    c: Weight(g1) = 1
    c: Equal(g1,g2)
    c: InternalAlignment(g1,g3)
    c: InternalAlignment(g2,g3)
    c: InternalAlignment(g4,g3)
    c: InternalAlignment(g5,g3)
    c: Block(g3)
    c: Coincident(g6,g0)
    c: Coincident(g6,g3)
    c: Horizontal(g6)
FEATURE [Sketcher::SketchObject] Sketch046
  FullyConstrained = true
  sketch-geometry (7):
    g0: LineSegment StartX=0 StartY=0 StartZ=0 EndX=0 EndY=6 EndZ=0
    g1: Circle CenterX=0 CenterY=0 CenterZ=0 NormalX=0 NormalY=0 NormalZ=1 AngleXU=0 Radius=1
    g2: Circle CenterX=8 CenterY=6 CenterZ=0 NormalX=0 NormalY=0 NormalZ=1 AngleXU=0 Radius=1
    g3: BSplineCurve PolesCount=3 KnotsCount=2 Degree=2 IsPeriodic=0
    g4: GeomPoint X=0 Y=0 Z=0
    g5: GeomPoint X=8 Y=6 Z=0
    g6: LineSegment StartX=0 StartY=6 StartZ=0 EndX=8 EndY=6 EndZ=0
  constraints (14):
    c: Coincident(g0,g-1)
    c: Distance(g0) = 6
    c: Vertical(g0)
    c: Coincident(g3,g0)
    c: Weight(g1) = 1
    c: Equal(g1,g2)
    c: InternalAlignment(g1,g3)
    c: InternalAlignment(g2,g3)
    c: InternalAlignment(g4,g3)
    c: InternalAlignment(g5,g3)
    c: Block(g3)
    c: Coincident(g6,g0)
    c: Coincident(g6,g3)
    c: Horizontal(g6)
FEATURE [Part::Extrusion] Extrude036  label="caseScrewPillarBracket014"
  Base = -> Sketch045
  Dir = (0,0,1)
  DirMode = 2
  FaceMakerClass = Part::FaceMakerBullseye
  LengthFwd = 2.4
  LengthRev = 0
  Placement = pos=(110.7,29,6.77) rot=(0,-1,0;1.5708rad)
  Solid = true
  Symmetric = false
FEATURE [Part::Extrusion] Extrude037  label="caseScrewPillarBracket015"
  Base = -> Sketch046
  Dir = (0,0,1)
  DirMode = 2
  FaceMakerClass = Part::FaceMakerBullseye
  LengthFwd = 2.4
  LengthRev = 0
  Placement = pos=(108.3,29,65.23) rot=(0,1,0;1.5708rad)
  Solid = true
  Symmetric = false
FEATURE [Part::Box] Box013  label="frontCaseScrewPillarBracket002"
  AttacherType = Attacher::AttachEngine3D
  Height = 2.4
  Length = 22
  Placement = pos=(87,28,2.3) rot=(0,0,1;0rad)
  Width = 7
FEATURE [Part::Box] Box014  label="frontCaseScrewPillarBracket003"
  AttacherType = Attacher::AttachEngine3D
  Height = 2.4
  Length = 22
  Placement = pos=(87,28,67.3) rot=(0,0,1;0rad)
  Width = 7
FEATURE [Part::Feature] Face087
  shape: bbox 4.8 x 30.2 x 2e-07 mm, 1 faces, 0 solids (baked)
FEATURE [Part::Revolution] Revolve091  label="frontCaseScrewPost004"
  Angle = 360
  Axis = (0,1,0)
  Base = (0,0,0)
  FaceMakerClass = Part::FaceMakerBullseye
  Placement = pos=(89.5,4.5,3.5) rot=(0,0,1;0rad)
  Solid = false
  Source = -> Face087
  Symmetric = false
FEATURE [Part::Feature] Face088
  shape: bbox 4.8 x 30.2 x 2e-07 mm, 1 faces, 0 solids (baked)
FEATURE [Part::Revolution] Revolve092  label="frontCaseScrewPost005"
  Angle = 360
  Axis = (0,1,0)
  Base = (0,0,0)
  FaceMakerClass = Part::FaceMakerBullseye
  Placement = pos=(89.5,4.5,68.5) rot=(0,0,1;0rad)
  Solid = false
  Source = -> Face088
  Symmetric = false
FEATURE [Part::Feature] Face089
  shape: bbox 3.5 x 30.2 x 2e-07 mm, 1 faces, 0 solids (baked)
FEATURE [Part::Revolution] Revolve093  label="backCaseScrewPost002"
  Angle = 360
  Axis = (0,1,0)
  Base = (0,0,0)
  FaceMakerClass = Part::FaceMakerBullseye
  Placement = pos=(12.5,4.5,10) rot=(0,0,1;0rad)
  Solid = false
  Source = -> Face089
  Symmetric = false
FEATURE [Part::Feature] Face090
  shape: bbox 3.5 x 30.2 x 2e-07 mm, 1 faces, 0 solids (baked)
FEATURE [Part::Revolution] Revolve094  label="backCaseScrewPost003"
  Angle = 360
  Axis = (0,1,0)
  Base = (0,0,0)
  FaceMakerClass = Part::FaceMakerBullseye
  Placement = pos=(12.5,4.5,62) rot=(0,0,1;0rad)
  Solid = false
  Source = -> Face090
  Symmetric = false
FEATURE [Part::Box] Box015  label="Cube011"
  AttacherType = Attacher::AttachEngine3D
  Height = 28.8
  Length = 3
  Placement = pos=(107.3,28,21.6) rot=(0,0,1;0rad)
  Width = 7
FEATURE [Part::Box] Box016  label="Cube012"
  AttacherType = Attacher::AttachEngine3D
  Height = 3
  Length = 6.4
  Placement = pos=(107.3,28,18.6) rot=(0,0,1;0rad)
  Width = 7
FEATURE [Part::Box] Box017  label="Cube013"
  AttacherType = Attacher::AttachEngine3D
  Height = 3
  Length = 6.4
  Placement = pos=(107.3,28,50.4) rot=(0,0,1;0rad)
  Width = 7
FEATURE [Part::MultiFuse] Fusion065  label="plugHousingBracketHolder002"
  Shapes = -> [Box017,Box015,Box016]
FEATURE [Part::Cylinder] Cylinder024
  Angle = 360
  AttacherType = Attacher::AttachEngine3D
  Height = 20
  Placement = pos=(0,0,36.15) rot=(0,0,1;0rad)
  Radius = 14.3
FEATURE [Part::Cylinder] Cylinder025
  Angle = 360
  AttacherType = Attacher::AttachEngine3D
  Height = 10
  Placement = pos=(0,0,36.15) rot=(0,0,1;0rad)
  Radius = 4
FEATURE [Part::MultiFuse] Fusion066  label="removeToCreteHoleForPlugHousing009"
  Placement = pos=(70,19,36) rot=(0,1,0;1.5708rad)
  Shapes = -> [Cylinder024,Cylinder025]
FEATURE [Part::Cut] Cut025  label="plugHousingBracketHolder003"
  Base = -> Fusion065
  Placement = pos=(7,0,0) rot=(0,0,1;0rad)
  Tool = -> Fusion066
FEATURE [Part::Feature] Face091
  shape: bbox 10 x 16.5 x 2e-07 mm, 1 faces, 0 solids (baked)
FEATURE [Part::Feature] Face092
  shape: bbox 10 x 16.5 x 2e-07 mm, 1 faces, 0 solids (baked)
FEATURE [Part::Feature] Face093
  shape: bbox 10 x 16.5 x 2e-07 mm, 1 faces, 0 solids (baked)
FEATURE [Part::Revolution] Revolve095  label="plugHousing049"
  Angle = 360
  Axis = (0,1,0)
  Base = (0,0,0)
  FaceMakerClass = Part::FaceMakerBullseye
  Placement = pos=(0,0,36.15) rot=(0,0,1;0rad)
  Solid = false
  Source = -> Face091
  Symmetric = false
FEATURE [Part::Revolution] Revolve096  label="plugHousing050"
  Angle = 360
  Axis = (0,1,0)
  Base = (0,0,0)
  FaceMakerClass = Part::FaceMakerBullseye
  Placement = pos=(0,0,36.15) rot=(0,0,1;0rad)
  Solid = false
  Source = -> Face092
  Symmetric = false
FEATURE [Part::MultiFuse] Fusion067  label="plugHousing047"
  Placement = pos=(0,0,0) rot=(0,0,1;1.5708rad)
  Shapes = -> [Revolve096,Revolve095]
FEATURE [Part::Revolution] Revolve098  label="plugHousing052"
  Angle = 360
  Axis = (0,1,0)
  Base = (0,0,0)
  FaceMakerClass = Part::FaceMakerBullseye
  Placement = pos=(0,0,36.15) rot=(0,0,1;0rad)
  Solid = false
  Source = -> Face093
  Symmetric = false
FEATURE [Part::Feature] Face094
  shape: bbox 10 x 16.5 x 2e-07 mm, 1 faces, 0 solids (baked)
FEATURE [Part::Revolution] Revolve097  label="plugHousing051"
  Angle = 360
  Axis = (0,1,0)
  Base = (0,0,0)
  FaceMakerClass = Part::FaceMakerBullseye
  Placement = pos=(0,0,36.15) rot=(0,0,1;0rad)
  Solid = false
  Source = -> Face094
  Symmetric = false
FEATURE [Part::MultiFuse] Fusion068  label="plugHousing048"
  Placement = pos=(0,0,0) rot=(0,0,1;1.5708rad)
  Shapes = -> [Revolve097,Revolve098]
FEATURE [Part::Feature] Face095
  shape: bbox 10 x 16.5 x 2e-07 mm, 1 faces, 0 solids (baked)
FEATURE [Part::Revolution] Revolve101  label="plugHousing055"
  Angle = 360
  Axis = (0,1,0)
  Base = (0,0,0)
  FaceMakerClass = Part::FaceMakerBullseye
  Placement = pos=(0,0,36.15) rot=(0,0,1;0rad)
  Solid = false
  Source = -> Face095
  Symmetric = false
FEATURE [Part::Feature] Face096
  shape: bbox 10 x 16.5 x 2e-07 mm, 1 faces, 0 solids (baked)
FEATURE [Part::Revolution] Revolve102  label="plugHousing056"
  Angle = 360
  Axis = (0,1,0)
  Base = (0,0,0)
  FaceMakerClass = Part::FaceMakerBullseye
  Placement = pos=(0,0,36.15) rot=(0,0,1;0rad)
  Solid = false
  Source = -> Face096
  Symmetric = false
FEATURE [Part::Feature] Face097
  shape: bbox 10 x 16.5 x 2e-07 mm, 1 faces, 0 solids (baked)
FEATURE [Part::Revolution] Revolve099  label="plugHousing053"
  Angle = 360
  Axis = (0,1,0)
  Base = (0,0,0)
  FaceMakerClass = Part::FaceMakerBullseye
  Placement = pos=(0,0,36.15) rot=(0,0,1;0rad)
  Solid = false
  Source = -> Face097
  Symmetric = false
FEATURE [Part::Feature] Face098
  shape: bbox 10 x 16.5 x 2e-07 mm, 1 faces, 0 solids (baked)
FEATURE [Part::Revolution] Revolve100  label="plugHousing054"
  Angle = 360
  Axis = (0,1,0)
  Base = (0,0,0)
  FaceMakerClass = Part::FaceMakerBullseye
  Placement = pos=(0,0,36.15) rot=(0,0,1;0rad)
  Solid = false
  Source = -> Face098
  Symmetric = false
FEATURE [Part::MultiFuse] Fusion069  label="plugHousing057"
  Placement = pos=(0,19,0) rot=(0,0,1;3.14159rad)
  Shapes = -> [Fusion068,Fusion067]
FEATURE [Part::MultiFuse] Fusion070  label="plugHousing058"
  Placement = pos=(0,0,0) rot=(0,0,1;1.5708rad)
  Shapes = -> [Revolve099,Revolve102]
FEATURE [Part::MultiFuse] Fusion071  label="plugHousing059"
  Placement = pos=(0,0,0) rot=(0,0,1;1.5708rad)
  Shapes = -> [Revolve101,Revolve100]
FEATURE [Part::MultiFuse] Fusion072  label="plugHousing060"
  Placement = pos=(0,19,0) rot=(0,0,1;3.14159rad)
  Shapes = -> [Fusion071,Fusion070]
FEATURE [Part::MultiFuse] Fusion073  label="plugHousing061"
  Placement = pos=(129.62,0,-0.15) rot=(0,0,1;0rad)
  Shapes = -> [Fusion069,Fusion072]
